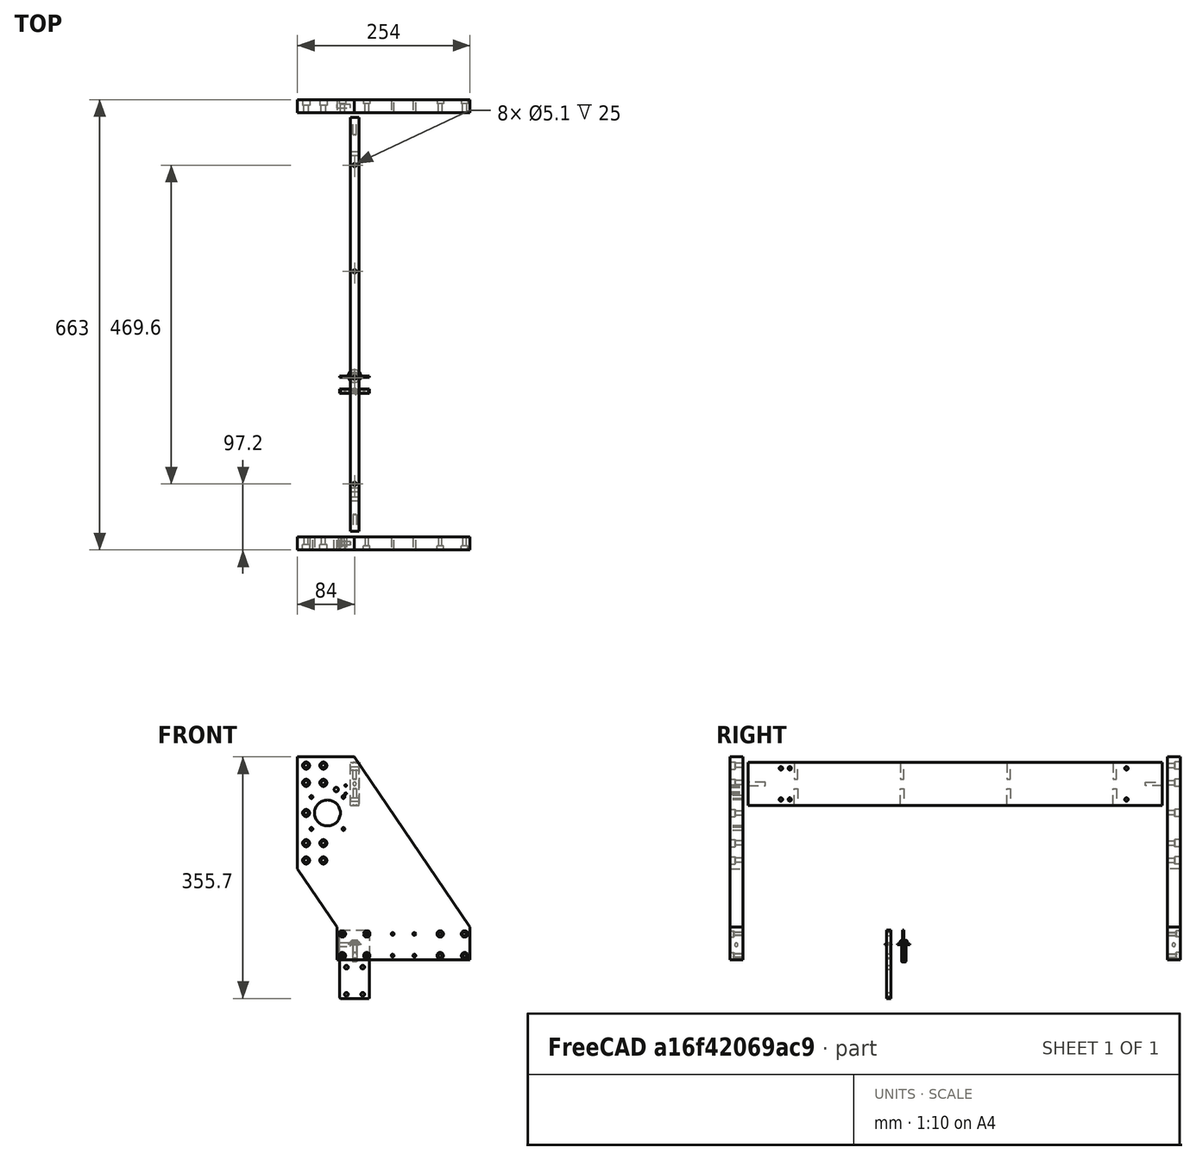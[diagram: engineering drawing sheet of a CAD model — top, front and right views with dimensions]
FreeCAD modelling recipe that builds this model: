
FCSTD DOCUMENT  (FreeCAD 2021.717R24301 +3842 (Git))
Label: X axis plates
License: Creative Commons Attribution
LicenseURL: http://creativecommons.org/licenses/by/4.0/
objects: App::FeaturePython×163, Part::FeaturePython×129, TechDraw::DrawViewDimension×92, App::LinkElement×42, Sketcher::SketchObject×20, App::Link×17, PartDesign::Pocket×9, PartDesign::Hole×6, TechDraw::DrawViewPart×6, PartDesign::Pad×5, PartDesign::Body×5, TechDraw::DrawSVGTemplate×4, TechDraw::DrawPage×4, App::DocumentObjectGroup×3, TechDraw::DrawProjGroupItem×3, PartDesign::Mirrored×2, PartDesign::Chamfer×2, PartDesign::ShapeBinder×1, TechDraw::DrawProjGroup×1
note: 223 computed .brp shape members not serialized (recipe doc carries the construction recipe); baked Part::Feature solids carry a one-line shape summary decoded from their .brp

FEATURE [Sketcher::SketchObject] Sketch
  FullyConstrained = true
  MapMode = 5
  Placement = pos=(0,0,0) rot=(1,0,0;1.5708rad)
  Support = -> [XZ_Plane]
  sketch-geometry (31):
    g0: Circle CenterX=-18 CenterY=16 CenterZ=0 NormalX=0 NormalY=0 NormalZ=1 AngleXU=0 Radius=2.75
    g1: Circle CenterX=18 CenterY=16 CenterZ=0 NormalX=0 NormalY=0 NormalZ=1 AngleXU=0 Radius=2.75
    g2: Circle CenterX=-18 CenterY=-16 CenterZ=0 NormalX=0 NormalY=0 NormalZ=1 AngleXU=0 Radius=2.75
    g3: Circle CenterX=18 CenterY=-16 CenterZ=0 NormalX=0 NormalY=0 NormalZ=1 AngleXU=0 Radius=2.75
    g4: Circle CenterX=126 CenterY=16 CenterZ=0 NormalX=0 NormalY=0 NormalZ=1 AngleXU=0 Radius=2.75
    g5: Circle CenterX=162 CenterY=16 CenterZ=0 NormalX=0 NormalY=0 NormalZ=1 AngleXU=0 Radius=2.75
    g6: Circle CenterX=126 CenterY=-16 CenterZ=0 NormalX=0 NormalY=0 NormalZ=1 AngleXU=0 Radius=2.75
    g7: Circle CenterX=162 CenterY=-16 CenterZ=0 NormalX=0 NormalY=0 NormalZ=1 AngleXU=0 Radius=2.75
    g8: Circle CenterX=-71.3 CenterY=124.3 CenterZ=0 NormalX=0 NormalY=0 NormalZ=1 AngleXU=0 Radius=3.2
    g9: Circle CenterX=-45.9 CenterY=124.3 CenterZ=0 NormalX=0 NormalY=0 NormalZ=1 AngleXU=0 Radius=3.2
    g10: Circle CenterX=-71.3 CenterY=149.7 CenterZ=0 NormalX=0 NormalY=0 NormalZ=1 AngleXU=0 Radius=3.2
    g11: Circle CenterX=-45.9 CenterY=149.7 CenterZ=0 NormalX=0 NormalY=0 NormalZ=1 AngleXU=0 Radius=3.2
    g12: Circle CenterX=-71.3 CenterY=238.6 CenterZ=0 NormalX=0 NormalY=0 NormalZ=1 AngleXU=0 Radius=3.2
    g13: Circle CenterX=-45.9 CenterY=238.6 CenterZ=0 NormalX=0 NormalY=0 NormalZ=1 AngleXU=0 Radius=3.2
    g14: Circle CenterX=-71.3 CenterY=264 CenterZ=0 NormalX=0 NormalY=0 NormalZ=1 AngleXU=0 Radius=3.2
    g15: Circle CenterX=-45.9 CenterY=264 CenterZ=0 NormalX=0 NormalY=0 NormalZ=1 AngleXU=0 Radius=3.2
    g16: LineSegment [constr] StartX=-71.3 StartY=124.3 StartZ=0 EndX=-45.9 EndY=124.3 EndZ=0
    g17: LineSegment [constr] StartX=-71.3 StartY=124.3 StartZ=0 EndX=-71.3 EndY=149.7 EndZ=0
    g18: LineSegment [constr] StartX=-71.3 StartY=238.6 StartZ=0 EndX=-71.3 EndY=264 EndZ=0
    g19: LineSegment [constr] StartX=-18 StartY=16 StartZ=0 EndX=18 EndY=16 EndZ=0
    g20: LineSegment [constr] StartX=126 StartY=16 StartZ=0 EndX=162 EndY=16 EndZ=0
    g21: GeomPoint [constr] X=-71.3 Y=137 Z=0
    g22: GeomPoint [constr] X=72 Y=16 Z=0
    g23: LineSegment StartX=-84 StartY=276.7 StartZ=0 EndX=-84 EndY=111.6 EndZ=0
    g24: LineSegment StartX=-84 StartY=111.6 StartZ=0 EndX=-26 EndY=26 EndZ=0
    g25: LineSegment StartX=-26 StartY=26 StartZ=0 EndX=-26 EndY=-22 EndZ=0
    g26: LineSegment StartX=-26 StartY=-22 StartZ=0 EndX=170 EndY=-22 EndZ=0
    g27: LineSegment StartX=170 StartY=-22 StartZ=0 EndX=170 EndY=26 EndZ=0
    g28: LineSegment StartX=170 StartY=26 StartZ=0 EndX=-0.6 EndY=276.7 EndZ=0
    g29: LineSegment StartX=-0.6 StartY=276.7 StartZ=0 EndX=-84 EndY=276.7 EndZ=0
    g30: GeomPoint [constr] X=72 Y=26 Z=0
  constraints (85):
    c: Vertical(g15,g13)
    c: Vertical(g13,g11)
    c: Vertical(g11,g9)
    c: Vertical(g14,g12)
    c: Vertical(g12,g10)
    c: Vertical(g10,g8)
    c: Horizontal(g14,g15)
    c: Horizontal(g12,g13)
    c: Horizontal(g10,g11)
    c: Horizontal(g8,g9)
    c: Equal(g8,g9)
    c: Equal(g9,g10)
    c: Equal(g10,g11)
    c: Equal(g11,g12)
    c: Equal(g12,g13)
    c: Equal(g13,g14)
    c: Equal(g14,g15)
    c: Horizontal(g0,g1)
    c: Horizontal(g1,g4)
    c: Horizontal(g4,g5)
    c: Horizontal(g2,g3)
    c: Horizontal(g3,g6)
    c: Horizontal(g6,g7)
    c: Vertical(g5,g7)
    c: Vertical(g4,g6)
    c: Vertical(g1,g3)
    c: Coincident(g16,g8)
    c: Coincident(g16,g9)
    c: Coincident(g17,g8)
    c: Coincident(g17,g10)
    c: Equal(g16,g17)
    c: DistanceX(g16,g16) = 25.4
    c: Coincident(g18,g12)
    c: Coincident(g18,g14)
    c: Equal(g18,g17)
    c: DistanceY(g8,g14) = 139.7
    c: Diameter(g14) = 6.4
    c: Diameter(g0) = 5.5
    c: Equal(g0,g1)
    c: Equal(g0,g4)
    c: Equal(g0,g5)
    c: Equal(g0,g7)
    c: Equal(g0,g6)
    c: Equal(g0,g3)
    c: Equal(g0,g2)
    c: Coincident(g19,g0)
    c: Coincident(g19,g1)
    c: Coincident(g20,g4)
    c: Coincident(g20,g5)
    c: Equal(g20,g19)
    c: DistanceX(g19,g19) = 36
    c: DistanceY(g2,g0) = 32
    c: DistanceX(g2,g7) = 180
    c: Symmetric(g2,g1,g-1)
    c: Vertical(g0,g2)
    c: Symmetric(g10,g8,g21)
    c: Symmetric(g1,g4,g22)
    c: Vertical(g23)
    c: Coincident(g23,g24)
    c: Coincident(g24,g25)
    c: Vertical(g25)
    c: Coincident(g25,g26)
    c: Horizontal(g26)
    c: Coincident(g26,g27)
    c: Vertical(g27)
    c: Coincident(g27,g28)
    c: Coincident(g28,g29)
    c: Coincident(g29,g23)
    c: Horizontal(g29)
    c: DistanceX(g25,g2) = 8
    c: DistanceX(g7,g26) = 8
    c: DistanceY(g14,g23) = 12.7
    c: DistanceX(g23,g14) = 12.7
    c: DistanceY(g0,g24) = 10
    c: DistanceY(g23,g8) = 12.7
    c: DistanceY(g25,g-1) = 22
    c: Horizontal(g27,g24)
    c: Symmetric(g24,g27,g30)
    c: DistanceY(g0,g8) = 108.3
    c: DistanceX(g23,g26) = 254
    c: DistanceY(g25,g23) = 298.7
    c: DistanceY(g27,g27) = 48
    c: DistanceX(g26,g26) = 196
    c: DistanceX(g29,g29) = 83.4
    c: DistanceY(g23,g23) = 165.1
FEATURE [PartDesign::Pad] Pad
  ClaimChildren = false
  Direction = (1,1,1)
  Fit = 0
  FitJoin = 0
  InnerFit = 0
  InnerFitJoin = 0
  InnerTaperAngle = 0
  InnerTaperAngleRev = 0
  Length = 19.05
  Length2 = 100
  Linearize = true
  NewSolid = false
  Placement = pos=(0,0,0) rot=(1,0,0;1.5708rad)
  Profile = -> Sketch
  Refine = true
  Reversed = true
  Suppress = false
  Type = 0
  _ProfileBasedVersion = 0
FEATURE [PartDesign::ShapeBinder] ShapeBinder
  Support = -> [Pad]
  TraceSupport = false
FEATURE [PartDesign::Pad] Pad001
  ClaimChildren = false
  Direction = (1,1,1)
  Fit = 0
  FitJoin = 0
  InnerFit = 0
  InnerFitJoin = 0
  InnerTaperAngle = 0
  InnerTaperAngleRev = 0
  Length = 19.05
  Length2 = 100
  Linearize = true
  NewSolid = false
  Profile = -> ShapeBinder
  Refine = true
  Suppress = false
  Type = 0
  _ProfileBasedVersion = 0
FEATURE [Sketcher::SketchObject] Sketch001
  ExternalGeometry = -> [Pad]
  FullyConstrained = true
  MapMode = 5
  Placement = pos=(0,-2e-16,0) rot=(1,0,0;1.5708rad)
  Support = -> [Pad]
  sketch-geometry (8):
    g0: Circle CenterX=-71.3 CenterY=264 CenterZ=0 NormalX=0 NormalY=0 NormalZ=1 AngleXU=0 Radius=3.2
    g1: Circle CenterX=-45.9 CenterY=264 CenterZ=0 NormalX=0 NormalY=0 NormalZ=1 AngleXU=0 Radius=3.2
    g2: Circle CenterX=-45.9 CenterY=238.6 CenterZ=0 NormalX=0 NormalY=0 NormalZ=1 AngleXU=0 Radius=3.2
    g3: Circle CenterX=-71.3 CenterY=238.6 CenterZ=0 NormalX=0 NormalY=0 NormalZ=1 AngleXU=0 Radius=3.2
    g4: Circle CenterX=-71.3 CenterY=149.7 CenterZ=0 NormalX=0 NormalY=0 NormalZ=1 AngleXU=0 Radius=3.2
    g5: Circle CenterX=-45.9 CenterY=149.7 CenterZ=0 NormalX=0 NormalY=0 NormalZ=1 AngleXU=0 Radius=3.2
    g6: Circle CenterX=-45.9 CenterY=124.3 CenterZ=0 NormalX=0 NormalY=0 NormalZ=1 AngleXU=0 Radius=3.2
    g7: Circle CenterX=-71.3 CenterY=124.3 CenterZ=0 NormalX=0 NormalY=0 NormalZ=1 AngleXU=0 Radius=3.2
  constraints (16):
    c: Coincident(g0,g-3)
    c: Coincident(g1,g-4)
    c: Coincident(g2,g-6)
    c: Coincident(g3,g-5)
    c: Coincident(g4,g-7)
    c: Coincident(g5,g-8)
    c: Coincident(g6,g-10)
    c: Coincident(g7,g-9)
    c: Equal(g1,g0)
    c: Equal(g0,g3)
    c: Equal(g3,g2)
    c: Equal(g2,g5)
    c: Equal(g5,g4)
    c: Equal(g4,g7)
    c: Equal(g7,g6)
    c: Equal(g6,g-3)
FEATURE [PartDesign::Hole] Hole
  BaseFeature = -> Pad
  ClaimChildren = false
  CustomThreadClearance = 0
  Depth = 25
  DepthType = 1
  Diameter = 6.4
  DrillForDepth = false
  DrillPoint = 1
  DrillPointAngle = 118
  Fit = 0
  FitJoin = 0
  HoleCutCountersinkAngle = 90
  HoleCutCustomValues = false
  HoleCutDepth = 8
  HoleCutDiameter = 10.5
  HoleCutType = 1
  InnerFit = 0
  InnerFitJoin = 0
  ModelThread = false
  NewSolid = false
  Placement = pos=(0,0,0) rot=(1,0,0;1.5708rad)
  Profile = -> Sketch001
  Refine = true
  Suppress = false
  Tapered = false
  TaperedAngle = 90
  ThreadClass = 0
  ThreadDepth = 896.71
  ThreadDepthType = 0
  ThreadDirection = 0
  ThreadFit = 0
  ThreadSize = 0
  ThreadType = 0
  Threaded = false
  UseCustomThreadClearance = false
  _ProfileBasedVersion = 0
FEATURE [Sketcher::SketchObject] Sketch002
  ExternalGeometry = -> [Hole]
  FullyConstrained = true
  MapMode = 5
  Placement = pos=(0,-2e-16,0) rot=(1,0,0;1.5708rad)
  Support = -> [Hole]
  sketch-geometry (8):
    g0: Circle CenterX=-18 CenterY=16 CenterZ=0 NormalX=0 NormalY=0 NormalZ=1 AngleXU=0 Radius=2.75
    g1: Circle CenterX=18 CenterY=16 CenterZ=0 NormalX=0 NormalY=0 NormalZ=1 AngleXU=0 Radius=2.75
    g2: Circle CenterX=-18 CenterY=-16 CenterZ=0 NormalX=0 NormalY=0 NormalZ=1 AngleXU=0 Radius=2.75
    g3: Circle CenterX=18 CenterY=-16 CenterZ=0 NormalX=0 NormalY=0 NormalZ=1 AngleXU=0 Radius=2.75
    g4: Circle CenterX=126 CenterY=16 CenterZ=0 NormalX=0 NormalY=0 NormalZ=1 AngleXU=0 Radius=2.75
    g5: Circle CenterX=162 CenterY=16 CenterZ=0 NormalX=0 NormalY=0 NormalZ=1 AngleXU=0 Radius=2.75
    g6: Circle CenterX=126 CenterY=-16 CenterZ=0 NormalX=0 NormalY=0 NormalZ=1 AngleXU=0 Radius=2.75
    g7: Circle CenterX=162 CenterY=-16 CenterZ=0 NormalX=0 NormalY=0 NormalZ=1 AngleXU=0 Radius=2.75
  constraints (16):
    c: Coincident(g0,g-3)
    c: Coincident(g1,g-4)
    c: Coincident(g2,g-6)
    c: Coincident(g3,g-5)
    c: Coincident(g4,g-7)
    c: Coincident(g5,g-8)
    c: Coincident(g6,g-9)
    c: Coincident(g7,g-10)
    c: Equal(g0,g1)
    c: Equal(g1,g2)
    c: Equal(g2,g3)
    c: Equal(g3,g4)
    c: Equal(g4,g6)
    c: Equal(g6,g5)
    c: Equal(g5,g7)
    c: Equal(g7,g-3)
FEATURE [PartDesign::Hole] Hole001
  BaseFeature = -> Hole
  ClaimChildren = false
  CustomThreadClearance = 0
  Depth = 25
  DepthType = 1
  Diameter = 5.5
  DrillForDepth = false
  DrillPoint = 1
  DrillPointAngle = 118
  Fit = 0
  FitJoin = 0
  HoleCutCountersinkAngle = 90
  HoleCutCustomValues = false
  HoleCutDepth = 6
  HoleCutDiameter = 9.5
  HoleCutType = 1
  InnerFit = 0
  InnerFitJoin = 0
  ModelThread = false
  NewSolid = false
  Placement = pos=(0,0,0) rot=(1,0,0;1.5708rad)
  Profile = -> Sketch002
  Refine = true
  Suppress = false
  Tapered = false
  TaperedAngle = 90
  ThreadClass = 0
  ThreadDepth = 901.62
  ThreadDepthType = 0
  ThreadDirection = 0
  ThreadFit = 0
  ThreadSize = 0
  ThreadType = 0
  Threaded = false
  UseCustomThreadClearance = false
  _ProfileBasedVersion = 0
FEATURE [Sketcher::SketchObject] Sketch003
  ExternalGeometry = -> [Pad001]
  FullyConstrained = true
  MapMode = 5
  Placement = pos=(0,-2e-16,0) rot=(0,0.707107,0.707107;3.14159rad)
  Support = -> [Pad001]
  sketch-geometry (8):
    g0: Circle CenterX=45.9 CenterY=238.6 CenterZ=0 NormalX=0 NormalY=0 NormalZ=1 AngleXU=0 Radius=3.2
    g1: Circle CenterX=71.3 CenterY=238.6 CenterZ=0 NormalX=0 NormalY=0 NormalZ=1 AngleXU=0 Radius=3.2
    g2: Circle CenterX=71.3 CenterY=149.7 CenterZ=0 NormalX=0 NormalY=0 NormalZ=1 AngleXU=0 Radius=3.2
    g3: Circle CenterX=45.9 CenterY=149.7 CenterZ=0 NormalX=0 NormalY=0 NormalZ=1 AngleXU=0 Radius=3.2
    g4: Circle CenterX=45.9 CenterY=124.3 CenterZ=0 NormalX=0 NormalY=0 NormalZ=1 AngleXU=0 Radius=3.2
    g5: Circle CenterX=71.3 CenterY=124.3 CenterZ=0 NormalX=0 NormalY=0 NormalZ=1 AngleXU=0 Radius=3.2
    g6: Circle CenterX=71.3 CenterY=264 CenterZ=0 NormalX=0 NormalY=0 NormalZ=1 AngleXU=0 Radius=3.2
    g7: Circle CenterX=45.9 CenterY=264 CenterZ=0 NormalX=0 NormalY=0 NormalZ=1 AngleXU=0 Radius=3.2
  constraints (16):
    c: Coincident(g0,g-3)
    c: Coincident(g1,g-10)
    c: Coincident(g2,g-4)
    c: Coincident(g3,g-5)
    c: Coincident(g4,g-6)
    c: Coincident(g5,g-7)
    c: Coincident(g6,g-8)
    c: Coincident(g7,g-9)
    c: Equal(g1,g0)
    c: Equal(g0,g3)
    c: Equal(g3,g2)
    c: Equal(g2,g5)
    c: Equal(g5,g4)
    c: Equal(g4,g7)
    c: Equal(g7,g6)
    c: Equal(g6,g-10)
FEATURE [PartDesign::Hole] Hole002
  BaseFeature = -> Pad001
  ClaimChildren = false
  CustomThreadClearance = 0
  Depth = 25
  DepthType = 1
  Diameter = 6.4
  DrillForDepth = false
  DrillPoint = 1
  DrillPointAngle = 118
  Fit = 0
  FitJoin = 0
  HoleCutCountersinkAngle = 90
  HoleCutCustomValues = false
  HoleCutDepth = 8
  HoleCutDiameter = 10.5
  HoleCutType = 1
  InnerFit = 0
  InnerFitJoin = 0
  ModelThread = false
  NewSolid = false
  Profile = -> Sketch003
  Refine = true
  Suppress = false
  Tapered = false
  TaperedAngle = 90
  ThreadClass = 0
  ThreadDepth = 901.62
  ThreadDepthType = 0
  ThreadDirection = 0
  ThreadFit = 0
  ThreadSize = 0
  ThreadType = 0
  Threaded = false
  UseCustomThreadClearance = false
  _ProfileBasedVersion = 0
FEATURE [Sketcher::SketchObject] Sketch004
  ExternalGeometry = -> [Hole002]
  FullyConstrained = false
  MapMode = 5
  Placement = pos=(0,-2e-16,0) rot=(0,0.707107,0.707107;3.14159rad)
  Support = -> [Hole002]
  sketch-geometry (9):
    g0: Circle CenterX=18 CenterY=-16 CenterZ=0 NormalX=0 NormalY=0 NormalZ=1 AngleXU=0 Radius=2.75
    g1: Circle CenterX=-162 CenterY=16 CenterZ=0 NormalX=0 NormalY=0 NormalZ=1 AngleXU=0 Radius=2.75
    g2: Circle CenterX=-162 CenterY=-16 CenterZ=0 NormalX=0 NormalY=0 NormalZ=1 AngleXU=0 Radius=2.75
    g3: Circle CenterX=-18 CenterY=-16 CenterZ=0 NormalX=0 NormalY=0 NormalZ=1 AngleXU=0 Radius=2.75
    g4: Circle CenterX=-126 CenterY=-16 CenterZ=0 NormalX=0 NormalY=0 NormalZ=1 AngleXU=0 Radius=2.75
    g5: Circle CenterX=-18 CenterY=16 CenterZ=0 NormalX=0 NormalY=0 NormalZ=1 AngleXU=0 Radius=2.75
    g6: Circle CenterX=18 CenterY=16 CenterZ=0 NormalX=0 NormalY=0 NormalZ=1 AngleXU=0 Radius=2.75
    g7: Circle CenterX=18 CenterY=16 CenterZ=0 NormalX=0 NormalY=0 NormalZ=1 AngleXU=0 Radius=2.75
    g8: Circle CenterX=-126 CenterY=16 CenterZ=0 NormalX=0 NormalY=0 NormalZ=1 AngleXU=0 Radius=2.75
  constraints (17):
    c: Coincident(g0,g-3)
    c: Coincident(g1,g-4)
    c: Coincident(g2,g-5)
    c: Coincident(g3,g-6)
    c: Coincident(g4,g-7)
    c: Coincident(g5,g-8)
    c: Coincident(g7,g-9)
    c: Equal(g0,g1)
    c: Equal(g1,g4)
    c: Equal(g4,g6)
    c: Equal(g6,g7)
    c: Equal(g7,g5)
    c: Equal(g5,g2)
    c: Equal(g2,g3)
    c: Equal(g3,g-3)
    c: Coincident(g8,g-10)
    c: Equal(g8,g0)
FEATURE [PartDesign::Hole] Hole003
  BaseFeature = -> Hole002
  ClaimChildren = false
  CustomThreadClearance = 0
  Depth = 25
  DepthType = 1
  Diameter = 5.5
  DrillForDepth = false
  DrillPoint = 1
  DrillPointAngle = 118
  Fit = 0
  FitJoin = 0
  HoleCutCountersinkAngle = 90
  HoleCutCustomValues = false
  HoleCutDepth = 6
  HoleCutDiameter = 9.5
  HoleCutType = 1
  InnerFit = 0
  InnerFitJoin = 0
  ModelThread = false
  NewSolid = false
  Profile = -> Sketch004
  Refine = true
  Suppress = false
  Tapered = false
  TaperedAngle = 90
  ThreadClass = 0
  ThreadDepth = 901.62
  ThreadDepthType = 0
  ThreadDirection = 0
  ThreadFit = 0
  ThreadSize = 0
  ThreadType = 0
  Threaded = false
  UseCustomThreadClearance = false
  _ProfileBasedVersion = 0
FEATURE [App::Link] Link  label="Link(Left plate)"
  AutoLinkLabel = true
  AutoPlacement = true
  LinkedObject = -> Body
  SyncGroupVisibility = false
  _LinkVersion = 1
FEATURE [App::Link] Link001  label="Link001(Right plate)"
  AutoLinkLabel = true
  AutoPlacement = true
  LinkPlacement = pos=(0,254,0) rot=(0,0,1;0rad)
  LinkedObject = -> Body001
  Placement = pos=(0,254,0) rot=(0,0,1;0rad)
  SyncGroupVisibility = false
  _LinkVersion = 1
FEATURE [Sketcher::SketchObject] Sketch005
  ExternalGeometry = -> [Hole001]
  FullyConstrained = true
  MapMode = 5
  Placement = pos=(0,-2e-16,0) rot=(1,0,0;1.5708rad)
  Support = -> [Hole001]
  sketch-geometry (8):
    g0: Circle CenterX=-39.95 CenterY=194.15 CenterZ=0 NormalX=0 NormalY=0 NormalZ=1 AngleXU=0 Radius=19.05
    g1: Circle CenterX=-63.5 CenterY=217.7 CenterZ=0 NormalX=0 NormalY=0 NormalZ=1 AngleXU=0 Radius=2.1
    g2: Circle CenterX=-16.4 CenterY=217.7 CenterZ=0 NormalX=0 NormalY=0 NormalZ=1 AngleXU=0 Radius=2.1
    g3: Circle CenterX=-63.5 CenterY=170.6 CenterZ=0 NormalX=0 NormalY=0 NormalZ=1 AngleXU=0 Radius=2.1
    g4: Circle CenterX=-16.4 CenterY=170.6 CenterZ=0 NormalX=0 NormalY=0 NormalZ=1 AngleXU=0 Radius=2.1
    g5: LineSegment [constr] StartX=-63.5 StartY=217.7 StartZ=0 EndX=-16.4 EndY=217.7 EndZ=0
    g6: LineSegment [constr] StartX=-63.5 StartY=217.7 StartZ=0 EndX=-63.5 EndY=170.6 EndZ=0
    g7: GeomPoint [constr] X=-71.3 Y=194.15 Z=0
  constraints (19):
    c: Diameter(g0) = 38.1
    c: Horizontal(g4,g3)
    c: Horizontal(g1,g2)
    c: Vertical(g2,g4)
    c: Vertical(g1,g3)
    c: Symmetric(g1,g4,g0)
    c: Diameter(g2) = 4.2
    c: Equal(g2,g1)
    c: Equal(g2,g3)
    c: Equal(g2,g4)
    c: Coincident(g5,g1)
    c: Coincident(g5,g2)
    c: Coincident(g6,g1)
    c: Coincident(g6,g3)
    c: Equal(g5,g6)
    c: DistanceX(g5,g5) = 47.1
    c: Symmetric(g-3,g-4,g7)
    c: Horizontal(g7,g0)
    c: DistanceX(g7,g0) = 31.35
FEATURE [PartDesign::Pocket] Pocket
  BaseFeature = -> Hole001
  ClaimChildren = false
  Fit = 0
  FitJoin = 0
  InnerFit = 0
  InnerFitJoin = 0
  InnerTaperAngle = 0
  InnerTaperAngleRev = 0
  Length = 5
  Length2 = 100
  Linearize = true
  NewSolid = false
  Placement = pos=(0,0,0) rot=(1,0,0;1.5708rad)
  Profile = -> Sketch005
  Refine = true
  Suppress = false
  Type = 1
  _ProfileBasedVersion = 0
FEATURE [Sketcher::SketchObject] Sketch006
  FullyConstrained = true
  MapMode = 5
  Placement = pos=(0,0,0) rot=(0.57735,0.57735,0.57735;2.0944rad)
  Support = -> [YZ_Plane002]
  sketch-geometry (4):
    g0: LineSegment StartX=-304.8 StartY=31.75 StartZ=0 EndX=304.8 EndY=31.75 EndZ=0
    g1: LineSegment StartX=304.8 StartY=31.75 StartZ=0 EndX=304.8 EndY=-31.75 EndZ=0
    g2: LineSegment StartX=304.8 StartY=-31.75 StartZ=0 EndX=-304.8 EndY=-31.75 EndZ=0
    g3: LineSegment StartX=-304.8 StartY=-31.75 StartZ=0 EndX=-304.8 EndY=31.75 EndZ=0
  constraints (11):
    c: Coincident(g0,g1)
    c: Coincident(g1,g2)
    c: Coincident(g2,g3)
    c: Coincident(g3,g0)
    c: Horizontal(g0)
    c: Horizontal(g2)
    c: Vertical(g1)
    c: Vertical(g3)
    c: Symmetric(g0,g2,g-1)
    c: DistanceY(g1,g1) = 63.5
    c: DistanceX(g0,g0) = 609.6
FEATURE [PartDesign::Pad] Pad002
  ClaimChildren = false
  Direction = (1,1,1)
  Fit = 0
  FitJoin = 0
  InnerFit = 0
  InnerFitJoin = 0
  InnerTaperAngle = 0
  InnerTaperAngleRev = 0
  Length = 12.7
  Length2 = 100
  Linearize = true
  Midplane = true
  NewSolid = false
  Placement = pos=(0,0,0) rot=(0.57735,0.57735,0.57735;2.0944rad)
  Profile = -> Sketch006
  Refine = true
  Suppress = false
  Type = 0
  _ProfileBasedVersion = 0
FEATURE [Sketcher::SketchObject] Sketch007
  FullyConstrained = true
  MapMode = 5
  Placement = pos=(-1.341e-13,-304.8,6.71e-14) rot=(-0.57735,-0.57735,0.57735;4.18879rad)
  Support = -> [Pad002]
  sketch-geometry (1):
    g0: Circle CenterX=0 CenterY=0 CenterZ=0 NormalX=0 NormalY=0 NormalZ=1 AngleXU=0 Radius=2.5
  constraints (2):
    c: Diameter(g0) = 5
    c: Coincident(g0,g-1)
FEATURE [PartDesign::Pocket] Pocket001
  BaseFeature = -> Pad002
  ClaimChildren = false
  Fit = 0
  FitJoin = 0
  InnerFit = 0
  InnerFitJoin = 0
  InnerTaperAngle = 0
  InnerTaperAngleRev = 0
  Length = 25
  Length2 = 100
  Linearize = true
  NewSolid = false
  Placement = pos=(0,0,0) rot=(0.57735,0.57735,0.57735;2.0944rad)
  Profile = -> Sketch007
  Refine = true
  Suppress = false
  Type = 0
  _ProfileBasedVersion = 0
FEATURE [Sketcher::SketchObject] Sketch008
  ExternalGeometry = -> [Pocket001]
  FullyConstrained = true
  MapMode = 5
  Placement = pos=(-2.29e-14,2.11e-14,31.75) rot=(0,0,-1;1.5708rad)
  sketch-geometry (9):
    g0: Circle CenterX=-234.8 CenterY=0 CenterZ=0 NormalX=0 NormalY=0 NormalZ=1 AngleXU=0 Radius=2.55
    g1: Circle CenterX=-78.2667 CenterY=0 CenterZ=0 NormalX=0 NormalY=0 NormalZ=1 AngleXU=0 Radius=2.55
    g2: Circle CenterX=78.2667 CenterY=0 CenterZ=0 NormalX=0 NormalY=0 NormalZ=1 AngleXU=0 Radius=2.55
    g3: Circle CenterX=234.8 CenterY=0 CenterZ=0 NormalX=0 NormalY=0 NormalZ=1 AngleXU=0 Radius=2.55
    g4: LineSegment [constr] StartX=-234.8 StartY=0 StartZ=0 EndX=-304.8 EndY=0 EndZ=0
    g5: LineSegment [constr] StartX=-234.8 StartY=0 StartZ=0 EndX=-78.2667 EndY=0 EndZ=0
    g6: LineSegment [constr] StartX=-78.2667 StartY=0 StartZ=0 EndX=78.2667 EndY=0 EndZ=0
    g7: LineSegment [constr] StartX=234.8 StartY=0 StartZ=0 EndX=78.2667 EndY=0 EndZ=0
    g8: LineSegment [constr] StartX=234.8 StartY=0 StartZ=0 EndX=304.8 EndY=0 EndZ=0
  constraints (24):
    c: PointOnObject(g0,g-1)
    c: PointOnObject(g1,g-1)
    c: Equal(g0,g1)
    c: DistanceX(g-3,g0) = 70
    c: PointOnObject(g2,g-1)
    c: PointOnObject(g3,g-1)
    c: Coincident(g4,g0)
    c: PointOnObject(g4,g-3)
    c: Horizontal(g4)
    c: Coincident(g5,g0)
    c: Coincident(g5,g1)
    c: Coincident(g6,g1)
    c: Coincident(g7,g3)
    c: Coincident(g7,g2)
    c: Coincident(g8,g3)
    c: PointOnObject(g8,g-1)
    c: Vertical(g8,g-4)
    c: Equal(g8,g4)
    c: Equal(g5,g6)
    c: Diameter(g0) = 5.1
    c: Coincident(g6,g2)
    c: Equal(g7,g6)
    c: Equal(g3,g2)
    c: Equal(g2,g1)
FEATURE [App::Link] Link003  label="Link003(Rear plate)"
  AutoLinkLabel = true
  AutoPlacement = true
  LinkPlacement = pos=(0,76,237) rot=(0,0,1;0rad)
  LinkedObject = -> Body002
  Placement = pos=(0,76,237) rot=(0,0,1;0rad)
  SyncGroupVisibility = false
  _LinkVersion = 1
FEATURE [Part::FeaturePython] Parts003  # WARN: FeaturePython — macro-defined, semantics opaque (R4)
  Group = -> [Link003]
  GroupMode = 0
  _LinkVersion = 1
FEATURE [Sketcher::SketchObject] Sketch014
  ExternalGeometry = -> [Hole003]
  FullyConstrained = true
  MapMode = 5
  Placement = pos=(0,-2e-16,0) rot=(0,0.707107,0.707107;3.14159rad)
  Support = -> [Hole003]
  sketch-geometry (1):
    g0: Circle CenterX=71.3 CenterY=194.15 CenterZ=0 NormalX=0 NormalY=0 NormalZ=1 AngleXU=0 Radius=3.05
  constraints (2):
    c: Diameter(g0) = 6.1
    c: Symmetric(g-3,g-4,g0)
FEATURE [PartDesign::Hole] Hole004
  BaseFeature = -> Hole003
  ClaimChildren = false
  CustomThreadClearance = 0
  Depth = 25
  DepthType = 1
  Diameter = 6.4
  DrillForDepth = false
  DrillPoint = 1
  DrillPointAngle = 118
  Fit = 0
  FitJoin = 0
  HoleCutCountersinkAngle = 90
  HoleCutCustomValues = false
  HoleCutDepth = 8
  HoleCutDiameter = 10.5
  HoleCutType = 1
  InnerFit = 0
  InnerFitJoin = 0
  ModelThread = false
  NewSolid = false
  Profile = -> Sketch014
  Refine = true
  Suppress = false
  Tapered = false
  TaperedAngle = 90
  ThreadClass = 0
  ThreadDepth = 901.62
  ThreadDepthType = 0
  ThreadDirection = 0
  ThreadFit = 0
  ThreadSize = 0
  ThreadType = 0
  Threaded = false
  UseCustomThreadClearance = false
  _ProfileBasedVersion = 0
FEATURE [Sketcher::SketchObject] Sketch015
  ExternalGeometry = -> [Pocket]
  FullyConstrained = true
  MapMode = 5
  Placement = pos=(0,-2e-16,0) rot=(1,0,0;1.5708rad)
  Support = -> [Pocket]
  sketch-geometry (1):
    g0: Circle CenterX=-71.3 CenterY=194.15 CenterZ=0 NormalX=0 NormalY=0 NormalZ=1 AngleXU=0 Radius=3.05
  constraints (2):
    c: Diameter(g0) = 6.1
    c: Symmetric(g-3,g-4,g0)
FEATURE [PartDesign::Hole] Hole005
  BaseFeature = -> Pocket
  ClaimChildren = false
  CustomThreadClearance = 0
  Depth = 25
  DepthType = 1
  Diameter = 6.4
  DrillForDepth = false
  DrillPoint = 1
  DrillPointAngle = 118
  Fit = 0
  FitJoin = 0
  HoleCutCountersinkAngle = 90
  HoleCutCustomValues = false
  HoleCutDepth = 8
  HoleCutDiameter = 10.5
  HoleCutType = 1
  InnerFit = 0
  InnerFitJoin = 0
  ModelThread = false
  NewSolid = false
  Placement = pos=(0,0,0) rot=(1,0,0;1.5708rad)
  Profile = -> Sketch015
  Refine = true
  Suppress = false
  Tapered = false
  TaperedAngle = 90
  ThreadClass = 0
  ThreadDepth = 901.62
  ThreadDepthType = 0
  ThreadDirection = 0
  ThreadFit = 0
  ThreadSize = 0
  ThreadType = 0
  Threaded = false
  UseCustomThreadClearance = false
  _ProfileBasedVersion = 0
FEATURE [Sketcher::SketchObject] Sketch021
  ExternalGeometry = -> [Hole004]
  FullyConstrained = true
  MapMode = 5
  Placement = pos=(0,-2e-16,0) rot=(0,0.707107,0.707107;3.14159rad)
  sketch-geometry (6):
    g0: GeomPoint [constr] X=-72 Y=-16 Z=0
    g1: GeomPoint [constr] X=-72 Y=-3.6e-15 Z=0
    g2: Circle CenterX=-88 CenterY=16 CenterZ=0 NormalX=0 NormalY=0 NormalZ=1 AngleXU=0 Radius=2.1
    g3: Circle CenterX=-88 CenterY=-16 CenterZ=0 NormalX=0 NormalY=0 NormalZ=1 AngleXU=0 Radius=2.1
    g4: Circle CenterX=-56 CenterY=16 CenterZ=0 NormalX=0 NormalY=0 NormalZ=1 AngleXU=0 Radius=2.1
    g5: Circle CenterX=-56 CenterY=-16 CenterZ=0 NormalX=0 NormalY=0 NormalZ=1 AngleXU=0 Radius=2.1
  constraints (13):
    c: Vertical(g1,g0)
    c: Equal(g5,g4)
    c: Equal(g4,g2)
    c: Equal(g2,g3)
    c: Vertical(g2,g3)
    c: Horizontal(g2,g4)
    c: Symmetric(g2,g5,g1)
    c: Symmetric(g3,g4,g1)
    c: Diameter(g4) = 4.2
    c: DistanceX(g2,g4) = 32
    c: DistanceY(g5,g4) = 32
    c: Horizontal(g5,g0)
    c: Symmetric(g-4,g-3,g0)
FEATURE [Sketcher::SketchObject] Sketch022
  ExternalGeometry = -> [Hole005]
  FullyConstrained = true
  MapMode = 5
  Placement = pos=(0,-2e-16,0) rot=(1,0,0;1.5708rad)
  Support = -> [Hole005]
  sketch-geometry (6):
    g0: GeomPoint [constr] X=72 Y=-16 Z=0
    g1: GeomPoint [constr] X=72 Y=6.6e-15 Z=0
    g2: Circle CenterX=56 CenterY=16 CenterZ=0 NormalX=0 NormalY=0 NormalZ=1 AngleXU=0 Radius=2.1
    g3: Circle CenterX=56 CenterY=-16 CenterZ=0 NormalX=0 NormalY=0 NormalZ=1 AngleXU=0 Radius=2.1
    g4: Circle CenterX=88 CenterY=16 CenterZ=0 NormalX=0 NormalY=0 NormalZ=1 AngleXU=0 Radius=2.1
    g5: Circle CenterX=88 CenterY=-16 CenterZ=0 NormalX=0 NormalY=0 NormalZ=1 AngleXU=0 Radius=2.1
  constraints (13):
    c: Vertical(g1,g0)
    c: Equal(g5,g4)
    c: Equal(g4,g2)
    c: Equal(g2,g3)
    c: Vertical(g2,g3)
    c: Horizontal(g2,g4)
    c: Symmetric(g2,g5,g1)
    c: Symmetric(g3,g4,g1)
    c: Diameter(g4) = 4.2
    c: DistanceX(g2,g4) = 32
    c: DistanceY(g5,g4) = 32
    c: Symmetric(g-3,g-4,g0)
    c: Horizontal(g5,g-4)
FEATURE [PartDesign::Mirrored] Mirrored001
  BaseFeature = -> Pocket001
  CopyShape = false
  MirrorPlane = -> XZ_Plane002
  NewSolid = false
  OriginalSubs = -> [Pocket001]
  Originals = -> [Pocket001]
  ParallelTransform = true
  Placement = pos=(0,0,0) rot=(0.57735,0.57735,0.57735;2.0944rad)
  Refine = true
  SubTransform = true
  Suppress = false
  _Version = 1
FEATURE [PartDesign::Pocket] Pocket002
  BaseFeature = -> Mirrored001
  ClaimChildren = false
  Fit = 0
  FitJoin = 0
  InnerFit = 0
  InnerFitJoin = 0
  InnerTaperAngle = 0
  InnerTaperAngleRev = 0
  Length = 25
  Length2 = 100
  Linearize = true
  NewSolid = false
  Placement = pos=(0,0,0) rot=(0.57735,0.57735,0.57735;2.0944rad)
  Profile = -> Sketch008
  Refine = true
  Suppress = false
  Type = 0
  _ProfileBasedVersion = 0
FEATURE [PartDesign::Mirrored] Mirrored
  BaseFeature = -> Pocket002
  CopyShape = false
  MirrorPlane = -> XY_Plane002
  NewSolid = false
  OriginalSubs = -> [Pocket002]
  Originals = -> [Pocket002]
  ParallelTransform = true
  Placement = pos=(0,0,0) rot=(0.57735,0.57735,0.57735;2.0944rad)
  Refine = true
  SubTransform = true
  Suppress = false
  _Version = 1
FEATURE [Sketcher::SketchObject] Sketch016
  ExternalGeometry = -> [Mirrored]
  FullyConstrained = true
  MapMode = 5
  Placement = pos=(6.35,-1.4e-15,1.4e-15) rot=(0.57735,0.57735,0.57735;2.0944rad)
  Support = -> [Mirrored]
  sketch-geometry (7):
    g0: Circle CenterX=-256.75 CenterY=23 CenterZ=0 NormalX=0 NormalY=0 NormalZ=1 AngleXU=0 Radius=2.5
    g1: Circle CenterX=-256.75 CenterY=-23 CenterZ=0 NormalX=0 NormalY=0 NormalZ=1 AngleXU=0 Radius=2.5
    g2: Circle CenterX=-243.75 CenterY=23 CenterZ=0 NormalX=0 NormalY=0 NormalZ=1 AngleXU=0 Radius=2.5
    g3: Circle CenterX=-243.75 CenterY=-23 CenterZ=0 NormalX=0 NormalY=0 NormalZ=1 AngleXU=0 Radius=2.5
    g4: GeomPoint [constr] X=-262.6 Y=23 Z=0
    g5: Circle CenterX=251.9 CenterY=23 CenterZ=0 NormalX=0 NormalY=0 NormalZ=1 AngleXU=0 Radius=2.5
    g6: Circle CenterX=251.9 CenterY=-23 CenterZ=0 NormalX=0 NormalY=0 NormalZ=1 AngleXU=0 Radius=2.5
  constraints (20):
    c: Vertical(g3,g2)
    c: Horizontal(g1,g3)
    c: Horizontal(g0,g2)
    c: Equal(g0,g2)
    c: Equal(g2,g3)
    c: Equal(g3,g1)
    c: Symmetric(g0,g1,g-1)
    c: Diameter(g0) = 5
    c: DistanceX(g0,g2) = 13
    c: DistanceY(g1,g0) = 46
    c: Horizontal(g4,g0)
    c: DistanceX(g4,g0) = 5.85
    c: Vertical(g6,g5)
    c: Horizontal(g6,g3)
    c: Horizontal(g2,g5)
    c: Equal(g5,g6)
    c: Equal(g6,g2)
    c: DistanceX(g-3,g4) = 42.2
    c: DistanceX(g-3,g0) = 48.05
    c: DistanceX(g4,g5) = 514.5
FEATURE [PartDesign::Pocket] Pocket007
  BaseFeature = -> Mirrored
  ClaimChildren = false
  Fit = 0
  FitJoin = 0
  InnerFit = 0
  InnerFitJoin = 0
  InnerTaperAngle = 0
  InnerTaperAngleRev = 0
  Length = 5
  Length2 = 100
  Linearize = true
  NewSolid = false
  Placement = pos=(0,0,0) rot=(0.57735,0.57735,0.57735;2.0944rad)
  Profile = -> Sketch016
  Refine = true
  Suppress = false
  Type = 1
  _ProfileBasedVersion = 0
FEATURE [PartDesign::Body] Body002  label="Rear plate"
  AutoGroupSolids = false
  ExportMode = 0
  Group = -> [Sketch006,Pad002,Sketch007,Pocket001,Sketch008,Mirrored001,Pocket002,Mirrored,Sketch016,Pocket007]
  Origin = -> Origin002
  Placement = pos=(0,76,237) rot=(0,0,1;0rad)
  Tip = -> Pocket007
  _ExportChildren = -> [Pad002,Pocket001,Mirrored001,Pocket002,Mirrored,Pocket007]
  _GroupVersion = 1
FEATURE [PartDesign::Pocket] Pocket010
  BaseFeature = -> Hole005
  ClaimChildren = false
  Fit = 0
  FitJoin = 0
  InnerFit = 0
  InnerFitJoin = 0
  InnerTaperAngle = 0
  InnerTaperAngleRev = 0
  Length = 5
  Length2 = 100
  Linearize = true
  NewSolid = false
  Placement = pos=(0,0,0) rot=(1,0,0;1.5708rad)
  Profile = -> Sketch022
  Refine = true
  Suppress = false
  Type = 1
  _ProfileBasedVersion = 0
FEATURE [PartDesign::Pocket] Pocket011
  BaseFeature = -> Hole004
  ClaimChildren = false
  Fit = 0
  FitJoin = 0
  InnerFit = 0
  InnerFitJoin = 0
  InnerTaperAngle = 0
  InnerTaperAngleRev = 0
  Length = 5
  Length2 = 100
  Linearize = true
  NewSolid = false
  Profile = -> Sketch021
  Refine = true
  Suppress = false
  Type = 1
  _ProfileBasedVersion = 0
FEATURE [Sketcher::SketchObject] Sketch023
  FullyConstrained = true
  MapMode = 5
  Placement = pos=(0,0,0) rot=(1,0,0;1.5708rad)
  Support = -> [XZ_Plane005]
  sketch-geometry (8):
    g0: LineSegment StartX=-22 StartY=22 StartZ=0 EndX=22 EndY=22 EndZ=0
    g1: LineSegment StartX=22 StartY=22 StartZ=0 EndX=22 EndY=-22 EndZ=0
    g2: LineSegment StartX=22 StartY=-22 StartZ=0 EndX=-22 EndY=-22 EndZ=0
    g3: LineSegment StartX=-22 StartY=-22 StartZ=0 EndX=-22 EndY=22 EndZ=0
    g4: Circle CenterX=-16 CenterY=16 CenterZ=0 NormalX=0 NormalY=0 NormalZ=1 AngleXU=0 Radius=2.75
    g5: Circle CenterX=16 CenterY=16 CenterZ=0 NormalX=0 NormalY=0 NormalZ=1 AngleXU=0 Radius=2.75
    g6: Circle CenterX=-16 CenterY=-16 CenterZ=0 NormalX=0 NormalY=0 NormalZ=1 AngleXU=0 Radius=2.75
    g7: Circle CenterX=16 CenterY=-16 CenterZ=0 NormalX=0 NormalY=0 NormalZ=1 AngleXU=0 Radius=2.75
  constraints (21):
    c: Coincident(g0,g1)
    c: Coincident(g1,g2)
    c: Coincident(g2,g3)
    c: Coincident(g3,g0)
    c: Horizontal(g0)
    c: Horizontal(g2)
    c: Vertical(g1)
    c: Vertical(g3)
    c: Symmetric(g1,g0,g-1)
    c: Equal(g0,g3)
    c: Diameter(g5) = 5.5
    c: Equal(g5,g4)
    c: Equal(g5,g6)
    c: Equal(g5,g7)
    c: Symmetric(g5,g6,g-1)
    c: Symmetric(g4,g7,g-1)
    c: Horizontal(g4,g5)
    c: Vertical(g6,g4)
    c: DistanceX(g4,g5) = 32
    c: DistanceY(g7,g5) = 32
    c: DistanceX(g0,g0) = 44
FEATURE [PartDesign::Pad] Pad005
  ClaimChildren = false
  Direction = (1,1,1)
  Fit = 0
  FitJoin = 0
  InnerFit = 0
  InnerFitJoin = 0
  InnerTaperAngle = 0
  InnerTaperAngleRev = 0
  Length = 1.825
  Length2 = 100
  Linearize = true
  NewSolid = false
  Placement = pos=(0,0,0) rot=(1,0,0;1.5708rad)
  Profile = -> Sketch023
  Refine = true
  Suppress = false
  Type = 0
  _ProfileBasedVersion = 0
FEATURE [PartDesign::Chamfer] Chamfer
  Angle = 45
  Base = -> Pad005 [Edge2,Edge1,Edge5,Edge8]
  BaseFeature = -> Pad005
  ChamferType = 0
  FlipDirection = false
  NewSolid = false
  Placement = pos=(0,0,0) rot=(1,0,0;1.5708rad)
  Refine = true
  Size = 1
  Size2 = 1
  SupportTransform = false
  Suppress = false
FEATURE [PartDesign::Body] Body005  label="Gouverner shim"
  AutoGroupSolids = false
  ExportMode = 0
  Group = -> [Sketch023,Pad005,Chamfer]
  Origin = -> Origin005
  Tip = -> Chamfer
  _ExportChildren = -> [Pad005,Chamfer]
  _GroupVersion = 1
FEATURE [Sketcher::SketchObject] Sketch024
  FullyConstrained = true
  MapMode = 5
  Placement = pos=(0,0,0) rot=(1,0,0;1.5708rad)
  Support = -> [XZ_Plane006]
  sketch-geometry (12):
    g0: LineSegment StartX=-22 StartY=22 StartZ=0 EndX=22 EndY=22 EndZ=0
    g1: LineSegment StartX=22 StartY=22 StartZ=0 EndX=22 EndY=-79 EndZ=0
    g2: LineSegment StartX=22 StartY=-79 StartZ=0 EndX=-22 EndY=-79 EndZ=0
    g3: LineSegment StartX=-22 StartY=-79 StartZ=0 EndX=-22 EndY=22 EndZ=0
    g4: Circle CenterX=-16 CenterY=16 CenterZ=0 NormalX=0 NormalY=0 NormalZ=1 AngleXU=0 Radius=2.75
    g5: Circle CenterX=16 CenterY=16 CenterZ=0 NormalX=0 NormalY=0 NormalZ=1 AngleXU=0 Radius=2.75
    g6: Circle CenterX=-16 CenterY=-16 CenterZ=0 NormalX=0 NormalY=0 NormalZ=1 AngleXU=0 Radius=2.75
    g7: Circle CenterX=16 CenterY=-16 CenterZ=0 NormalX=0 NormalY=0 NormalZ=1 AngleXU=0 Radius=2.75
    g8: Circle CenterX=-12 CenterY=-33 CenterZ=0 NormalX=0 NormalY=0 NormalZ=1 AngleXU=0 Radius=2.75
    g9: Circle CenterX=12 CenterY=-33 CenterZ=0 NormalX=0 NormalY=0 NormalZ=1 AngleXU=0 Radius=2.75
    g10: Circle CenterX=-12 CenterY=-73 CenterZ=0 NormalX=0 NormalY=0 NormalZ=1 AngleXU=0 Radius=2.75
    g11: Circle CenterX=12 CenterY=-73 CenterZ=0 NormalX=0 NormalY=0 NormalZ=1 AngleXU=0 Radius=2.75
  constraints (32):
    c: Coincident(g0,g1)
    c: Coincident(g1,g2)
    c: Coincident(g2,g3)
    c: Coincident(g3,g0)
    c: Horizontal(g2)
    c: Vertical(g1)
    c: Vertical(g3)
    c: DistanceX(g0,g0) = 44
    c: Symmetric(g0,g0,g-2)
    c: DistanceY(g-1,g0) = 22
    c: Diameter(g7) = 5.5
    c: Equal(g7,g6)
    c: Equal(g7,g4)
    c: Equal(g7,g5)
    c: Horizontal(g6,g7)
    c: Vertical(g4,g6)
    c: Symmetric(g4,g5,g-2)
    c: DistanceX(g4,g5) = 32
    c: Symmetric(g5,g7,g-1)
    c: DistanceY(g7,g5) = 32
    c: Horizontal(g11,g10)
    c: Vertical(g9,g11)
    c: Vertical(g8,g10)
    c: Symmetric(g8,g9,g-2)
    c: DistanceY(g11,g9) = 40
    c: DistanceX(g8,g9) = 24
    c: Diameter(g9) = 5.5
    c: Equal(g9,g8)
    c: Equal(g9,g10)
    c: Equal(g9,g11)
    c: DistanceY(g9,g7) = 17
    c: DistanceY(g1,g0) = 101
FEATURE [PartDesign::Pad] Pad006
  ClaimChildren = false
  Direction = (1,1,1)
  Fit = 0
  FitJoin = 0
  InnerFit = 0
  InnerFitJoin = 0
  InnerTaperAngle = 0
  InnerTaperAngleRev = 0
  Length = 6.35
  Length2 = 100
  Linearize = true
  NewSolid = false
  Placement = pos=(0,0,0) rot=(1,0,0;1.5708rad)
  Profile = -> Sketch024
  Refine = true
  Suppress = false
  Type = 0
  _ProfileBasedVersion = 0
FEATURE [PartDesign::Chamfer] Chamfer001
  Angle = 45
  Base = -> Pad006 [Edge2,Edge1,Edge5,Edge8]
  BaseFeature = -> Pad006
  ChamferType = 0
  FlipDirection = false
  NewSolid = false
  Placement = pos=(0,0,0) rot=(1,0,0;1.5708rad)
  Refine = true
  Size = 1
  Size2 = 1
  SupportTransform = false
  Suppress = false
FEATURE [PartDesign::Body] Body006  label="Gouverner"
  AutoGroupSolids = false
  ExportMode = 0
  Group = -> [Sketch024,Pad006,Chamfer001]
  Origin = -> Origin006
  Placement = pos=(0,-19,0) rot=(0,0,1;0rad)
  Tip = -> Chamfer001
  _ExportChildren = -> [Pad006,Chamfer001]
  _GroupVersion = 1
FEATURE [App::Link] Link005  label="Link005(Gouverner shim)"
  AutoLinkLabel = true
  AutoPlacement = true
  LinkedObject = -> Body005
  SyncGroupVisibility = false
  _LinkVersion = 1
FEATURE [App::Link] Link006  label="Link006(Gouverner)"
  AutoLinkLabel = true
  AutoPlacement = true
  LinkPlacement = pos=(-2.13e-14,-1.825,-1.8e-15) rot=(0,0,1;0rad)
  LinkedObject = -> Body006
  Placement = pos=(-2.13e-14,-1.825,-1.8e-15) rot=(0,0,1;0rad)
  SyncGroupVisibility = false
  _LinkVersion = 1
FEATURE [Sketcher::SketchObject] Sketch025  label="Stock layout"
  FullyConstrained = true
  Placement = pos=(0,0,0) rot=(-1,0,0;4.71239rad)
  sketch-geometry (19):
    g0: LineSegment StartX=0 StartY=299 StartZ=0 EndX=0 EndY=134 EndZ=0
    g1: LineSegment StartX=0 StartY=134 StartZ=0 EndX=58 EndY=49 EndZ=0
    g2: LineSegment StartX=58 StartY=49 StartZ=0 EndX=58 EndY=0 EndZ=0
    g3: LineSegment StartX=58 StartY=0 StartZ=0 EndX=254 EndY=0 EndZ=0
    g4: LineSegment StartX=254 StartY=0 StartZ=0 EndX=254 EndY=49 EndZ=0
    g5: LineSegment StartX=254 StartY=49 StartZ=0 EndX=83.4118 EndY=299 EndZ=0
    g6: LineSegment StartX=83.4118 StartY=299 StartZ=0 EndX=0 EndY=299 EndZ=0
    g7: LineSegment StartX=304.8 StartY=107.4 StartZ=0 EndX=304.8 EndY=272.4 EndZ=0
    g8: LineSegment StartX=304.8 StartY=272.4 StartZ=0 EndX=246.8 EndY=357.4 EndZ=0
    g9: LineSegment StartX=246.8 StartY=357.4 StartZ=0 EndX=246.8 EndY=406.4 EndZ=0
    g10: LineSegment StartX=246.8 StartY=406.4 StartZ=0 EndX=50.8 EndY=406.4 EndZ=0
    g11: LineSegment StartX=50.8 StartY=406.4 StartZ=0 EndX=50.8 EndY=357.4 EndZ=0
    g12: LineSegment StartX=50.8 StartY=357.4 StartZ=0 EndX=221.388 EndY=107.4 EndZ=0
    g13: LineSegment StartX=221.388 StartY=107.4 StartZ=0 EndX=304.8 EndY=107.4 EndZ=0
    g14: LineSegment StartX=0 StartY=406.4 StartZ=0 EndX=304.8 EndY=406.4 EndZ=0
    g15: LineSegment StartX=304.8 StartY=406.4 StartZ=0 EndX=304.8 EndY=0 EndZ=0
    g16: LineSegment StartX=304.8 StartY=0 StartZ=0 EndX=0 EndY=0 EndZ=0
    g17: LineSegment StartX=0 StartY=0 StartZ=0 EndX=0 EndY=406.4 EndZ=0
    g18: LineSegment [constr] StartX=221.388 StartY=107.4 StartZ=0 EndX=216.45 EndY=104.03 EndZ=0
  constraints (60):
    c: Vertical(g0)
    c: Coincident(g0,g1)
    c: Coincident(g1,g2)
    c: Vertical(g2)
    c: Coincident(g2,g3)
    c: Horizontal(g3)
    c: Coincident(g3,g4)
    c: Vertical(g4)
    c: Coincident(g4,g5)
    c: Coincident(g5,g6)
    c: Coincident(g6,g0)
    c: Horizontal(g6)
    c: Coincident(g7,g8)
    c: Coincident(g8,g9)
    c: Coincident(g9,g10)
    c: Coincident(g10,g11)
    c: Coincident(g11,g12)
    c: Coincident(g12,g13)
    c: Coincident(g13,g7)
    c: Perpendicular(g10,g11)
    c: Perpendicular(g10,g9)
    c: Perpendicular(g13,g7)
    c: Parallel(g12,g8)
    c: Equal(g4,g11)
    c: Equal(g9,g2)
    c: Equal(g3,g10)
    c: Equal(g6,g13)
    c: Equal(g0,g7)
    c: DistanceX(g3,g3) = 196
    c: DistanceX(g0,g3) = 254
    c: DistanceY(g2,g0) = 299
    c: DistanceY(g0,g0) = 165
    c: Equal(g2,g4)
    c: Equal(g8,g1)
    c: Horizontal(g10)
    c: Coincident(g14,g15)
    c: Coincident(g15,g16)
    c: Coincident(g16,g17)
    c: Coincident(g17,g14)
    c: Horizontal(g14)
    c: Horizontal(g16)
    c: Vertical(g15)
    c: Vertical(g17)
    c: DistanceX(g16,g16) = 304.8
    c: DistanceY(g15,g15) = 406.4
    c: Horizontal(g2,g16)
    c: Vertical(g0,g16)
    c: Horizontal(g9,g14)
    c: Vertical(g14,g7)
    c: Vertical(g7)
    c: Parallel(g5,g12)
    c: Coincident(g18,g12)
    c: PointOnObject(g18,g5)
    c: Perpendicular(g5,g18)
    c: DistanceY(g4,g4) = 49
    c: DistanceY(g0,g11) = 58.4
    c: DistanceX(g0,g11) = 50.8
    c: Coincident(g16,g-1)
    c: Distance(g18) = 5.97845
    c: DistanceX(g6,g6) = 83.4118
FEATURE [Part::FeaturePython] Screw  label="1/4inx1in-Screw"  # Fasteners workbench fastener (typed FeaturePython)
  diameter = 10
  invert = false
  length = 4
  lengthCustom = 25.4
  matchOuter = false
  offset = 0
  thread = false
  type = 2
FEATURE [Part::FeaturePython] Screw001  label="M5x20-Screw"  # Fasteners workbench fastener (typed FeaturePython)
  Placement = pos=(0,-23,0) rot=(0,0,1;0rad)
  diameter = 3
  invert = false
  length = 5
  lengthCustom = 20
  matchOuter = false
  offset = 0
  thread = false
  type = 39
FEATURE [App::LinkElement] Link007_i0
  LinkPlacement = pos=(-45.9,8,264) rot=(1,0,0;1.5708rad)
  LinkedObject = -> Screw
  Placement = pos=(-45.9,8,264) rot=(1,0,0;1.5708rad)
  _LinkVersion = 1
FEATURE [App::LinkElement] Link007_i1
  LinkPlacement = pos=(-45.9,8,238.6) rot=(1,0,0;1.5708rad)
  LinkedObject = -> Screw
  Placement = pos=(-45.9,8,238.6) rot=(1,0,0;1.5708rad)
  _LinkVersion = 1
FEATURE [App::LinkElement] Link007_i2
  LinkPlacement = pos=(-71.3,8,264) rot=(1,0,0;1.5708rad)
  LinkedObject = -> Screw
  Placement = pos=(-71.3,8,264) rot=(1,0,0;1.5708rad)
  _LinkVersion = 1
FEATURE [App::LinkElement] Link007_i3
  LinkPlacement = pos=(-71.3,8,238.6) rot=(1,0,0;1.5708rad)
  LinkedObject = -> Screw
  Placement = pos=(-71.3,8,238.6) rot=(1,0,0;1.5708rad)
  _LinkVersion = 1
FEATURE [App::LinkElement] Link007_i4
  LinkPlacement = pos=(-71.3,8,194.15) rot=(1,0,0;1.5708rad)
  LinkedObject = -> Screw
  Placement = pos=(-71.3,8,194.15) rot=(1,0,0;1.5708rad)
  _LinkVersion = 1
FEATURE [App::LinkElement] Link007_i5
  LinkPlacement = pos=(-45.9,8,124.3) rot=(1,0,0;1.5708rad)
  LinkedObject = -> Screw
  Placement = pos=(-45.9,8,124.3) rot=(1,0,0;1.5708rad)
  _LinkVersion = 1
FEATURE [App::LinkElement] Link007_i6
  LinkPlacement = pos=(-71.3,8,124.3) rot=(1,0,0;1.5708rad)
  LinkedObject = -> Screw
  Placement = pos=(-71.3,8,124.3) rot=(1,0,0;1.5708rad)
  _LinkVersion = 1
FEATURE [App::LinkElement] Link007_i7
  LinkPlacement = pos=(-71.3,8,149.7) rot=(1,0,0;1.5708rad)
  LinkedObject = -> Screw
  Placement = pos=(-71.3,8,149.7) rot=(1,0,0;1.5708rad)
  _LinkVersion = 1
FEATURE [App::LinkElement] Link007_i8
  LinkPlacement = pos=(-45.9,8,149.7) rot=(1,0,0;1.5708rad)
  LinkedObject = -> Screw
  Placement = pos=(-45.9,8,149.7) rot=(1,0,0;1.5708rad)
  _LinkVersion = 1
FEATURE [App::Link] Link007  label="1/4inx1in- 9 Screws"
  AutoLinkLabel = true
  AutoPlacement = true
  ElementCount = 9
  ElementList = -> [Link007_i0,Link007_i1,Link007_i2,Link007_i3,Link007_i4,Link007_i5,Link007_i6,Link007_i7,Link007_i8]
  LinkedObject = -> Screw
  SyncGroupVisibility = false
  _LinkVersion = 1
FEATURE [App::LinkElement] Link008_i0
  LinkPlacement = pos=(-18,29,16) rot=(1,0,0;1.5708rad)
  LinkedObject = -> Group [Screw003.]
  Placement = pos=(-18,29,16) rot=(1,0,0;1.5708rad)
  _LinkVersion = 1
FEATURE [App::LinkElement] Link008_i1
  LinkPlacement = pos=(-18,29,-16) rot=(1,0,0;1.5708rad)
  LinkedObject = -> Group [Screw003.]
  Placement = pos=(-18,29,-16) rot=(1,0,0;1.5708rad)
  _LinkVersion = 1
FEATURE [App::LinkElement] Link008_i2
  LinkPlacement = pos=(18,29,16) rot=(1,0,0;1.5708rad)
  LinkedObject = -> Group [Screw003.]
  Placement = pos=(18,29,16) rot=(1,0,0;1.5708rad)
  _LinkVersion = 1
FEATURE [App::LinkElement] Link008_i3
  LinkPlacement = pos=(18,29,-16) rot=(1,0,0;1.5708rad)
  LinkedObject = -> Group [Screw003.]
  Placement = pos=(18,29,-16) rot=(1,0,0;1.5708rad)
  _LinkVersion = 1
FEATURE [App::LinkElement] Link008_i4
  LinkPlacement = pos=(162,29,-16) rot=(1,0,0;1.5708rad)
  LinkedObject = -> Group [Screw003.]
  Placement = pos=(162,29,-16) rot=(1,0,0;1.5708rad)
  _LinkVersion = 1
FEATURE [App::LinkElement] Link008_i5
  LinkPlacement = pos=(126,29,-16) rot=(1,0,0;1.5708rad)
  LinkedObject = -> Group [Screw003.]
  Placement = pos=(126,29,-16) rot=(1,0,0;1.5708rad)
  _LinkVersion = 1
FEATURE [App::LinkElement] Link008_i6
  LinkPlacement = pos=(126,29,16) rot=(1,0,0;1.5708rad)
  LinkedObject = -> Group [Screw003.]
  Placement = pos=(126,29,16) rot=(1,0,0;1.5708rad)
  _LinkVersion = 1
FEATURE [App::LinkElement] Link008_i7
  LinkPlacement = pos=(162,29,16) rot=(1,0,0;1.5708rad)
  LinkedObject = -> Group [Screw003.]
  Placement = pos=(162,29,16) rot=(1,0,0;1.5708rad)
  _LinkVersion = 1
FEATURE [App::Link] Link008  label="M5x20- 8 Screws"
  AutoLinkLabel = true
  AutoPlacement = true
  ElementCount = 8
  ElementList = -> [Link008_i0,Link008_i1,Link008_i2,Link008_i3,Link008_i4,Link008_i5,Link008_i6,Link008_i7]
  LinkPlacement = pos=(0,-23,0) rot=(0,0,1;0rad)
  LinkedObject = -> Group [Screw003.]
  Placement = pos=(0,-23,0) rot=(0,0,1;0rad)
  SyncGroupVisibility = false
  _LinkVersion = 1
FEATURE [App::LinkElement] Link009_i0
  LinkPlacement = pos=(-45.9,-36,238.6) rot=(-1,0,0;1.5708rad)
  LinkedObject = -> Screw
  Placement = pos=(-45.9,-36,238.6) rot=(-1,0,0;1.5708rad)
  _LinkVersion = 1
FEATURE [App::LinkElement] Link009_i1
  LinkPlacement = pos=(-71.3,-36,238.6) rot=(-1,0,0;1.5708rad)
  LinkedObject = -> Screw
  Placement = pos=(-71.3,-36,238.6) rot=(-1,0,0;1.5708rad)
  _LinkVersion = 1
FEATURE [App::LinkElement] Link009_i2
  LinkPlacement = pos=(-45.9,-36,149.7) rot=(-1,0,0;1.5708rad)
  LinkedObject = -> Screw
  Placement = pos=(-45.9,-36,149.7) rot=(-1,0,0;1.5708rad)
  _LinkVersion = 1
FEATURE [App::LinkElement] Link009_i3
  LinkPlacement = pos=(-71.3,-36,149.7) rot=(-1,0,0;1.5708rad)
  LinkedObject = -> Screw
  Placement = pos=(-71.3,-36,149.7) rot=(-1,0,0;1.5708rad)
  _LinkVersion = 1
FEATURE [App::LinkElement] Link009_i4
  LinkPlacement = pos=(-45.9,-36,124.3) rot=(-1,0,0;1.5708rad)
  LinkedObject = -> Screw
  Placement = pos=(-45.9,-36,124.3) rot=(-1,0,0;1.5708rad)
  _LinkVersion = 1
FEATURE [App::LinkElement] Link009_i5
  LinkPlacement = pos=(-45.9,-36,264) rot=(-1,0,0;1.5708rad)
  LinkedObject = -> Screw
  Placement = pos=(-45.9,-36,264) rot=(-1,0,0;1.5708rad)
  _LinkVersion = 1
FEATURE [App::LinkElement] Link009_i6
  LinkPlacement = pos=(-71.3,-36,264) rot=(-1,0,0;1.5708rad)
  LinkedObject = -> Screw
  Placement = pos=(-71.3,-36,264) rot=(-1,0,0;1.5708rad)
  _LinkVersion = 1
FEATURE [App::LinkElement] Link009_i7
  LinkPlacement = pos=(-71.3,-36,124.3) rot=(-1,0,0;1.5708rad)
  LinkedObject = -> Screw
  Placement = pos=(-71.3,-36,124.3) rot=(-1,0,0;1.5708rad)
  _LinkVersion = 1
FEATURE [App::LinkElement] Link009_i8
  LinkPlacement = pos=(-71.3,-36,194.15) rot=(-1,0,0;1.5708rad)
  LinkedObject = -> Screw
  Placement = pos=(-71.3,-36,194.15) rot=(-1,0,0;1.5708rad)
  _LinkVersion = 1
FEATURE [App::Link] Link009  label="1/4inx1in-9 Screws"
  AutoLinkLabel = true
  AutoPlacement = true
  ElementCount = 9
  ElementList = -> [Link009_i0,Link009_i1,Link009_i2,Link009_i3,Link009_i4,Link009_i5,Link009_i6,Link009_i7,Link009_i8]
  LinkPlacement = pos=(0,282,0) rot=(0,0,1;0rad)
  LinkedObject = -> Screw
  Placement = pos=(0,282,0) rot=(0,0,1;0rad)
  SyncGroupVisibility = false
  _LinkVersion = 1
FEATURE [App::LinkElement] Link010_i0
  LinkPlacement = pos=(-18,-36,16) rot=(-1,0,0;1.5708rad)
  LinkedObject = -> Group [Screw003.]
  Placement = pos=(-18,-36,16) rot=(-1,0,0;1.5708rad)
  _LinkVersion = 1
FEATURE [App::LinkElement] Link010_i1
  LinkPlacement = pos=(18,-36,16) rot=(-1,0,0;1.5708rad)
  LinkedObject = -> Group [Screw003.]
  Placement = pos=(18,-36,16) rot=(-1,0,0;1.5708rad)
  _LinkVersion = 1
FEATURE [App::LinkElement] Link010_i2
  LinkPlacement = pos=(18,-36,-16) rot=(-1,0,0;1.5708rad)
  LinkedObject = -> Group [Screw003.]
  Placement = pos=(18,-36,-16) rot=(-1,0,0;1.5708rad)
  _LinkVersion = 1
FEATURE [App::LinkElement] Link010_i3
  LinkPlacement = pos=(-18,-36,-16) rot=(-1,0,0;1.5708rad)
  LinkedObject = -> Group [Screw003.]
  Placement = pos=(-18,-36,-16) rot=(-1,0,0;1.5708rad)
  _LinkVersion = 1
FEATURE [App::LinkElement] Link010_i4
  LinkPlacement = pos=(162,-36,-16) rot=(-1,0,0;1.5708rad)
  LinkedObject = -> Group [Screw003.]
  Placement = pos=(162,-36,-16) rot=(-1,0,0;1.5708rad)
  _LinkVersion = 1
FEATURE [App::LinkElement] Link010_i5
  LinkPlacement = pos=(126,-36,-16) rot=(-1,0,0;1.5708rad)
  LinkedObject = -> Group [Screw003.]
  Placement = pos=(126,-36,-16) rot=(-1,0,0;1.5708rad)
  _LinkVersion = 1
FEATURE [App::LinkElement] Link010_i6
  LinkPlacement = pos=(162,-36,16) rot=(-1,0,0;1.5708rad)
  LinkedObject = -> Group [Screw003.]
  Placement = pos=(162,-36,16) rot=(-1,0,0;1.5708rad)
  _LinkVersion = 1
FEATURE [App::LinkElement] Link010_i7
  LinkPlacement = pos=(126,-36,16) rot=(-1,0,0;1.5708rad)
  LinkedObject = -> Group [Screw003.]
  Placement = pos=(126,-36,16) rot=(-1,0,0;1.5708rad)
  _LinkVersion = 1
FEATURE [App::Link] Link010  label="M5x20- 8 Screws001"
  AutoLinkLabel = true
  AutoPlacement = true
  ElementCount = 8
  ElementList = -> [Link010_i0,Link010_i1,Link010_i2,Link010_i3,Link010_i4,Link010_i5,Link010_i6,Link010_i7]
  LinkPlacement = pos=(0,284,0) rot=(0,0,1;0rad)
  LinkedObject = -> Group [Screw003.]
  Placement = pos=(0,284,0) rot=(0,0,1;0rad)
  SyncGroupVisibility = false
  _LinkVersion = 1
FEATURE [Part::FeaturePython] Screw002  label="M5x12-Screw"  # Fasteners workbench fastener (typed FeaturePython)
  diameter = 3
  invert = false
  length = 2
  lengthCustom = 12
  matchOuter = false
  offset = 0
  thread = false
  type = 39
FEATURE [App::LinkElement] Link011_i0
  LinkPlacement = pos=(-12,20.825,-33) rot=(1,0,0;1.5708rad)
  LinkedObject = -> Screw002
  Placement = pos=(-12,20.825,-33) rot=(1,0,0;1.5708rad)
  _LinkVersion = 1
FEATURE [App::LinkElement] Link011_i1
  LinkPlacement = pos=(12,20.825,-33) rot=(1,0,0;1.5708rad)
  LinkedObject = -> Screw002
  Placement = pos=(12,20.825,-33) rot=(1,0,0;1.5708rad)
  _LinkVersion = 1
FEATURE [App::LinkElement] Link011_i2
  LinkPlacement = pos=(12,20.825,-73) rot=(1,0,0;1.5708rad)
  LinkedObject = -> Screw002
  Placement = pos=(12,20.825,-73) rot=(1,0,0;1.5708rad)
  _LinkVersion = 1
FEATURE [App::LinkElement] Link011_i3
  LinkPlacement = pos=(-12,20.825,-73) rot=(1,0,0;1.5708rad)
  LinkedObject = -> Screw002
  Placement = pos=(-12,20.825,-73) rot=(1,0,0;1.5708rad)
  _LinkVersion = 1
FEATURE [App::Link] Link011  label="M5x12-4 Screws"
  AutoLinkLabel = true
  AutoPlacement = true
  ElementCount = 4
  ElementList = -> [Link011_i0,Link011_i1,Link011_i2,Link011_i3]
  LinkPlacement = pos=(0,-29,0) rot=(0,0,1;0rad)
  LinkedObject = -> Screw002
  Placement = pos=(0,-29,0) rot=(0,0,1;0rad)
  SyncGroupVisibility = false
  _LinkVersion = 1
FEATURE [App::LinkElement] Link012_i0
  LinkPlacement = pos=(-16,25.825,16) rot=(1,0,0;1.5708rad)
  LinkedObject = -> Screw001
  Placement = pos=(-16,25.825,16) rot=(1,0,0;1.5708rad)
  _LinkVersion = 1
FEATURE [App::LinkElement] Link012_i1
  LinkPlacement = pos=(16,25.825,16) rot=(1,0,0;1.5708rad)
  LinkedObject = -> Screw001
  Placement = pos=(16,25.825,16) rot=(1,0,0;1.5708rad)
  _LinkVersion = 1
FEATURE [App::LinkElement] Link012_i2
  LinkPlacement = pos=(16,25.825,-16) rot=(1,0,0;1.5708rad)
  LinkedObject = -> Screw001
  Placement = pos=(16,25.825,-16) rot=(1,0,0;1.5708rad)
  _LinkVersion = 1
FEATURE [App::LinkElement] Link012_i3
  LinkPlacement = pos=(-16,25.825,-16) rot=(1,0,0;1.5708rad)
  LinkedObject = -> Screw001
  Placement = pos=(-16,25.825,-16) rot=(1,0,0;1.5708rad)
  _LinkVersion = 1
FEATURE [App::Link] Link012  label="M5x20-4-Screws"
  AutoLinkLabel = true
  AutoPlacement = true
  ElementCount = 4
  ElementList = -> [Link012_i0,Link012_i1,Link012_i2,Link012_i3]
  LinkPlacement = pos=(0,-34,0) rot=(0,0,1;0rad)
  LinkedObject = -> Screw001
  Placement = pos=(0,-34,0) rot=(0,0,1;0rad)
  SyncGroupVisibility = false
  _LinkVersion = 1
FEATURE [Part::FeaturePython] Parts005  # WARN: FeaturePython — macro-defined, semantics opaque (R4)
  Group = -> [Link005,Link006,Link011,Link012]
  GroupMode = 0
  _LinkVersion = 1
FEATURE [Part::FeaturePython] Screw003  label="M5x20-Screw001"  # Fasteners workbench fastener (typed FeaturePython)
  diameter = 6
  invert = false
  length = 5
  lengthCustom = 20
  matchOuter = false
  offset = 0
  thread = false
  type = 33
FEATURE [Sketcher::SketchObject] Sketch026
  ExternalGeometry = -> [Pocket011]
  FullyConstrained = true
  MapMode = 5
  Placement = pos=(-26,0,0) rot=(0.57735,-0.57735,-0.57735;2.0944rad)
  Support = -> [Pocket011]
  sketch-geometry (2):
    g0: Circle CenterX=9.525 CenterY=0 CenterZ=0 NormalX=0 NormalY=0 NormalZ=1 AngleXU=0 Radius=2.5
    g1: GeomPoint [constr] X=19.05 Y=0 Z=0
  constraints (4):
    c: PointOnObject(g0,g-1)
    c: Diameter(g0) = 5
    c: PointOnObject(g1,g-3)
    c: Symmetric(g1,g-1,g0)
FEATURE [PartDesign::Pocket] Pocket012
  BaseFeature = -> Pocket011
  ClaimChildren = false
  Fit = 0
  FitJoin = 0
  InnerFit = 0
  InnerFitJoin = 0
  InnerTaperAngle = 0
  InnerTaperAngleRev = 0
  Length = 20
  Length2 = 100
  Linearize = true
  NewSolid = false
  Profile = -> Sketch026
  Refine = true
  Suppress = false
  Type = 0
  _ProfileBasedVersion = 1
FEATURE [PartDesign::Body] Body001  label="Right plate"
  AutoGroupSolids = false
  ExportMode = 0
  Group = -> [ShapeBinder,Pad001,Sketch003,Hole002,Sketch004,Hole003,Sketch014,Hole004,Sketch021,Pocket011,Sketch026,Pocket012]
  Origin = -> Origin001
  Placement = pos=(0,407,0) rot=(0,0,1;0rad)
  Tip = -> Pocket012
  _ExportChildren = -> [Pad001,Hole002,Hole003,Hole004,Pocket011,Pocket012]
  _GroupVersion = 1
FEATURE [Sketcher::SketchObject] Sketch027
  ExternalGeometry = -> [Pocket010]
  FullyConstrained = true
  MapMode = 5
  Placement = pos=(-26,0,0) rot=(0.707107,0,-0.707107;3.14159rad)
  Support = -> [Pocket010]
  sketch-geometry (2):
    g0: GeomPoint [constr] X=0 Y=-19.05 Z=0
    g1: Circle CenterX=0 CenterY=-9.525 CenterZ=0 NormalX=0 NormalY=0 NormalZ=1 AngleXU=0 Radius=2.5
  constraints (4):
    c: PointOnObject(g0,g-3)
    c: PointOnObject(g0,g-2)
    c: Diameter(g1) = 5
    c: Symmetric(g-1,g0,g1)
FEATURE [PartDesign::Pocket] Pocket013
  BaseFeature = -> Pocket010
  ClaimChildren = false
  Fit = 0
  FitJoin = 0
  InnerFit = 0
  InnerFitJoin = 0
  InnerTaperAngle = 0
  InnerTaperAngleRev = 0
  Length = 20
  Length2 = 100
  Linearize = true
  NewSolid = false
  Placement = pos=(0,0,0) rot=(1,0,0;1.5708rad)
  Profile = -> Sketch027
  Refine = true
  Suppress = false
  Type = 0
  _ProfileBasedVersion = 1
FEATURE [Part::FeaturePython] Screw004  label="1/4inx1in-Screw001"  # Fasteners workbench fastener (typed FeaturePython)
  diameter = 1
  invert = false
  length = 2
  lengthCustom = 25.4
  matchOuter = false
  offset = 0
  thread = false
  type = 0
FEATURE [Part::FeaturePython] Washer  label="1/4in-Washer"  # Fasteners workbench fastener (typed FeaturePython)
  diameter = 11
  invert = false
  matchOuter = false
  offset = 0
  type = 1
FEATURE [Part::FeaturePython] Nut  label="1/4in-Nut"  # Fasteners workbench fastener (typed FeaturePython)
  diameter = 11
  invert = false
  matchOuter = false
  offset = 0
  thread = false
  type = 0
FEATURE [App::Link] Link013  label="1/4inx1in-Screw  "
  AutoLinkLabel = true
  AutoPlacement = true
  LinkPlacement = pos=(-41.4,244.475,0) rot=(-0.57735,0.57735,0.57735;4.18879rad)
  LinkedObject = -> Screw004
  Placement = pos=(-41.4,244.475,0) rot=(-0.57735,0.57735,0.57735;4.18879rad)
  SyncGroupVisibility = false
  _LinkVersion = 1
FEATURE [App::Link] Link014  label="1/4in-Washer "
  AutoLinkLabel = true
  AutoPlacement = true
  LinkPlacement = pos=(-26,244.475,0) rot=(-0.57735,0.57735,0.57735;4.18879rad)
  LinkedObject = -> Washer
  Placement = pos=(-26,244.475,0) rot=(-0.57735,0.57735,0.57735;4.18879rad)
  SyncGroupVisibility = false
  _LinkVersion = 1
FEATURE [App::Link] Link015  label="1/4in-Nut  "
  AutoLinkLabel = true
  AutoPlacement = true
  LinkPlacement = pos=(-27.6002,244.475,0) rot=(-0.57735,0.57735,0.57735;4.18879rad)
  LinkedObject = -> Nut
  Placement = pos=(-27.6002,244.475,0) rot=(-0.57735,0.57735,0.57735;4.18879rad)
  SyncGroupVisibility = false
  _LinkVersion = 1
FEATURE [Part::FeaturePython] Parts  # WARN: FeaturePython — macro-defined, semantics opaque (R4)
  Group = -> [Link001,Link009,Link010,Link013,Link014,Link015]
  GroupMode = 0
  _LinkVersion = 1
FEATURE [App::Link] Link016  label="1/4inx1in-Screw    "
  AutoLinkLabel = true
  AutoPlacement = true
  LinkPlacement = pos=(-41.4,9.525,-4.7e-15) rot=(0.707107,0,-0.707107;3.14159rad)
  LinkedObject = -> Screw004
  Placement = pos=(-41.4,9.525,-4.7e-15) rot=(0.707107,0,-0.707107;3.14159rad)
  SyncGroupVisibility = false
  _LinkVersion = 1
FEATURE [App::Link] Link017  label="1/4in-Washer  "
  AutoLinkLabel = true
  AutoPlacement = true
  LinkPlacement = pos=(-26,9.525,2.1e-15) rot=(0.707107,0,-0.707107;3.14159rad)
  LinkedObject = -> Washer
  Placement = pos=(-26,9.525,2.1e-15) rot=(0.707107,0,-0.707107;3.14159rad)
  SyncGroupVisibility = false
  _LinkVersion = 1
FEATURE [App::Link] Link018  label="1/4in-Nut    "
  AutoLinkLabel = true
  AutoPlacement = true
  LinkPlacement = pos=(-27.6002,9.525,2.1e-15) rot=(0.707107,0,-0.707107;3.14159rad)
  LinkedObject = -> Nut
  Placement = pos=(-27.6002,9.525,2.1e-15) rot=(0.707107,0,-0.707107;3.14159rad)
  SyncGroupVisibility = false
  _LinkVersion = 1
FEATURE [Part::FeaturePython] Parts001  # WARN: FeaturePython — macro-defined, semantics opaque (R4)
  Group = -> [Link,Link007,Link008,Link016,Link018,Link017]
  GroupMode = 0
  _LinkVersion = 1
FEATURE [Sketcher::SketchObject] Sketch028
  ExternalGeometry = -> [Pocket013]
  FullyConstrained = true
  MapMode = 5
  Placement = pos=(0,19.05,4.2e-15) rot=(-1,0,0;1.5708rad)
  Support = -> [Pocket013]
  sketch-geometry (5):
    g0: Circle CenterX=-13 CenterY=-234.7 CenterZ=0 NormalX=0 NormalY=0 NormalZ=1 AngleXU=0 Radius=1.25
    g1: Circle CenterX=-13 CenterY=-222.7 CenterZ=0 NormalX=0 NormalY=0 NormalZ=1 AngleXU=0 Radius=1.25
    g2: Circle CenterX=-27 CenterY=-228.7 CenterZ=0 NormalX=0 NormalY=0 NormalZ=1 AngleXU=0 Radius=3.2
    g3: LineSegment [constr] StartX=-27 StartY=-228.7 StartZ=0 EndX=-13 EndY=-222.7 EndZ=0
    g4: LineSegment [constr] StartX=-27 StartY=-228.7 StartZ=0 EndX=-13 EndY=-234.7 EndZ=0
  constraints (13):
    c: Equal(g1,g0)
    c: Vertical(g0,g1)
    c: DistanceY(g0,g1) = 12
    c: Diameter(g1) = 2.5
    c: DistanceY(g-3,g0) = 42
    c: DistanceX(g-3,g0) = 71
    c: Diameter(g2) = 6.4
    c: DistanceX(g2,g0) = 14
    c: Coincident(g3,g2)
    c: Coincident(g3,g1)
    c: Coincident(g4,g2)
    c: Coincident(g4,g0)
    c: Equal(g4,g3)
FEATURE [PartDesign::Pocket] Pocket014
  BaseFeature = -> Pocket013
  ClaimChildren = false
  Fit = 0
  FitJoin = 0
  InnerFit = 0
  InnerFitJoin = 0
  InnerTaperAngle = 0
  InnerTaperAngleRev = 0
  Length = 5
  Length2 = 100
  Linearize = true
  NewSolid = false
  Placement = pos=(0,0,0) rot=(1,0,0;1.5708rad)
  Profile = -> Sketch028
  Refine = true
  Suppress = false
  Type = 1
  _ProfileBasedVersion = 1
FEATURE [PartDesign::Body] Body  label="Left plate"
  AutoGroupSolids = false
  ExportMode = 0
  Group = -> [Sketch,Pad,Sketch001,Hole,Sketch002,Hole001,Sketch005,Pocket,Sketch015,Hole005,Sketch022,Pocket010,Sketch027,Pocket013,Sketch028,Pocket014]
  Origin = -> Origin
  Placement = pos=(0,-256,0) rot=(0,0,1;0rad)
  Tip = -> Pocket014
  _ExportChildren = -> [Pad,Hole,Hole001,Pocket,Hole005,Pocket010,Pocket013,Pocket014]
  _GroupVersion = 1
FEATURE [App::DocumentObjectGroup] Group  label="Components"
  ExportMode = 1
  Group = -> [Body001,Body,Body002,Body005,Body006,Screw,Screw001,Screw002,Screw003,Screw004,Washer,Nut]
  _GroupVersion = 1
FEATURE [TechDraw::DrawSVGTemplate] Template
  EditableTexts = Code=Code; DrawingNumber=Drawing Number; DrawingTitle1=Gouverner plate; DrawingTitle2=Count: 2; DrawingTitle3=Material: 1/4" Aluminum; DrawnBy=Andrew <owner>; Revision=V.1.0; Scale=Scale 1:1; Sheet=Sheet 1 of 1
  Height = 215.9
  Orientation = 1
  Width = 279.4
FEATURE [TechDraw::DrawViewPart] View  label="Gouverner plate front"
  CoarseView = false
  Direction = (0,-1,0)
  Focus = 100
  HardHidden = false
  IsoCount = 0
  IsoHidden = false
  IsoVisible = false
  LockPosition = false
  Perspective = false
  Rotation = 0
  ScaleType = 0
  SeamHidden = false
  SeamVisible = true
  SmoothHidden = false
  SmoothVisible = true
  Source = -> [Body006]
  X = 84.019
  XDirection = (1,0,0)
  Y = 129.726
FEATURE [TechDraw::DrawViewDimension] Dimension
  Arbitrary = false
  ArbitraryTolerances = false
  EqualTolerance = true
  FormatSpec = %.2f
  FormatSpecOverTolerance = %+.2f
  FormatSpecUnderTolerance = %+.2f
  Inverted = false
  LockPosition = false
  MeasureType = 1
  OverTolerance = 0
  References2D = -> [View]
  Rotation = 0
  ScaleType = 0
  TheoreticalExact = false
  Type = 2
  UnderTolerance = 0
  X = -42.0565
  Y = 1.7228
FEATURE [TechDraw::DrawViewDimension] Dimension001
  Arbitrary = false
  ArbitraryTolerances = false
  EqualTolerance = true
  FormatSpec = %.2f
  FormatSpecOverTolerance = %+.2f
  FormatSpecUnderTolerance = %+.2f
  Inverted = false
  LockPosition = false
  MeasureType = 1
  OverTolerance = 0
  References2D = -> [View]
  Rotation = 0
  ScaleType = 0
  TheoreticalExact = false
  Type = 1
  UnderTolerance = 0
  X = 0.765691
  Y = 64.0481
FEATURE [TechDraw::DrawViewDimension] Dimension002
  Arbitrary = false
  ArbitraryTolerances = false
  EqualTolerance = true
  FormatSpec = %.2f
  FormatSpecOverTolerance = %+.2f
  FormatSpecUnderTolerance = %+.2f
  Inverted = false
  LockPosition = false
  MeasureType = 1
  OverTolerance = 0
  References2D = -> [View]
  Rotation = 0
  ScaleType = 0
  TheoreticalExact = false
  Type = 1
  UnderTolerance = 0
  X = -0.191423
  Y = 58.091
FEATURE [TechDraw::DrawViewDimension] Dimension003
  Arbitrary = false
  ArbitraryTolerances = false
  EqualTolerance = true
  FormatSpec = %.2f
  FormatSpecOverTolerance = %+.2f
  FormatSpecUnderTolerance = %+.2f
  Inverted = false
  LockPosition = false
  MeasureType = 1
  OverTolerance = 0
  References2D = -> [View]
  Rotation = 0
  ScaleType = 0
  TheoreticalExact = false
  Type = 2
  UnderTolerance = 0
  X = 33.8023
  Y = 32.5199
FEATURE [TechDraw::DrawViewDimension] Dimension004
  Arbitrary = false
  ArbitraryTolerances = false
  EqualTolerance = true
  FormatSpec = %.2f
  FormatSpecOverTolerance = %+.2f
  FormatSpecUnderTolerance = %+.2f
  Inverted = false
  LockPosition = false
  MeasureType = 1
  OverTolerance = 0
  References2D = -> [View]
  Rotation = 0
  ScaleType = 0
  TheoreticalExact = false
  Type = 2
  UnderTolerance = 0
  X = 27.114
  Y = 58.0283
FEATURE [TechDraw::DrawViewDimension] Dimension005
  Arbitrary = false
  ArbitraryTolerances = false
  EqualTolerance = true
  FormatSpec = %.2f
  FormatSpecOverTolerance = %+.2f
  FormatSpecUnderTolerance = %+.2f
  Inverted = false
  LockPosition = false
  MeasureType = 1
  OverTolerance = 0
  References2D = -> [View]
  Rotation = 0
  ScaleType = 0
  TheoreticalExact = false
  Type = 1
  UnderTolerance = 0
  X = 2.29707
  Y = -63.8337
FEATURE [TechDraw::DrawViewDimension] Dimension006
  Arbitrary = false
  ArbitraryTolerances = false
  EqualTolerance = true
  FormatSpec = %.2f
  FormatSpecOverTolerance = %+.2f
  FormatSpecUnderTolerance = %+.2f
  Inverted = false
  LockPosition = false
  MeasureType = 1
  OverTolerance = 0
  References2D = -> [View]
  Rotation = 0
  ScaleType = 0
  TheoreticalExact = false
  Type = 2
  UnderTolerance = 0
  X = 33.868
  Y = -18.9863
FEATURE [TechDraw::DrawViewDimension] Dimension007
  Arbitrary = false
  ArbitraryTolerances = false
  EqualTolerance = true
  FormatSpec = %.2f
  FormatSpecOverTolerance = %+.2f
  FormatSpecUnderTolerance = %+.2f
  Inverted = false
  LockPosition = false
  MeasureType = 1
  OverTolerance = 0
  References2D = -> [View]
  Rotation = 0
  ScaleType = 0
  TheoreticalExact = false
  Type = 2
  UnderTolerance = 0
  X = 33.8621
  Y = 7.44561
FEATURE [TechDraw::DrawViewPart] View001  label="Gouverner plate iso"
  CoarseView = false
  Direction = (0.41,-0.709,0.574)
  Focus = 100
  HardHidden = false
  IsoCount = 0
  IsoHidden = false
  IsoVisible = false
  LockPosition = false
  Perspective = false
  Rotation = 0
  ScaleType = 0
  SeamHidden = false
  SeamVisible = true
  SmoothHidden = false
  SmoothVisible = true
  Source = -> [Body006]
  X = 208.401
  XDirection = (0.866,0.5,0)
  Y = 128.821
FEATURE [TechDraw::DrawViewDimension] Dimension008
  Arbitrary = false
  ArbitraryTolerances = false
  EqualTolerance = true
  FormatSpec = 8x ⌀%.2f
  FormatSpecOverTolerance = %+.2f
  FormatSpecUnderTolerance = %+.2f
  Inverted = false
  LockPosition = false
  MeasureType = 1
  OverTolerance = 0
  References2D = -> [View]
  Rotation = 0
  ScaleType = 0
  TheoreticalExact = false
  Type = 5
  UnderTolerance = 0
  X = -5.87141
  Y = 30.6152
FEATURE [TechDraw::DrawPage] Page  label="Gouverner plate"
  KeepUpdated = true
  NextBalloonIndex = 1
  ProjectionType = 0
  Template = -> Template
  Views = -> [View,Dimension,Dimension001,Dimension002,Dimension003,Dimension004,Dimension005,Dimension006,Dimension007,View001,Dimension008]
FEATURE [TechDraw::DrawSVGTemplate] Template001
  EditableTexts = DrawingTitle1=Left gantry plate; DrawingTitle2=Count: 1; DrawingTitle3=Material: 3/4" Aluminum; DrawnBy=Andrew <owner>; Revision=V.1.0; Scale=Scale 3:1; Sheet=Sheet 1 of 1
  Height = 215.9
  Orientation = 1
  Width = 279.4
FEATURE [TechDraw::DrawViewPart] View002  label="Left plate side"
  CoarseView = false
  Direction = (0,-1,0)
  Focus = 100
  HardHidden = false
  IsoCount = 0
  IsoHidden = false
  IsoVisible = false
  LockPosition = false
  Perspective = false
  Rotation = 0
  Scale = 0.33
  ScaleType = 0
  SeamHidden = false
  SeamVisible = true
  SmoothHidden = false
  SmoothVisible = true
  Source = -> [Body]
  X = 103.962
  XDirection = (0,0,-1)
  Y = 136.413
FEATURE [TechDraw::DrawViewDimension] Dimension011
  Arbitrary = false
  ArbitraryTolerances = false
  EqualTolerance = true
  FormatSpec = %.2f
  FormatSpecOverTolerance = %+.2f
  FormatSpecUnderTolerance = %+.2f
  Inverted = false
  LockPosition = false
  MeasureType = 1
  OverTolerance = 0
  References2D = -> [View002]
  Rotation = 0
  ScaleType = 0
  TheoreticalExact = false
  Type = 2
  UnderTolerance = 0
  X = -72.308
  Y = -29.2508
FEATURE [TechDraw::DrawViewDimension] Dimension012
  Arbitrary = false
  ArbitraryTolerances = false
  EqualTolerance = true
  FormatSpec = %.2f
  FormatSpecOverTolerance = %+.2f
  FormatSpecUnderTolerance = %+.2f
  Inverted = false
  LockPosition = false
  MeasureType = 1
  OverTolerance = 0
  References2D = -> [View002]
  Rotation = 0
  ScaleType = 0
  TheoreticalExact = false
  Type = 1
  UnderTolerance = 0
  X = 0.60675
  Y = -64.1337
FEATURE [TechDraw::DrawViewDimension] Dimension013
  Arbitrary = false
  ArbitraryTolerances = false
  EqualTolerance = true
  FormatSpec = %.2f
  FormatSpecOverTolerance = %+.2f
  FormatSpecUnderTolerance = %+.2f
  Inverted = false
  LockPosition = false
  MeasureType = 1
  OverTolerance = 0
  References2D = -> [View002]
  Rotation = 0
  ScaleType = 0
  TheoreticalExact = false
  Type = 1
  UnderTolerance = 0
  X = -62.185
  Y = -43.5764
FEATURE [TechDraw::DrawViewDimension] Dimension014
  Arbitrary = false
  ArbitraryTolerances = false
  EqualTolerance = true
  FormatSpec = %.2f
  FormatSpecOverTolerance = %+.2f
  FormatSpecUnderTolerance = %+.2f
  Inverted = false
  LockPosition = false
  MeasureType = 1
  OverTolerance = 0
  References2D = -> [View002]
  Rotation = 0
  ScaleType = 0
  TheoreticalExact = false
  Type = 1
  UnderTolerance = 0
  X = -62.5068
  Y = -50.1957
FEATURE [TechDraw::DrawViewDimension] Dimension015
  Arbitrary = false
  ArbitraryTolerances = false
  EqualTolerance = true
  FormatSpec = %.2f
  FormatSpecOverTolerance = %+.2f
  FormatSpecUnderTolerance = %+.2f
  Inverted = false
  LockPosition = false
  MeasureType = 1
  OverTolerance = 0
  References2D = -> [View002]
  Rotation = 0
  ScaleType = 0
  TheoreticalExact = false
  Type = 1
  UnderTolerance = 0
  X = -34.2085
  Y = -57.7743
FEATURE [TechDraw::DrawViewDimension] Dimension016
  Arbitrary = false
  ArbitraryTolerances = false
  EqualTolerance = true
  FormatSpec = %.2f
  FormatSpecOverTolerance = %+.2f
  FormatSpecUnderTolerance = %+.2f
  Inverted = false
  LockPosition = false
  MeasureType = 1
  OverTolerance = 0
  References2D = -> [View002]
  Rotation = 0
  ScaleType = 0
  TheoreticalExact = false
  Type = 2
  UnderTolerance = 0
  X = -56.2777
  Y = -29.9553
FEATURE [TechDraw::DrawViewDimension] Dimension017
  Arbitrary = false
  ArbitraryTolerances = false
  EqualTolerance = true
  FormatSpec = %.2f
  FormatSpecOverTolerance = %+.2f
  FormatSpecUnderTolerance = %+.2f
  Inverted = false
  LockPosition = false
  MeasureType = 1
  OverTolerance = 0
  References2D = -> [View002]
  Rotation = 0
  ScaleType = 0
  TheoreticalExact = false
  Type = 1
  UnderTolerance = 0
  X = 41.3655
  Y = 58.6854
FEATURE [TechDraw::DrawViewDimension] Dimension018
  Arbitrary = false
  ArbitraryTolerances = false
  EqualTolerance = true
  FormatSpec = %.2f
  FormatSpecOverTolerance = %+.2f
  FormatSpecUnderTolerance = %+.2f
  Inverted = false
  LockPosition = false
  MeasureType = 1
  OverTolerance = 0
  References2D = -> [View002]
  Rotation = 0
  ScaleType = 0
  TheoreticalExact = false
  Type = 1
  UnderTolerance = 0
  X = 41.8409
  Y = 52.9325
FEATURE [TechDraw::DrawViewDimension] Dimension019
  Arbitrary = false
  ArbitraryTolerances = false
  EqualTolerance = true
  FormatSpec = %.2f
  FormatSpecOverTolerance = %+.2f
  FormatSpecUnderTolerance = %+.2f
  Inverted = false
  LockPosition = false
  MeasureType = 1
  OverTolerance = 0
  References2D = -> [View002]
  Rotation = 0
  ScaleType = 0
  TheoreticalExact = false
  Type = 1
  UnderTolerance = 0
  X = 57.1577
  Y = 49.2675
FEATURE [TechDraw::DrawViewDimension] Dimension020
  Arbitrary = false
  ArbitraryTolerances = false
  EqualTolerance = true
  FormatSpec = %.2f
  FormatSpecOverTolerance = %+.2f
  FormatSpecUnderTolerance = %+.2f
  Inverted = false
  LockPosition = false
  MeasureType = 1
  OverTolerance = 0
  References2D = -> [View002]
  Rotation = 0
  ScaleType = 0
  TheoreticalExact = false
  Type = 1
  UnderTolerance = 0
  X = 41.3655
  Y = -30.4801
FEATURE [TechDraw::DrawViewDimension] Dimension021
  Arbitrary = false
  ArbitraryTolerances = false
  EqualTolerance = true
  FormatSpec = %.2f
  FormatSpecOverTolerance = %+.2f
  FormatSpecUnderTolerance = %+.2f
  Inverted = false
  LockPosition = false
  MeasureType = 1
  OverTolerance = 0
  References2D = -> [View002]
  Rotation = 0
  ScaleType = 0
  TheoreticalExact = false
  Type = 1
  UnderTolerance = 0
  X = 30.2995
  Y = -45.8827
FEATURE [TechDraw::DrawViewDimension] Dimension022
  Arbitrary = false
  ArbitraryTolerances = false
  EqualTolerance = true
  FormatSpec = %.2f
  FormatSpecOverTolerance = %+.2f
  FormatSpecUnderTolerance = %+.2f
  Inverted = false
  LockPosition = false
  MeasureType = 1
  OverTolerance = 0
  References2D = -> [View002]
  Rotation = 0
  ScaleType = 0
  TheoreticalExact = false
  Type = 2
  UnderTolerance = 0
  X = 73.2335
  Y = -32.5772
FEATURE [TechDraw::DrawViewDimension] Dimension023
  Arbitrary = false
  ArbitraryTolerances = false
  EqualTolerance = true
  FormatSpec = %.2f
  FormatSpecOverTolerance = %+.2f
  FormatSpecUnderTolerance = %+.2f
  Inverted = false
  LockPosition = false
  MeasureType = 1
  OverTolerance = 0
  References2D = -> [View002]
  Rotation = 0
  ScaleType = 0
  TheoreticalExact = false
  Type = 2
  UnderTolerance = 0
  X = 51.936
  Y = -26.4254
FEATURE [TechDraw::DrawViewDimension] Dimension024
  Arbitrary = false
  ArbitraryTolerances = false
  EqualTolerance = true
  FormatSpec = %.2f
  FormatSpecOverTolerance = %+.2f
  FormatSpecUnderTolerance = %+.2f
  Inverted = false
  LockPosition = false
  MeasureType = 1
  OverTolerance = 0
  References2D = -> [View002]
  Rotation = 0
  ScaleType = 0
  TheoreticalExact = false
  Type = 2
  UnderTolerance = 0
  X = 73.3468
  Y = 9.67679
FEATURE [TechDraw::DrawViewDimension] Dimension025
  Arbitrary = false
  ArbitraryTolerances = false
  EqualTolerance = true
  FormatSpec = %.2f
  FormatSpecOverTolerance = %+.2f
  FormatSpecUnderTolerance = %+.2f
  Inverted = false
  LockPosition = false
  MeasureType = 1
  OverTolerance = 0
  References2D = -> [View002]
  Rotation = 0
  ScaleType = 0
  TheoreticalExact = false
  Type = 2
  UnderTolerance = 0
  X = 57.2563
  Y = 11.1475
FEATURE [TechDraw::DrawViewDimension] Dimension026
  Arbitrary = false
  ArbitraryTolerances = false
  EqualTolerance = true
  FormatSpec = %.2f
  FormatSpecOverTolerance = %+.2f
  FormatSpecUnderTolerance = %+.2f
  Inverted = false
  LockPosition = false
  MeasureType = 1
  OverTolerance = 0
  References2D = -> [View002]
  Rotation = 0
  ScaleType = 0
  TheoreticalExact = false
  Type = 2
  UnderTolerance = 0
  X = 57.3776
  Y = -12.4911
FEATURE [TechDraw::DrawViewDimension] Dimension027
  Arbitrary = false
  ArbitraryTolerances = false
  EqualTolerance = true
  FormatSpec = %.2f
  FormatSpecOverTolerance = %+.2f
  FormatSpecUnderTolerance = %+.2f
  Inverted = false
  LockPosition = false
  MeasureType = 1
  OverTolerance = 0
  References2D = -> [View002]
  Rotation = 0
  ScaleType = 0
  TheoreticalExact = false
  Type = 2
  UnderTolerance = 0
  X = 57.2562
  Y = -0.766498
FEATURE [TechDraw::DrawViewDimension] Dimension028
  Arbitrary = false
  ArbitraryTolerances = false
  EqualTolerance = true
  FormatSpec = %.2f
  FormatSpecOverTolerance = %+.2f
  FormatSpecUnderTolerance = %+.2f
  Inverted = false
  LockPosition = false
  MeasureType = 1
  OverTolerance = 0
  References2D = -> [View002]
  Rotation = 0
  ScaleType = 0
  TheoreticalExact = false
  Type = 1
  UnderTolerance = 0
  X = 42.0255
  Y = 1.74165
FEATURE [TechDraw::DrawViewDimension] Dimension029
  Arbitrary = false
  ArbitraryTolerances = false
  EqualTolerance = true
  FormatSpec = %.2f
  FormatSpecOverTolerance = %+.2f
  FormatSpecUnderTolerance = %+.2f
  Inverted = false
  LockPosition = false
  MeasureType = 1
  OverTolerance = 0
  References2D = -> [View002]
  Rotation = 0
  ScaleType = 0
  TheoreticalExact = false
  Type = 2
  UnderTolerance = 0
  X = 57.2659
  Y = 22.518
FEATURE [TechDraw::DrawViewDimension] Dimension030
  Arbitrary = false
  ArbitraryTolerances = false
  EqualTolerance = true
  FormatSpec = %.2f
  FormatSpecOverTolerance = %+.2f
  FormatSpecUnderTolerance = %+.2f
  Inverted = false
  LockPosition = false
  MeasureType = 1
  OverTolerance = 0
  References2D = -> [View002]
  Rotation = 0
  ScaleType = 0
  TheoreticalExact = false
  Type = 2
  UnderTolerance = 0
  X = 64.9205
  Y = 35.8573
FEATURE [TechDraw::DrawViewDimension] Dimension031
  Arbitrary = false
  ArbitraryTolerances = false
  EqualTolerance = true
  FormatSpec = %.2f
  FormatSpecOverTolerance = %+.2f
  FormatSpecUnderTolerance = %+.2f
  Inverted = false
  LockPosition = false
  MeasureType = 1
  OverTolerance = 0
  References2D = -> [View002]
  Rotation = 0
  ScaleType = 0
  TheoreticalExact = false
  Type = 1
  UnderTolerance = 0
  X = -41.1483
  Y = -11.2409
FEATURE [TechDraw::DrawViewDimension] Dimension032
  Arbitrary = false
  ArbitraryTolerances = false
  EqualTolerance = true
  FormatSpec = %.2f
  FormatSpecOverTolerance = %+.2f
  FormatSpecUnderTolerance = %+.2f
  Inverted = false
  LockPosition = false
  MeasureType = 1
  OverTolerance = 0
  References2D = -> [View002]
  Rotation = 0
  ScaleType = 0
  TheoreticalExact = false
  Type = 1
  UnderTolerance = 0
  X = -23.589
  Y = -2.25623
FEATURE [TechDraw::DrawViewDimension] Dimension033
  Arbitrary = false
  ArbitraryTolerances = false
  EqualTolerance = true
  FormatSpec = %.2f
  FormatSpecOverTolerance = %+.2f
  FormatSpecUnderTolerance = %+.2f
  Inverted = false
  LockPosition = false
  MeasureType = 1
  OverTolerance = 0
  References2D = -> [View002]
  Rotation = 0
  ScaleType = 0
  TheoreticalExact = false
  Type = 2
  UnderTolerance = 0
  X = -54.6352
  Y = -17.6034
FEATURE [TechDraw::DrawViewDimension] Dimension034
  Arbitrary = false
  ArbitraryTolerances = false
  EqualTolerance = true
  FormatSpec = %.2f
  FormatSpecOverTolerance = %+.2f
  FormatSpecUnderTolerance = %+.2f
  Inverted = false
  LockPosition = false
  MeasureType = 1
  OverTolerance = 0
  References2D = -> [View002]
  Rotation = 0
  ScaleType = 0
  TheoreticalExact = false
  Type = 2
  UnderTolerance = 0
  X = -12.2796
  Y = -33.2372
FEATURE [TechDraw::DrawViewDimension] Dimension035
  Arbitrary = false
  ArbitraryTolerances = false
  EqualTolerance = true
  FormatSpec = %.2f
  FormatSpecOverTolerance = %+.2f
  FormatSpecUnderTolerance = %+.2f
  Inverted = false
  LockPosition = false
  MeasureType = 1
  OverTolerance = 0
  References2D = -> [View002]
  Rotation = 0
  ScaleType = 0
  TheoreticalExact = false
  Type = 2
  UnderTolerance = 0
  X = -27.893
  Y = -49.0614
FEATURE [TechDraw::DrawViewDimension] Dimension036
  Arbitrary = false
  ArbitraryTolerances = false
  EqualTolerance = true
  FormatSpec = 9x ⌀%.2f
  FormatSpecOverTolerance = %+.2f
  FormatSpecUnderTolerance = %+.2f
  Inverted = false
  LockPosition = false
  MeasureType = 1
  OverTolerance = 0
  References2D = -> [View002]
  Rotation = 0
  ScaleType = 0
  TheoreticalExact = false
  Type = 5
  UnderTolerance = 0
  X = 5.8147
  Y = -16.18
FEATURE [TechDraw::DrawViewDimension] Dimension037
  Arbitrary = false
  ArbitraryTolerances = false
  EqualTolerance = true
  FormatSpec = 9x ⌀%.2f ↓8.0
  FormatSpecOverTolerance = %+.2f
  FormatSpecUnderTolerance = %+.2f
  Inverted = false
  LockPosition = false
  MeasureType = 1
  OverTolerance = 0
  References2D = -> [View002]
  Rotation = 0
  ScaleType = 0
  TheoreticalExact = false
  Type = 5
  UnderTolerance = 0
  X = 19.5509
  Y = -17.1913
FEATURE [TechDraw::DrawViewDimension] Dimension038
  Arbitrary = true
  ArbitraryTolerances = false
  EqualTolerance = true
  FormatSpec = 4x M5
  FormatSpecOverTolerance = %+.2f
  FormatSpecUnderTolerance = %+.2f
  Inverted = false
  LockPosition = false
  MeasureType = 1
  OverTolerance = 0
  References2D = -> [View002]
  Rotation = 0
  ScaleType = 0
  TheoreticalExact = false
  Type = 4
  UnderTolerance = 0
  X = -7.41584
  Y = -10.1125
FEATURE [TechDraw::DrawViewDimension] Dimension039
  Arbitrary = false
  ArbitraryTolerances = false
  EqualTolerance = true
  FormatSpec = ⌀%.2f
  FormatSpecOverTolerance = %+.2f
  FormatSpecUnderTolerance = %+.2f
  Inverted = false
  LockPosition = false
  MeasureType = 1
  OverTolerance = 0
  References2D = -> [View002]
  Rotation = 0
  ScaleType = 0
  TheoreticalExact = false
  Type = 5
  UnderTolerance = 0
  X = -7.50011
  Y = -18.961
FEATURE [TechDraw::DrawViewDimension] Dimension040
  Arbitrary = false
  ArbitraryTolerances = false
  EqualTolerance = true
  FormatSpec = ⌀%.2f
  FormatSpecOverTolerance = %+.2f
  FormatSpecUnderTolerance = %+.2f
  Inverted = false
  LockPosition = false
  MeasureType = 1
  OverTolerance = 0
  References2D = -> [View002]
  Rotation = 0
  ScaleType = 0
  TheoreticalExact = false
  Type = 5
  UnderTolerance = 0
  X = -22.5846
  Y = -14.5789
FEATURE [TechDraw::DrawViewDimension] Dimension041
  Arbitrary = true
  ArbitraryTolerances = false
  EqualTolerance = true
  FormatSpec = 2x M3
  FormatSpecOverTolerance = %+.2f
  FormatSpecUnderTolerance = %+.2f
  Inverted = false
  LockPosition = false
  MeasureType = 1
  OverTolerance = 0
  References2D = -> [View002]
  Rotation = 0
  ScaleType = 0
  TheoreticalExact = false
  Type = 4
  UnderTolerance = 0
  X = -42.3883
  Y = -19.0452
FEATURE [TechDraw::DrawViewDimension] Dimension042
  Arbitrary = true
  ArbitraryTolerances = false
  EqualTolerance = true
  FormatSpec = 4x M5
  FormatSpecOverTolerance = %+.2f
  FormatSpecUnderTolerance = %+.2f
  Inverted = false
  LockPosition = false
  MeasureType = 1
  OverTolerance = 0
  References2D = -> [View002]
  Rotation = 0
  ScaleType = 0
  TheoreticalExact = false
  Type = 4
  UnderTolerance = 0
  X = 25.071
  Y = 6.31018
FEATURE [TechDraw::DrawViewDimension] Dimension043
  Arbitrary = false
  ArbitraryTolerances = false
  EqualTolerance = true
  FormatSpec = %.2f
  FormatSpecOverTolerance = %+.2f
  FormatSpecUnderTolerance = %+.2f
  Inverted = false
  LockPosition = false
  MeasureType = 1
  OverTolerance = 0
  References2D = -> [View002]
  Rotation = 0
  ScaleType = 0
  TheoreticalExact = false
  Type = 1
  UnderTolerance = 0
  X = -13.8789
  Y = -50.2737
FEATURE [TechDraw::DrawViewDimension] Dimension044
  Arbitrary = false
  ArbitraryTolerances = false
  EqualTolerance = true
  FormatSpec = %.2f
  FormatSpecOverTolerance = %+.2f
  FormatSpecUnderTolerance = %+.2f
  Inverted = false
  LockPosition = false
  MeasureType = 1
  OverTolerance = 0
  References2D = -> [View002]
  Rotation = 0
  ScaleType = 0
  TheoreticalExact = false
  Type = 2
  UnderTolerance = 0
  X = -64.3007
  Y = -29.7139
FEATURE [TechDraw::DrawSVGTemplate] Template002
  EditableTexts = DrawingTitle1=Right gantry plate; DrawingTitle2=Count: 1; DrawingTitle3=Material: 3/4" Aluminum; DrawnBy=Andrew <owner>; Revision=V.1.0; Scale=Scale 3:1; Sheet=Sheet 1 of 1
  Height = 215.9
  Orientation = 1
  Width = 279.4
FEATURE [TechDraw::DrawViewPart] View003  label="Right plate - side"
  CoarseView = false
  Direction = (0,1,0)
  Focus = 100
  HardHidden = false
  IsoCount = 0
  IsoHidden = false
  IsoVisible = false
  LockPosition = false
  Perspective = false
  Rotation = 0
  Scale = 0.33
  ScaleType = 0
  SeamHidden = false
  SeamVisible = true
  SmoothHidden = false
  SmoothVisible = true
  Source = -> [Body001]
  X = 189.586
  XDirection = (0,0,1)
  Y = 139.379
FEATURE [TechDraw::DrawViewPart] View004  label="Right plate - back"
  CoarseView = false
  Direction = (-1,0,0)
  Focus = 100
  HardHidden = false
  IsoCount = 0
  IsoHidden = false
  IsoVisible = false
  LockPosition = false
  Perspective = false
  Rotation = 0
  Scale = 0.33
  ScaleType = 0
  SeamHidden = false
  SeamVisible = true
  SmoothHidden = false
  SmoothVisible = true
  Source = -> [Body001]
  X = 57.8691
  XDirection = (0,-1,0)
  Y = 132.712
FEATURE [TechDraw::DrawViewDimension] Dimension045
  Arbitrary = true
  ArbitraryTolerances = false
  EqualTolerance = true
  FormatSpec = 1/4-20 ↓25.00
  FormatSpecOverTolerance = %+.2f
  FormatSpecUnderTolerance = %+.2f
  Inverted = false
  LockPosition = false
  MeasureType = 1
  OverTolerance = 0
  References2D = -> [View004]
  Rotation = 0
  ScaleType = 0
  TheoreticalExact = false
  Type = 4
  UnderTolerance = 0
  X = 16.3095
  Y = -24.3185
FEATURE [TechDraw::DrawViewDimension] Dimension046
  Arbitrary = false
  ArbitraryTolerances = false
  EqualTolerance = true
  FormatSpec = %.2f
  FormatSpecOverTolerance = %+.2f
  FormatSpecUnderTolerance = %+.2f
  Inverted = false
  LockPosition = false
  MeasureType = 1
  OverTolerance = 0
  References2D = -> [View004]
  Rotation = 0
  ScaleType = 0
  TheoreticalExact = false
  Type = 1
  UnderTolerance = 0
  X = 0.382845
  Y = 58.2824
FEATURE [TechDraw::DrawViewDimension] Dimension047
  Arbitrary = false
  ArbitraryTolerances = false
  EqualTolerance = true
  FormatSpec = %.2f
  FormatSpecOverTolerance = %+.2f
  FormatSpecUnderTolerance = %+.2f
  Inverted = false
  LockPosition = false
  MeasureType = 1
  OverTolerance = 0
  References2D = -> [View003]
  Rotation = 0
  ScaleType = 0
  TheoreticalExact = false
  Type = 2
  UnderTolerance = 0
  X = -74.7447
  Y = 9.95285
FEATURE [TechDraw::DrawViewDimension] Dimension048
  Arbitrary = false
  ArbitraryTolerances = false
  EqualTolerance = true
  FormatSpec = %.2f
  FormatSpecOverTolerance = %+.2f
  FormatSpecUnderTolerance = %+.2f
  Inverted = false
  LockPosition = false
  MeasureType = 1
  OverTolerance = 0
  References2D = -> [View003]
  Rotation = 0
  ScaleType = 0
  TheoreticalExact = false
  Type = 2
  UnderTolerance = 0
  X = -57.8013
  Y = 39.781
FEATURE [TechDraw::DrawViewDimension] Dimension049
  Arbitrary = false
  ArbitraryTolerances = false
  EqualTolerance = true
  FormatSpec = %.2f
  FormatSpecOverTolerance = %+.2f
  FormatSpecUnderTolerance = %+.2f
  Inverted = false
  LockPosition = false
  MeasureType = 1
  OverTolerance = 0
  References2D = -> [View003]
  Rotation = 0
  ScaleType = 0
  TheoreticalExact = false
  Type = 2
  UnderTolerance = 0
  X = -57.7214
  Y = 21.929
FEATURE [TechDraw::DrawViewDimension] Dimension050
  Arbitrary = false
  ArbitraryTolerances = false
  EqualTolerance = true
  FormatSpec = %.2f
  FormatSpecOverTolerance = %+.2f
  FormatSpecUnderTolerance = %+.2f
  Inverted = false
  LockPosition = false
  MeasureType = 1
  OverTolerance = 0
  References2D = -> [View003]
  Rotation = 0
  ScaleType = 0
  TheoreticalExact = false
  Type = 2
  UnderTolerance = 0
  X = -57.7214
  Y = 11.3903
FEATURE [TechDraw::DrawViewDimension] Dimension051
  Arbitrary = false
  ArbitraryTolerances = false
  EqualTolerance = true
  FormatSpec = %.2f
  FormatSpecOverTolerance = %+.2f
  FormatSpecUnderTolerance = %+.2f
  Inverted = false
  LockPosition = false
  MeasureType = 1
  OverTolerance = 0
  References2D = -> [View003]
  Rotation = 0
  ScaleType = 0
  TheoreticalExact = false
  Type = 2
  UnderTolerance = 0
  X = -57.6203
  Y = 0.750379
FEATURE [TechDraw::DrawViewDimension] Dimension052
  Arbitrary = false
  ArbitraryTolerances = false
  EqualTolerance = true
  FormatSpec = %.2f
  FormatSpecOverTolerance = %+.2f
  FormatSpecUnderTolerance = %+.2f
  Inverted = false
  LockPosition = false
  MeasureType = 1
  OverTolerance = 0
  References2D = -> [View003]
  Rotation = 0
  ScaleType = 0
  TheoreticalExact = false
  Type = 2
  UnderTolerance = 0
  X = -57.6203
  Y = -13.0776
FEATURE [TechDraw::DrawViewDimension] Dimension053
  Arbitrary = false
  ArbitraryTolerances = false
  EqualTolerance = true
  FormatSpec = %.2f
  FormatSpecOverTolerance = %+.2f
  FormatSpecUnderTolerance = %+.2f
  Inverted = false
  LockPosition = false
  MeasureType = 1
  OverTolerance = 0
  References2D = -> [View003]
  Rotation = 0
  ScaleType = 0
  TheoreticalExact = false
  Type = 2
  UnderTolerance = 0
  X = -65.689
  Y = -26.6074
FEATURE [TechDraw::DrawViewDimension] Dimension054
  Arbitrary = false
  ArbitraryTolerances = false
  EqualTolerance = true
  FormatSpec = %.2f
  FormatSpecOverTolerance = %+.2f
  FormatSpecUnderTolerance = %+.2f
  Inverted = false
  LockPosition = false
  MeasureType = 1
  OverTolerance = 0
  References2D = -> [View003]
  Rotation = 0
  ScaleType = 0
  TheoreticalExact = false
  Type = 1
  UnderTolerance = 0
  X = -60.0727
  Y = 56.295
FEATURE [TechDraw::DrawViewDimension] Dimension055
  Arbitrary = false
  ArbitraryTolerances = false
  EqualTolerance = true
  FormatSpec = %.2f
  FormatSpecOverTolerance = %+.2f
  FormatSpecUnderTolerance = %+.2f
  Inverted = false
  LockPosition = false
  MeasureType = 1
  OverTolerance = 0
  References2D = -> [View003]
  Rotation = 0
  ScaleType = 0
  TheoreticalExact = false
  Type = 1
  UnderTolerance = 0
  X = -41.5111
  Y = 59.9669
FEATURE [TechDraw::DrawViewDimension] Dimension056
  Arbitrary = false
  ArbitraryTolerances = false
  EqualTolerance = true
  FormatSpec = %.2f
  FormatSpecOverTolerance = %+.2f
  FormatSpecUnderTolerance = %+.2f
  Inverted = false
  LockPosition = false
  MeasureType = 1
  OverTolerance = 0
  References2D = -> [View003]
  Rotation = 0
  ScaleType = 0
  TheoreticalExact = false
  Type = 1
  UnderTolerance = 0
  X = -41.443
  Y = 49.7547
FEATURE [TechDraw::DrawViewDimension] Dimension057
  Arbitrary = false
  ArbitraryTolerances = false
  EqualTolerance = true
  FormatSpec = %.2f
  FormatSpecOverTolerance = %+.2f
  FormatSpecUnderTolerance = %+.2f
  Inverted = false
  LockPosition = false
  MeasureType = 1
  OverTolerance = 0
  References2D = -> [View003]
  Rotation = 0
  ScaleType = 0
  TheoreticalExact = false
  Type = 1
  UnderTolerance = 0
  X = -41.2441
  Y = -25.3184
FEATURE [TechDraw::DrawViewDimension] Dimension058
  Arbitrary = false
  ArbitraryTolerances = false
  EqualTolerance = true
  FormatSpec = %.2f
  FormatSpecOverTolerance = %+.2f
  FormatSpecUnderTolerance = %+.2f
  Inverted = false
  LockPosition = false
  MeasureType = 1
  OverTolerance = 0
  References2D = -> [View003]
  Rotation = 0
  ScaleType = 0
  TheoreticalExact = false
  Type = 1
  UnderTolerance = 0
  X = 22.044
  Y = -61.0523
FEATURE [TechDraw::DrawViewDimension] Dimension059
  Arbitrary = false
  ArbitraryTolerances = false
  EqualTolerance = true
  FormatSpec = %.2f
  FormatSpecOverTolerance = %+.2f
  FormatSpecUnderTolerance = %+.2f
  Inverted = false
  LockPosition = false
  MeasureType = 1
  OverTolerance = 0
  References2D = -> [View003]
  Rotation = 0
  ScaleType = 0
  TheoreticalExact = false
  Type = 2
  UnderTolerance = 0
  X = 59.8138
  Y = -28.149
FEATURE [TechDraw::DrawViewDimension] Dimension060
  Arbitrary = false
  ArbitraryTolerances = false
  EqualTolerance = true
  FormatSpec = %.2f
  FormatSpecOverTolerance = %+.2f
  FormatSpecUnderTolerance = %+.2f
  Inverted = false
  LockPosition = false
  MeasureType = 1
  OverTolerance = 0
  References2D = -> [View003]
  Rotation = 0
  ScaleType = 0
  TheoreticalExact = false
  Type = 1
  UnderTolerance = 0
  X = 57.1378
  Y = -45.2648
FEATURE [TechDraw::DrawViewDimension] Dimension061
  Arbitrary = false
  ArbitraryTolerances = false
  EqualTolerance = true
  FormatSpec = %.2f
  FormatSpecOverTolerance = %+.2f
  FormatSpecUnderTolerance = %+.2f
  Inverted = false
  LockPosition = false
  MeasureType = 1
  OverTolerance = 0
  References2D = -> [View003]
  Rotation = 0
  ScaleType = 0
  TheoreticalExact = false
  Type = 1
  UnderTolerance = 0
  X = 41.1251
  Y = -19.5886
FEATURE [TechDraw::DrawViewDimension] Dimension062
  Arbitrary = false
  ArbitraryTolerances = false
  EqualTolerance = true
  FormatSpec = %.2f
  FormatSpecOverTolerance = %+.2f
  FormatSpecUnderTolerance = %+.2f
  Inverted = false
  LockPosition = false
  MeasureType = 1
  OverTolerance = 0
  References2D = -> [View003]
  Rotation = 0
  ScaleType = 0
  TheoreticalExact = false
  Type = 1
  UnderTolerance = 0
  X = 28.4698
  Y = -52.205
FEATURE [TechDraw::DrawViewDimension] Dimension063
  Arbitrary = false
  ArbitraryTolerances = false
  EqualTolerance = true
  FormatSpec = %.2f
  FormatSpecOverTolerance = %+.2f
  FormatSpecUnderTolerance = %+.2f
  Inverted = false
  LockPosition = false
  MeasureType = 1
  OverTolerance = 0
  References2D = -> [View003]
  Rotation = 0
  ScaleType = 0
  TheoreticalExact = false
  Type = 1
  UnderTolerance = 0
  X = 13.0481
  Y = -52.205
FEATURE [TechDraw::DrawViewDimension] Dimension064
  Arbitrary = false
  ArbitraryTolerances = false
  EqualTolerance = true
  FormatSpec = %.2f
  FormatSpecOverTolerance = %+.2f
  FormatSpecUnderTolerance = %+.2f
  Inverted = false
  LockPosition = false
  MeasureType = 1
  OverTolerance = 0
  References2D = -> [View003]
  Rotation = 0
  ScaleType = 0
  TheoreticalExact = false
  Type = 1
  UnderTolerance = 0
  X = 2.76354
  Y = -11.4797
FEATURE [TechDraw::DrawViewDimension] Dimension065
  Arbitrary = false
  ArbitraryTolerances = false
  EqualTolerance = true
  FormatSpec = %.2f
  FormatSpecOverTolerance = %+.2f
  FormatSpecUnderTolerance = %+.2f
  Inverted = false
  LockPosition = false
  MeasureType = 1
  OverTolerance = 0
  References2D = -> [View003]
  Rotation = 0
  ScaleType = 0
  TheoreticalExact = false
  Type = 2
  UnderTolerance = 0
  X = 28.3535
  Y = -29.9553
FEATURE [TechDraw::DrawViewDimension] Dimension066
  Arbitrary = false
  ArbitraryTolerances = false
  EqualTolerance = true
  FormatSpec = %.2f
  FormatSpecOverTolerance = %+.2f
  FormatSpecUnderTolerance = %+.2f
  Inverted = false
  LockPosition = false
  MeasureType = 1
  OverTolerance = 0
  References2D = -> [View003]
  Rotation = 0
  ScaleType = 0
  TheoreticalExact = false
  Type = 2
  UnderTolerance = 0
  X = -10.9764
  Y = -20.6779
FEATURE [TechDraw::DrawViewDimension] Dimension067
  Arbitrary = false
  ArbitraryTolerances = false
  EqualTolerance = true
  FormatSpec = %.2f
  FormatSpecOverTolerance = %+.2f
  FormatSpecUnderTolerance = %+.2f
  Inverted = false
  LockPosition = false
  MeasureType = 1
  OverTolerance = 0
  References2D = -> [View003]
  Rotation = 0
  ScaleType = 0
  TheoreticalExact = false
  Type = 2
  UnderTolerance = 0
  X = -29.5132
  Y = -32.34
FEATURE [TechDraw::DrawViewDimension] Dimension068
  Arbitrary = true
  ArbitraryTolerances = false
  EqualTolerance = true
  FormatSpec = 4x M5
  FormatSpecOverTolerance = %+.2f
  FormatSpecUnderTolerance = %+.2f
  Inverted = false
  LockPosition = false
  MeasureType = 1
  OverTolerance = 0
  References2D = -> [View003]
  Rotation = 0
  ScaleType = 0
  TheoreticalExact = false
  Type = 4
  UnderTolerance = 0
  X = -28.4484
  Y = 25.5826
FEATURE [TechDraw::DrawViewDimension] Dimension069
  Arbitrary = false
  ArbitraryTolerances = false
  EqualTolerance = true
  FormatSpec = 8x ⌀%.2f
  FormatSpecOverTolerance = %+.2f
  FormatSpecUnderTolerance = %+.2f
  Inverted = false
  LockPosition = false
  MeasureType = 1
  OverTolerance = 0
  References2D = -> [View003]
  Rotation = 0
  ScaleType = 0
  TheoreticalExact = false
  Type = 5
  UnderTolerance = 0
  X = -24.7757
  Y = 3.53938
FEATURE [TechDraw::DrawViewDimension] Dimension070
  Arbitrary = false
  ArbitraryTolerances = false
  EqualTolerance = true
  FormatSpec = 8x ⌀%.2f ↓6.0
  FormatSpecOverTolerance = %+.2f
  FormatSpecUnderTolerance = %+.2f
  Inverted = false
  LockPosition = false
  MeasureType = 1
  OverTolerance = 0
  References2D = -> [View003]
  Rotation = 0
  ScaleType = 0
  TheoreticalExact = false
  Type = 5
  UnderTolerance = 0
  X = -17.0901
  Y = -3.84275
FEATURE [TechDraw::DrawViewDimension] Dimension071
  Arbitrary = false
  ArbitraryTolerances = false
  EqualTolerance = true
  FormatSpec = 9x ⌀%.2f ↓8.0
  FormatSpecOverTolerance = %+.2f
  FormatSpecUnderTolerance = %+.2f
  Inverted = false
  LockPosition = false
  MeasureType = 1
  OverTolerance = 0
  References2D = -> [View003]
  Rotation = 0
  ScaleType = 0
  TheoreticalExact = false
  Type = 5
  UnderTolerance = 0
  X = 19.4493
  Y = -23.8511
FEATURE [TechDraw::DrawViewDimension] Dimension072
  Arbitrary = false
  ArbitraryTolerances = false
  EqualTolerance = true
  FormatSpec = 9x ⌀%.2f
  FormatSpecOverTolerance = %+.2f
  FormatSpecUnderTolerance = %+.2f
  Inverted = false
  LockPosition = false
  MeasureType = 1
  OverTolerance = 0
  References2D = -> [View003]
  Rotation = 0
  ScaleType = 0
  TheoreticalExact = false
  Type = 5
  UnderTolerance = 0
  X = 16.7495
  Y = -17.2812
FEATURE [TechDraw::DrawViewDimension] Dimension073
  Arbitrary = false
  ArbitraryTolerances = false
  EqualTolerance = true
  FormatSpec = 8x ⌀%.2f
  FormatSpecOverTolerance = %+.2f
  FormatSpecUnderTolerance = %+.2f
  Inverted = false
  LockPosition = false
  MeasureType = 1
  OverTolerance = 0
  References2D = -> [View002]
  Rotation = 0
  ScaleType = 0
  TheoreticalExact = false
  Type = 5
  UnderTolerance = 0
  X = 23.4449
  Y = 18.6394
FEATURE [TechDraw::DrawViewDimension] Dimension074
  Arbitrary = false
  ArbitraryTolerances = false
  EqualTolerance = true
  FormatSpec = 8x ⌀%.2f ↓6.0
  FormatSpecOverTolerance = %+.2f
  FormatSpecUnderTolerance = %+.2f
  Inverted = false
  LockPosition = false
  MeasureType = 1
  OverTolerance = 0
  References2D = -> [View002]
  Rotation = 0
  ScaleType = 0
  TheoreticalExact = false
  Type = 5
  UnderTolerance = 0
  X = 19.2219
  Y = 26.6485
FEATURE [TechDraw::DrawViewPart] View005  label="Left plate back"
  CoarseView = false
  Direction = (-1,0,0)
  Focus = 100
  HardHidden = false
  IsoCount = 0
  IsoHidden = false
  IsoVisible = false
  LockPosition = false
  Perspective = false
  Rotation = 0
  Scale = 0.33
  ScaleType = 0
  SeamHidden = false
  SeamVisible = true
  SmoothHidden = false
  SmoothVisible = true
  Source = -> [Body]
  X = 226.875
  XDirection = (0,-1,0)
  Y = 131.744
FEATURE [TechDraw::DrawViewDimension] Dimension075
  Arbitrary = false
  ArbitraryTolerances = false
  EqualTolerance = true
  FormatSpec = %.2f
  FormatSpecOverTolerance = %+.2f
  FormatSpecUnderTolerance = %+.2f
  Inverted = false
  LockPosition = false
  MeasureType = 1
  OverTolerance = 0
  References2D = -> [View005]
  Rotation = 0
  ScaleType = 0
  TheoreticalExact = false
  Type = 1
  UnderTolerance = 0
  X = 13.7824
  Y = 56.751
FEATURE [TechDraw::DrawViewDimension] Dimension076
  Arbitrary = false
  ArbitraryTolerances = false
  EqualTolerance = true
  FormatSpec = %.2f
  FormatSpecOverTolerance = %+.2f
  FormatSpecUnderTolerance = %+.2f
  Inverted = false
  LockPosition = false
  MeasureType = 1
  OverTolerance = 0
  References2D = -> [View005]
  Rotation = 0
  ScaleType = 0
  TheoreticalExact = false
  Type = 2
  UnderTolerance = 0
  X = -16.3833
  Y = 1.91423
FEATURE [TechDraw::DrawViewDimension] Dimension077
  Arbitrary = false
  ArbitraryTolerances = false
  EqualTolerance = true
  FormatSpec = %.2f
  FormatSpecOverTolerance = %+.2f
  FormatSpecUnderTolerance = %+.2f
  Inverted = false
  LockPosition = false
  MeasureType = 1
  OverTolerance = 0
  References2D = -> [View005]
  Rotation = 0
  ScaleType = 0
  TheoreticalExact = false
  Type = 2
  UnderTolerance = 0
  X = -9.70709
  Y = -29.3846
FEATURE [TechDraw::DrawViewDimension] Dimension078
  Arbitrary = true
  ArbitraryTolerances = false
  EqualTolerance = true
  FormatSpec = 1/4-20 ↓25.0
  FormatSpecOverTolerance = %+.2f
  FormatSpecUnderTolerance = %+.2f
  Inverted = false
  LockPosition = false
  MeasureType = 1
  OverTolerance = 0
  References2D = -> [View005]
  Rotation = 0
  ScaleType = 0
  TheoreticalExact = false
  Type = 4
  UnderTolerance = 0
  X = 13.5913
  Y = -27.9105
FEATURE [TechDraw::DrawViewDimension] Dimension079
  Arbitrary = false
  ArbitraryTolerances = false
  EqualTolerance = true
  FormatSpec = %.2f
  FormatSpecOverTolerance = %+.2f
  FormatSpecUnderTolerance = %+.2f
  Inverted = false
  LockPosition = false
  MeasureType = 1
  OverTolerance = 0
  References2D = -> [View004]
  Rotation = 0
  ScaleType = 0
  TheoreticalExact = false
  Type = 2
  UnderTolerance = 0
  X = -18.5678
  Y = 1.35148
FEATURE [TechDraw::DrawViewDimension] Dimension080
  Arbitrary = false
  ArbitraryTolerances = false
  EqualTolerance = true
  FormatSpec = %.2f
  FormatSpecOverTolerance = %+.2f
  FormatSpecUnderTolerance = %+.2f
  Inverted = false
  LockPosition = false
  MeasureType = 1
  OverTolerance = 0
  References2D = -> [View004]
  Rotation = 0
  ScaleType = 0
  TheoreticalExact = false
  Type = 2
  UnderTolerance = 0
  X = -9.65835
  Y = -30.0359
FEATURE [TechDraw::DrawPage] Page002  label="Right gantry plate"
  KeepUpdated = true
  NextBalloonIndex = 1
  ProjectionType = 0
  Template = -> Template002
  Views = -> [View003,View004,Dimension045,Dimension046,Dimension047,Dimension048,Dimension049,Dimension050,Dimension051,Dimension052,Dimension053,Dimension054,Dimension055,Dimension056,Dimension057,Dimension058,Dimension059,Dimension060,Dimension061,Dimension062,Dimension063,Dimension064,Dimension065,Dimension066,Dimension067,Dimension068,Dimension069,Dimension070,Dimension071,Dimension072,Dimension079,+1 more]
FEATURE [TechDraw::DrawSVGTemplate] Template003
  EditableTexts = DrawingTitle1=Rear gantry plate; DrawingTitle2=Count: 1; DrawingTitle3=Material: 1/2" Aluminum; DrawnBy=Andrew <owner>; Revision=V.1.0; Scale=Scale 3:1; Sheet=Sheet 1 of 1
  Height = 215.9
  Orientation = 1
  Width = 279.4
FEATURE [TechDraw::DrawProjGroupItem] ProjItem  label="Front"
  CoarseView = false
  Direction = (1,0,0)
  Focus = 100
  HardHidden = false
  IsoCount = 0
  IsoHidden = false
  IsoVisible = false
  LockPosition = true
  Perspective = false
  Rotation = 0
  RotationVector = (0,1,0)
  Scale = 0.33
  ScaleType = 2
  SeamHidden = false
  SeamVisible = true
  SmoothHidden = false
  SmoothVisible = true
  Source = -> [Body002]
  Type = 0
  X = 0
  XDirection = (0,1,0)
  Y = 0
FEATURE [TechDraw::DrawProjGroupItem] ProjItem001  label="Left"
  CoarseView = false
  Direction = (1e-16,-1,0)
  Focus = 100
  HardHidden = false
  IsoCount = 0
  IsoHidden = false
  IsoVisible = false
  LockPosition = false
  Perspective = false
  Rotation = 0
  RotationVector = (1,0,0)
  Scale = 0.33
  ScaleType = 2
  SeamHidden = false
  SeamVisible = true
  SmoothHidden = false
  SmoothVisible = true
  Source = -> [Body002]
  Type = 1
  X = 112.68
  XDirection = (1,1e-16,0)
  Y = 0
FEATURE [TechDraw::DrawProjGroupItem] ProjItem002  label="Top"
  CoarseView = false
  Direction = (0,0,1)
  Focus = 100
  HardHidden = false
  IsoCount = 0
  IsoHidden = false
  IsoVisible = false
  LockPosition = false
  Perspective = false
  Rotation = 0
  RotationVector = (1,0,0)
  Scale = 0.33
  ScaleType = 2
  SeamHidden = false
  SeamVisible = true
  SmoothHidden = false
  SmoothVisible = true
  Source = -> [Body002]
  Type = 4
  X = 0
  XDirection = (0,1,0)
  Y = -29.337
FEATURE [TechDraw::DrawProjGroup] ProjGroup
  Anchor = -> ProjItem
  AutoDistribute = true
  LockPosition = false
  ProjectionType = 0
  Rotation = 0
  Scale = 0.33
  ScaleType = 0
  Source = -> [Body002]
  Views = -> [ProjItem,ProjItem001,ProjItem002]
  X = 132.555
  Y = 153.2
  spacingX = 10
  spacingY = 0
FEATURE [TechDraw::DrawViewDimension] Dimension081
  Arbitrary = false
  ArbitraryTolerances = false
  EqualTolerance = true
  FormatSpec = %.2f
  FormatSpecOverTolerance = %+.2f
  FormatSpecUnderTolerance = %+.2f
  Inverted = false
  LockPosition = false
  MeasureType = 1
  OverTolerance = 0
  References2D = -> [ProjItem]
  Rotation = 0
  ScaleType = 0
  TheoreticalExact = false
  Type = 1
  UnderTolerance = 0
  X = -2.87134
  Y = 40.3394
FEATURE [TechDraw::DrawViewDimension] Dimension082
  Arbitrary = false
  ArbitraryTolerances = false
  EqualTolerance = true
  FormatSpec = %.2f
  FormatSpecOverTolerance = %+.2f
  FormatSpecUnderTolerance = %+.2f
  Inverted = false
  LockPosition = false
  MeasureType = 1
  OverTolerance = 0
  References2D = -> [ProjItem]
  Rotation = 0
  ScaleType = 0
  TheoreticalExact = false
  Type = 1
  UnderTolerance = 0
  X = -93.8626
  Y = 27.5378
FEATURE [TechDraw::DrawViewDimension] Dimension083
  Arbitrary = false
  ArbitraryTolerances = false
  EqualTolerance = true
  FormatSpec = %.2f
  FormatSpecOverTolerance = %+.2f
  FormatSpecUnderTolerance = %+.2f
  Inverted = false
  LockPosition = false
  MeasureType = 1
  OverTolerance = 0
  References2D = -> [ProjItem]
  Rotation = 0
  ScaleType = 0
  TheoreticalExact = false
  Type = 1
  UnderTolerance = 0
  X = -72.3015
  Y = 21.8318
FEATURE [TechDraw::DrawViewDimension] Dimension084
  Arbitrary = false
  ArbitraryTolerances = false
  EqualTolerance = true
  FormatSpec = %.2f
  FormatSpecOverTolerance = %+.2f
  FormatSpecUnderTolerance = %+.2f
  Inverted = false
  LockPosition = false
  MeasureType = 1
  OverTolerance = 0
  References2D = -> [ProjItem]
  Rotation = 0
  ScaleType = 0
  TheoreticalExact = false
  Type = 1
  UnderTolerance = 0
  X = 91.5365
  Y = 20.8382
FEATURE [TechDraw::DrawViewDimension] Dimension085
  Arbitrary = false
  ArbitraryTolerances = false
  EqualTolerance = true
  FormatSpec = %.2f
  FormatSpecOverTolerance = %+.2f
  FormatSpecUnderTolerance = %+.2f
  Inverted = false
  LockPosition = false
  MeasureType = 1
  OverTolerance = 0
  References2D = -> [ProjItem001]
  Rotation = 0
  ScaleType = 0
  TheoreticalExact = false
  Type = 1
  UnderTolerance = 0
  X = 8.01435
  Y = 20.5294
FEATURE [TechDraw::DrawViewDimension] Dimension086
  Arbitrary = true
  ArbitraryTolerances = false
  EqualTolerance = true
  FormatSpec = 2x 1/4-20 ↓25.0
  FormatSpecOverTolerance = %+.2f
  FormatSpecUnderTolerance = %+.2f
  Inverted = false
  LockPosition = false
  MeasureType = 1
  OverTolerance = 0
  References2D = -> [ProjItem001]
  Rotation = 0
  ScaleType = 0
  TheoreticalExact = false
  Type = 4
  UnderTolerance = 0
  X = -9.94401
  Y = -14.1575
FEATURE [TechDraw::DrawViewDimension] Dimension087
  Arbitrary = true
  ArbitraryTolerances = false
  EqualTolerance = true
  FormatSpec = 6x 1/4-20
  FormatSpecOverTolerance = %+.2f
  FormatSpecUnderTolerance = %+.2f
  Inverted = false
  LockPosition = false
  MeasureType = 1
  OverTolerance = 0
  References2D = -> [ProjItem]
  Rotation = 0
  ScaleType = 0
  TheoreticalExact = false
  Type = 4
  UnderTolerance = 0
  X = -59.5878
  Y = 0.524233
FEATURE [TechDraw::DrawViewDimension] Dimension088
  Arbitrary = false
  ArbitraryTolerances = false
  EqualTolerance = true
  FormatSpec = %.2f
  FormatSpecOverTolerance = %+.2f
  FormatSpecUnderTolerance = %+.2f
  Inverted = false
  LockPosition = false
  MeasureType = 1
  OverTolerance = 0
  References2D = -> [ProjItem]
  Rotation = 0
  ScaleType = 0
  TheoreticalExact = false
  Type = 2
  UnderTolerance = 0
  X = -92.4819
  Y = 1.99399
FEATURE [TechDraw::DrawViewDimension] Dimension089
  Arbitrary = false
  ArbitraryTolerances = false
  EqualTolerance = true
  FormatSpec = %.2f
  FormatSpecOverTolerance = %+.2f
  FormatSpecUnderTolerance = %+.2f
  Inverted = false
  LockPosition = false
  MeasureType = 1
  OverTolerance = 0
  References2D = -> [ProjItem]
  Rotation = 0
  ScaleType = 0
  TheoreticalExact = false
  Type = 2
  UnderTolerance = 0
  X = -106.875
  Y = 2.09693
FEATURE [TechDraw::DrawViewDimension] Dimension090
  Arbitrary = false
  ArbitraryTolerances = false
  EqualTolerance = true
  FormatSpec = %.2f
  FormatSpecOverTolerance = %+.2f
  FormatSpecUnderTolerance = %+.2f
  Inverted = false
  LockPosition = false
  MeasureType = 1
  OverTolerance = 0
  References2D = -> [ProjItem002]
  Rotation = 0
  ScaleType = 0
  TheoreticalExact = false
  Type = 1
  UnderTolerance = 0
  X = -51.4813
  Y = -8.45763
FEATURE [TechDraw::DrawViewDimension] Dimension091
  Arbitrary = false
  ArbitraryTolerances = false
  EqualTolerance = true
  FormatSpec = %.2f
  FormatSpecOverTolerance = %+.2f
  FormatSpecUnderTolerance = %+.2f
  Inverted = false
  LockPosition = false
  MeasureType = 1
  OverTolerance = 0
  References2D = -> [ProjItem002]
  Rotation = 0
  ScaleType = 0
  TheoreticalExact = false
  Type = 1
  UnderTolerance = 0
  X = -89.2318
  Y = -8.22664
FEATURE [TechDraw::DrawViewDimension] Dimension092
  Arbitrary = true
  ArbitraryTolerances = false
  EqualTolerance = true
  FormatSpec = 4x 1/4-20 ↓25.0
  FormatSpecOverTolerance = %+.2f
  FormatSpecUnderTolerance = %+.2f
  Inverted = false
  LockPosition = false
  MeasureType = 1
  OverTolerance = 0
  References2D = -> [ProjItem002]
  Rotation = 0
  ScaleType = 0
  TheoreticalExact = false
  Type = 4
  UnderTolerance = 0
  X = -62.2124
  Y = 12.6286
FEATURE [TechDraw::DrawPage] Page003  label="Rear gantry plate"
  KeepUpdated = true
  NextBalloonIndex = 1
  ProjectionType = 0
  Template = -> Template003
  Views = -> [ProjGroup,Dimension081,Dimension082,Dimension083,Dimension084,Dimension085,Dimension086,Dimension087,Dimension088,Dimension089,Dimension090,Dimension091,Dimension092]
FEATURE [TechDraw::DrawViewDimension] Dimension093
  Arbitrary = false
  ArbitraryTolerances = false
  EqualTolerance = true
  FormatSpec = %.2f
  FormatSpecOverTolerance = %+.2f
  FormatSpecUnderTolerance = %+.2f
  Inverted = false
  LockPosition = false
  MeasureType = 1
  OverTolerance = 0
  References2D = -> [View002]
  Rotation = 0
  ScaleType = 0
  TheoreticalExact = false
  Type = 1
  UnderTolerance = 0
  X = -41.1809
  Y = -30.6587
FEATURE [TechDraw::DrawPage] Page001  label="Left gantry plate"
  KeepUpdated = true
  NextBalloonIndex = 1
  ProjectionType = 0
  Template = -> Template001
  Views = -> [View002,Dimension011,Dimension012,Dimension013,Dimension014,Dimension015,Dimension016,Dimension017,Dimension018,Dimension019,Dimension020,Dimension021,Dimension022,Dimension023,Dimension024,Dimension025,Dimension026,Dimension027,Dimension028,Dimension029,Dimension030,Dimension031,Dimension032,Dimension033,Dimension034,Dimension035,Dimension036,Dimension037,Dimension038,Dimension039,Dimension040,+12 more]
FEATURE [App::DocumentObjectGroup] Group002  label="Darwings"
  ExportMode = 1
  Group = -> [Page,Page001,Page002,Page003]
  _GroupVersion = 1
FEATURE [Part::FeaturePython] Assembly  label="Right plate Assembly"  # WARN: FeaturePython — macro-defined, semantics opaque (R4)
  AutoRelax = true
  BuildShape = 0
  Freeze = false
  Group = -> [Constraints,Elements,Parts]
  Placement = pos=(0,155,0) rot=(0,0,1;0rad)
  Verbose = false
  _LinkVersion = 1
  _SolverType = 1
  _Version = 1
FEATURE [App::FeaturePython] Constraints  # WARN: FeaturePython — macro-defined, semantics opaque (R4)
  Group = -> [Constraint,Constraint024,Constraint025,Constraint026,Constraint027,Constraint028,Constraint029,Constraint030,Constraint031,Constraint032,Constraint033,Constraint034,Constraint035,Constraint036,Constraint037,Constraint038,Constraint039,Constraint040,Constraint049,Constraint050,Constraint051]
  _LinkVersion = 1
  _Version = 1
FEATURE [App::FeaturePython] Elements  # WARN: FeaturePython — macro-defined, semantics opaque (R4)
  Group = -> [Element,Element001,Element007,Element013,Element014,Element022,Element023,Element024,Element025,Element026,Element027,Element028,Element029,Element030,Element031,_Element025,_Element026,_Element027,_Element028,_Element029,_Element030,_Element031,_Element032,_Element033,_Element034,_Element035,_Element036,_Element037,_Element038,_Element039,_Element040,_Element041,_Element042,_Element043,+12 more]
  _LinkVersion = 1
FEATURE [Part::FeaturePython] Assembly001  label="Left plate Assembly"  # WARN: FeaturePython — macro-defined, semantics opaque (R4)
  AutoRelax = true
  BuildShape = 0
  Freeze = false
  Group = -> [Constraints001,Elements001,Parts001]
  Placement = pos=(0,-297,0) rot=(0,0,1;0rad)
  Verbose = false
  _LinkVersion = 1
  _SolverType = 1
  _Version = 1
FEATURE [App::FeaturePython] Constraints001  # WARN: FeaturePython — macro-defined, semantics opaque (R4)
  Group = -> [Constraint001,Constraint007,Constraint008,Constraint009,Constraint010,Constraint011,Constraint012,Constraint013,Constraint014,Constraint015,Constraint016,Constraint017,Constraint018,Constraint019,Constraint020,Constraint021,Constraint022,Constraint023,Constraint052,Constraint053,Constraint054]
  _LinkVersion = 1
  _Version = 1
FEATURE [App::FeaturePython] Elements001  # WARN: FeaturePython — macro-defined, semantics opaque (R4)
  Group = -> [Element002,Element003,Element004,Element008,Element015,Element016,Element021,Element032,Element033,Element034,Element035,Element036,Element037,Element038,Element039,Element040,_Element,_Element001,_Element002,_Element003,_Element004,_Element005,_Element006,_Element007,_Element008,_Element009,_Element010,_Element011,_Element012,_Element013,_Element014,_Element015,_Element016,_Element017,+13 more]
  _LinkVersion = 1
FEATURE [Part::FeaturePython] Element  label="top-beam-mate"  # link proxy (typed FeaturePython)
  Detach = false
  LinkTransform = true
  LinkedObject = -> Link001 [Hole003.Edge36]
  _LinkVersion = 1
  _Parent = -> Elements
FEATURE [Part::FeaturePython] Element001  label="bottom-beam-mate"  # link proxy (typed FeaturePython)
  Detach = false
  LinkTransform = true
  LinkedObject = -> Link001 [Hole003.Edge42]
  _LinkVersion = 1
  _Parent = -> Elements
FEATURE [App::FeaturePython] Constraint  label="Locked"  # WARN: FeaturePython — macro-defined, semantics opaque (R4)
  Disabled = false
  Group = -> [ElementLink]
  _ConstraintType = 0
  _LinkVersion = 1
  _Parent = -> Constraints
FEATURE [App::FeaturePython] ElementLink  label="top-beam-mate"  # link proxy (typed FeaturePython)
  LinkTransform = true
  LinkedObject = -> Element
  _LinkVersion = 1
  _Parent = -> Constraint
FEATURE [Part::FeaturePython] Element002  label="top-beam-mate"  # link proxy (typed FeaturePython)
  Detach = false
  LinkTransform = true
  LinkedObject = -> Link [Hole001.Edge42]
  _LinkVersion = 1
  _Parent = -> Elements001
FEATURE [Part::FeaturePython] Element003  label="bottom-beam-mate"  # link proxy (typed FeaturePython)
  Detach = false
  LinkTransform = true
  LinkedObject = -> Link [Hole001.Edge40]
  _LinkVersion = 1
  _Parent = -> Elements001
FEATURE [App::FeaturePython] Constraint001  label="Locked001"  # WARN: FeaturePython — macro-defined, semantics opaque (R4)
  Disabled = false
  Group = -> [ElementLink001]
  _ConstraintType = 0
  _LinkVersion = 1
  _Parent = -> Constraints001
FEATURE [App::FeaturePython] ElementLink001  label="top-beam-mate"  # link proxy (typed FeaturePython)
  LinkTransform = true
  LinkedObject = -> Element002
  _LinkVersion = 1
  _Parent = -> Constraint001
FEATURE [Part::FeaturePython] Element004  label="motor-mate"  # link proxy (typed FeaturePython)
  Detach = false
  LinkTransform = true
  LinkedObject = -> Link [Pocket.Edge24]
  _LinkVersion = 1
  _Parent = -> Elements001
FEATURE [Part::FeaturePython] Assembly003  label="Rear plate Assembly"  # WARN: FeaturePython — macro-defined, semantics opaque (R4)
  AutoRelax = true
  BuildShape = 0
  Freeze = false
  Group = -> [Constraints003,Elements003,Parts003]
  Placement = pos=(-132,7.62939e-06,12) rot=(0,0,1;0rad)
  Verbose = false
  _LinkVersion = 1
  _SolverType = 1
  _Version = 1
FEATURE [App::FeaturePython] Constraints003  # WARN: FeaturePython — macro-defined, semantics opaque (R4)
  Group = -> [Constraint003]
  _LinkVersion = 1
  _Version = 1
FEATURE [App::FeaturePython] Elements003  # WARN: FeaturePython — macro-defined, semantics opaque (R4)
  Group = -> [Element006]
  _LinkVersion = 1
FEATURE [Part::FeaturePython] Element006  label="side-mate-L"  # link proxy (typed FeaturePython)
  Detach = false
  LinkTransform = true
  LinkedObject = -> Link003 [Pocket007.Edge12]
  _LinkVersion = 1
  _Parent = -> Elements003
FEATURE [App::FeaturePython] Constraint003  label="Locked003"  # WARN: FeaturePython — macro-defined, semantics opaque (R4)
  Disabled = false
  Group = -> [ElementLink003]
  _ConstraintType = 0
  _LinkVersion = 1
  _Parent = -> Constraints003
FEATURE [App::FeaturePython] ElementLink003  label="side-mate-L"  # link proxy (typed FeaturePython)
  LinkTransform = true
  LinkedObject = -> Element006
  _LinkVersion = 1
  _Parent = -> Constraint003
FEATURE [Part::FeaturePython] Element007  label="rear-mate"  # link proxy (typed FeaturePython)
  Detach = false
  LinkTransform = true
  LinkedObject = -> Link001 [Hole004.?Edge44]
  _LinkVersion = 1
  _Parent = -> Elements
FEATURE [Part::FeaturePython] Element008  label="rear-mate"  # link proxy (typed FeaturePython)
  Detach = false
  LinkTransform = true
  LinkedObject = -> Link [Hole005.Edge50]
  _LinkVersion = 1
  _Parent = -> Elements001
FEATURE [App::DocumentObjectGroup] Group001  label="Assemblies"
  ExportMode = 1
  Group = -> [Assembly,Assembly001,Assembly003,Assembly005]
  _GroupVersion = 1
FEATURE [Part::FeaturePython] Element013  label="cart-L"  # link proxy (typed FeaturePython)
  Detach = false
  LinkTransform = true
  LinkedObject = -> Link001 [Pocket011.Edge40]
  _LinkVersion = 1
  _Parent = -> Elements
FEATURE [Part::FeaturePython] Element014  label="cart-R"  # link proxy (typed FeaturePython)
  Detach = false
  LinkTransform = true
  LinkedObject = -> Link001 [Pocket011.Edge59]
  _LinkVersion = 1
  _Parent = -> Elements
FEATURE [Part::FeaturePython] Element015  label="cart-L"  # link proxy (typed FeaturePython)
  Detach = false
  LinkTransform = true
  LinkedObject = -> Link [Hole005.Edge61]
  _LinkVersion = 1
  _Parent = -> Elements001
FEATURE [Part::FeaturePython] Element016  label="cart-R"  # link proxy (typed FeaturePython)
  Detach = false
  LinkTransform = true
  LinkedObject = -> Link [Hole005.Edge41]
  _LinkVersion = 1
  _Parent = -> Elements001
FEATURE [Part::FeaturePython] Assembly005  label="Gouverner Assembly"  # WARN: FeaturePython — macro-defined, semantics opaque (R4)
  AutoRelax = true
  BuildShape = 0
  Freeze = false
  Group = -> [Constraints005,Elements005,Parts005]
  Verbose = false
  _LinkVersion = 1
  _SolverType = 1
  _Version = 1
FEATURE [App::FeaturePython] Constraints005  # WARN: FeaturePython — macro-defined, semantics opaque (R4)
  Group = -> [Constraint005,Constraint006,Constraint041,Constraint042,Constraint043,Constraint044,Constraint045,Constraint046,Constraint047,Constraint048]
  _LinkVersion = 1
  _Version = 1
FEATURE [App::FeaturePython] Elements005  # WARN: FeaturePython — macro-defined, semantics opaque (R4)
  Group = -> [Element017,Element018,Element019,Element020,_Element050,_Element051,_Element052,_Element053,_Element054,_Element055,_Element056,_Element057,_Element058,_Element059,_Element060,_Element061,_Element062,_Element063,_Element064,_Element065]
  _LinkVersion = 1
FEATURE [Part::FeaturePython] Element017  label="plate-mate"  # link proxy (typed FeaturePython)
  Detach = false
  LinkTransform = true
  LinkedObject = -> Link005 [Chamfer.Edge14]
  _LinkVersion = 1
  _Parent = -> Elements005
FEATURE [Part::FeaturePython] Element018  label="gov-mate"  # link proxy (typed FeaturePython)
  Detach = false
  LinkTransform = true
  LinkedObject = -> Link005 [Chamfer.Edge27]
  _LinkVersion = 1
  _Parent = -> Elements005
FEATURE [Part::FeaturePython] Element019  label="shim-mate"  # link proxy (typed FeaturePython)
  Detach = false
  LinkTransform = true
  LinkedObject = -> Link006 [Chamfer001.Edge18]
  _LinkVersion = 1
  _Parent = -> Elements005
FEATURE [App::FeaturePython] Constraint005  label="Locked005"  # WARN: FeaturePython — macro-defined, semantics opaque (R4)
  Disabled = false
  Group = -> [ElementLink005]
  _ConstraintType = 0
  _LinkVersion = 1
  _Parent = -> Constraints005
FEATURE [App::FeaturePython] ElementLink005  label="plate-mate"  # link proxy (typed FeaturePython)
  LinkTransform = true
  LinkedObject = -> Element017
  _LinkVersion = 1
  _Parent = -> Constraint005
FEATURE [App::FeaturePython] Constraint006  label="Attachment"  # WARN: FeaturePython — macro-defined, semantics opaque (R4)
  Cascade = false
  Disabled = false
  Group = -> [ElementLink006,ElementLink007]
  Multiply = false
  _ConstraintType = 45
  _LinkVersion = 1
  _Parent = -> Constraints005
FEATURE [App::FeaturePython] ElementLink006  label="shim-mate"  # link proxy (typed FeaturePython)
  LinkTransform = true
  LinkedObject = -> Element019
  _LinkVersion = 1
  _Parent = -> Constraint006
FEATURE [App::FeaturePython] ElementLink007  label="gov-mate"  # link proxy (typed FeaturePython)
  LinkTransform = true
  LinkedObject = -> Element018
  _LinkVersion = 1
  _Parent = -> Constraint006
FEATURE [Part::FeaturePython] Element020  label="nut-mate"  # link proxy (typed FeaturePython)
  Detach = false
  LinkTransform = true
  LinkedObject = -> Link006 [Chamfer001.Edge14]
  _LinkVersion = 1
  _Parent = -> Elements005
FEATURE [Part::FeaturePython] Element021  label="gov-mate"  # link proxy (typed FeaturePython)
  Detach = false
  LinkTransform = true
  LinkedObject = -> Link [Pocket010.Edge36]
  _LinkVersion = 1
  _Parent = -> Elements001
FEATURE [Part::FeaturePython] Element022  label="gov-mate"  # link proxy (typed FeaturePython)
  Detach = false
  LinkTransform = true
  LinkedObject = -> Link001 [Pocket011.Edge29]
  _LinkVersion = 1
  _Parent = -> Elements
FEATURE [Part::FeaturePython] Element023  # link proxy (typed FeaturePython)
  Detach = false
  LinkTransform = true
  LinkedObject = -> Link001 [Pocket011.Edge86]
  _LinkVersion = 1
  _Parent = -> Elements
FEATURE [Part::FeaturePython] Element024  # link proxy (typed FeaturePython)
  Detach = false
  LinkTransform = true
  LinkedObject = -> Link001 [Pocket011.Edge82]
  _LinkVersion = 1
  _Parent = -> Elements
FEATURE [Part::FeaturePython] Element025  # link proxy (typed FeaturePython)
  Detach = false
  LinkTransform = true
  LinkedObject = -> Link001 [Pocket011.Edge116]
  _LinkVersion = 1
  _Parent = -> Elements
FEATURE [Part::FeaturePython] Element026  # link proxy (typed FeaturePython)
  Detach = false
  LinkTransform = true
  LinkedObject = -> Link001 [Pocket011.Edge112]
  _LinkVersion = 1
  _Parent = -> Elements
FEATURE [Part::FeaturePython] Element027  # link proxy (typed FeaturePython)
  Detach = false
  LinkTransform = true
  LinkedObject = -> Link001 [Pocket011.Edge114]
  _LinkVersion = 1
  _Parent = -> Elements
FEATURE [Part::FeaturePython] Element028  # link proxy (typed FeaturePython)
  Detach = false
  LinkTransform = true
  LinkedObject = -> Link001 [Pocket011.Edge126]
  _LinkVersion = 1
  _Parent = -> Elements
FEATURE [Part::FeaturePython] Element029  # link proxy (typed FeaturePython)
  Detach = false
  LinkTransform = true
  LinkedObject = -> Link001 [Pocket011.Edge122]
  _LinkVersion = 1
  _Parent = -> Elements
FEATURE [Part::FeaturePython] Element030  # link proxy (typed FeaturePython)
  Detach = false
  LinkTransform = true
  LinkedObject = -> Link001 [Pocket011.Edge110]
  _LinkVersion = 1
  _Parent = -> Elements
FEATURE [Part::FeaturePython] Element031  # link proxy (typed FeaturePython)
  Detach = false
  LinkTransform = true
  LinkedObject = -> Link001 [Pocket011.Edge119]
  _LinkVersion = 1
  _Parent = -> Elements
FEATURE [Part::FeaturePython] Element032  # link proxy (typed FeaturePython)
  Detach = false
  LinkTransform = true
  LinkedObject = -> Link [Pocket010.Edge141]
  _LinkVersion = 1
  _Parent = -> Elements001
FEATURE [Part::FeaturePython] Element033  # link proxy (typed FeaturePython)
  Detach = false
  LinkTransform = true
  LinkedObject = -> Link [Pocket010.Edge139]
  _LinkVersion = 1
  _Parent = -> Elements001
FEATURE [Part::FeaturePython] Element034  # link proxy (typed FeaturePython)
  Detach = false
  LinkTransform = true
  LinkedObject = -> Link [Pocket010.Edge137]
  _LinkVersion = 1
  _Parent = -> Elements001
FEATURE [Part::FeaturePython] Element035  # link proxy (typed FeaturePython)
  Detach = false
  LinkTransform = true
  LinkedObject = -> Link [Pocket010.Edge135]
  _LinkVersion = 1
  _Parent = -> Elements001
FEATURE [Part::FeaturePython] Element036  # link proxy (typed FeaturePython)
  Detach = false
  LinkTransform = true
  LinkedObject = -> Link [Pocket010.Edge134]
  _LinkVersion = 1
  _Parent = -> Elements001
FEATURE [Part::FeaturePython] Element037  # link proxy (typed FeaturePython)
  Detach = false
  LinkTransform = true
  LinkedObject = -> Link [Pocket010.Edge129]
  _LinkVersion = 1
  _Parent = -> Elements001
FEATURE [Part::FeaturePython] Element038  # link proxy (typed FeaturePython)
  Detach = false
  LinkTransform = true
  LinkedObject = -> Link [Pocket010.Edge125]
  _LinkVersion = 1
  _Parent = -> Elements001
FEATURE [Part::FeaturePython] Element039  # link proxy (typed FeaturePython)
  Detach = false
  LinkTransform = true
  LinkedObject = -> Link [Pocket010.Edge127]
  _LinkVersion = 1
  _Parent = -> Elements001
FEATURE [Part::FeaturePython] Element040  # link proxy (typed FeaturePython)
  Detach = false
  LinkTransform = true
  LinkedObject = -> Link [Pocket010.Edge131]
  _LinkVersion = 1
  _Parent = -> Elements001
FEATURE [App::FeaturePython] Constraint007  label="Attachment001"  # WARN: FeaturePython — macro-defined, semantics opaque (R4)
  Cascade = false
  Disabled = false
  Group = -> [ElementLink008,ElementLink009]
  Multiply = false
  _ConstraintType = 45
  _LinkVersion = 1
  _Parent = -> Constraints001
FEATURE [App::FeaturePython] ElementLink008  label="Element032"  # link proxy (typed FeaturePython)
  LinkTransform = true
  LinkedObject = -> Element032
  _LinkVersion = 1
  _Parent = -> Constraint007
FEATURE [App::FeaturePython] ElementLink009  label="_Element"  # link proxy (typed FeaturePython)
  LinkTransform = true
  LinkedObject = -> _Element
  _LinkVersion = 1
  _Parent = -> Constraint007
FEATURE [Part::FeaturePython] _Element  # link proxy (typed FeaturePython)
  Detach = false
  LinkTransform = true
  LinkedObject = -> Link007 [0.Edge9]
  _LinkVersion = 1
  _Parent = -> Elements001
FEATURE [App::FeaturePython] Constraint008  label="Attachment002"  # WARN: FeaturePython — macro-defined, semantics opaque (R4)
  Cascade = false
  Disabled = false
  Group = -> [ElementLink010,ElementLink011]
  Multiply = false
  _ConstraintType = 45
  _LinkVersion = 1
  _Parent = -> Constraints001
FEATURE [App::FeaturePython] ElementLink010  label="Element033"  # link proxy (typed FeaturePython)
  LinkTransform = true
  LinkedObject = -> Element033
  _LinkVersion = 1
  _Parent = -> Constraint008
FEATURE [App::FeaturePython] ElementLink011  label="_Element001"  # link proxy (typed FeaturePython)
  LinkTransform = true
  LinkedObject = -> _Element001
  _LinkVersion = 1
  _Parent = -> Constraint008
FEATURE [Part::FeaturePython] _Element001  # link proxy (typed FeaturePython)
  Detach = false
  LinkTransform = true
  LinkedObject = -> Link007 [1.Edge9]
  _LinkVersion = 1
  _Parent = -> Elements001
FEATURE [App::FeaturePython] Constraint009  label="Attachment003"  # WARN: FeaturePython — macro-defined, semantics opaque (R4)
  Cascade = false
  Disabled = false
  Group = -> [ElementLink012,ElementLink013]
  Multiply = false
  _ConstraintType = 45
  _LinkVersion = 1
  _Parent = -> Constraints001
FEATURE [App::FeaturePython] ElementLink012  label="Element034"  # link proxy (typed FeaturePython)
  LinkTransform = true
  LinkedObject = -> Element034
  _LinkVersion = 1
  _Parent = -> Constraint009
FEATURE [App::FeaturePython] ElementLink013  label="_Element002"  # link proxy (typed FeaturePython)
  LinkTransform = true
  LinkedObject = -> _Element002
  _LinkVersion = 1
  _Parent = -> Constraint009
FEATURE [Part::FeaturePython] _Element002  # link proxy (typed FeaturePython)
  Detach = false
  LinkTransform = true
  LinkedObject = -> Link007 [2.Edge9]
  _LinkVersion = 1
  _Parent = -> Elements001
FEATURE [App::FeaturePython] Constraint010  label="Attachment004"  # WARN: FeaturePython — macro-defined, semantics opaque (R4)
  Cascade = false
  Disabled = false
  Group = -> [ElementLink014,ElementLink015]
  Multiply = false
  _ConstraintType = 45
  _LinkVersion = 1
  _Parent = -> Constraints001
FEATURE [App::FeaturePython] ElementLink014  label="Element035"  # link proxy (typed FeaturePython)
  LinkTransform = true
  LinkedObject = -> Element035
  _LinkVersion = 1
  _Parent = -> Constraint010
FEATURE [App::FeaturePython] ElementLink015  label="_Element003"  # link proxy (typed FeaturePython)
  LinkTransform = true
  LinkedObject = -> _Element003
  _LinkVersion = 1
  _Parent = -> Constraint010
FEATURE [Part::FeaturePython] _Element003  # link proxy (typed FeaturePython)
  Detach = false
  LinkTransform = true
  LinkedObject = -> Link007 [3.Edge9]
  _LinkVersion = 1
  _Parent = -> Elements001
FEATURE [App::FeaturePython] Constraint011  label="Attachment005"  # WARN: FeaturePython — macro-defined, semantics opaque (R4)
  Cascade = false
  Disabled = false
  Group = -> [ElementLink016,ElementLink017]
  Multiply = false
  _ConstraintType = 45
  _LinkVersion = 1
  _Parent = -> Constraints001
FEATURE [App::FeaturePython] ElementLink016  label="Element036"  # link proxy (typed FeaturePython)
  LinkTransform = true
  LinkedObject = -> Element036
  _LinkVersion = 1
  _Parent = -> Constraint011
FEATURE [App::FeaturePython] ElementLink017  label="_Element004"  # link proxy (typed FeaturePython)
  LinkTransform = true
  LinkedObject = -> _Element004
  _LinkVersion = 1
  _Parent = -> Constraint011
FEATURE [Part::FeaturePython] _Element004  # link proxy (typed FeaturePython)
  Detach = false
  LinkTransform = true
  LinkedObject = -> Link007 [4.Edge9]
  _LinkVersion = 1
  _Parent = -> Elements001
FEATURE [App::FeaturePython] Constraint012  label="Attachment006"  # WARN: FeaturePython — macro-defined, semantics opaque (R4)
  Cascade = false
  Disabled = false
  Group = -> [ElementLink018,ElementLink019]
  Multiply = false
  _ConstraintType = 45
  _LinkVersion = 1
  _Parent = -> Constraints001
FEATURE [App::FeaturePython] ElementLink018  label="Element037"  # link proxy (typed FeaturePython)
  LinkTransform = true
  LinkedObject = -> Element037
  _LinkVersion = 1
  _Parent = -> Constraint012
FEATURE [App::FeaturePython] ElementLink019  label="_Element005"  # link proxy (typed FeaturePython)
  LinkTransform = true
  LinkedObject = -> _Element005
  _LinkVersion = 1
  _Parent = -> Constraint012
FEATURE [Part::FeaturePython] _Element005  # link proxy (typed FeaturePython)
  Detach = false
  LinkTransform = true
  LinkedObject = -> Link007 [5.Edge9]
  _LinkVersion = 1
  _Parent = -> Elements001
FEATURE [App::FeaturePython] Constraint013  label="Attachment007"  # WARN: FeaturePython — macro-defined, semantics opaque (R4)
  Cascade = false
  Disabled = false
  Group = -> [ElementLink020,ElementLink021]
  Multiply = false
  _ConstraintType = 45
  _LinkVersion = 1
  _Parent = -> Constraints001
FEATURE [App::FeaturePython] ElementLink020  label="Element038"  # link proxy (typed FeaturePython)
  LinkTransform = true
  LinkedObject = -> Element038
  _LinkVersion = 1
  _Parent = -> Constraint013
FEATURE [App::FeaturePython] ElementLink021  label="_Element006"  # link proxy (typed FeaturePython)
  LinkTransform = true
  LinkedObject = -> _Element006
  _LinkVersion = 1
  _Parent = -> Constraint013
FEATURE [Part::FeaturePython] _Element006  # link proxy (typed FeaturePython)
  Detach = false
  LinkTransform = true
  LinkedObject = -> Link007 [6.Edge9]
  _LinkVersion = 1
  _Parent = -> Elements001
FEATURE [App::FeaturePython] Constraint014  label="Attachment008"  # WARN: FeaturePython — macro-defined, semantics opaque (R4)
  Cascade = false
  Disabled = false
  Group = -> [ElementLink022,ElementLink023]
  Multiply = false
  _ConstraintType = 45
  _LinkVersion = 1
  _Parent = -> Constraints001
FEATURE [App::FeaturePython] ElementLink022  label="Element039"  # link proxy (typed FeaturePython)
  LinkTransform = true
  LinkedObject = -> Element039
  _LinkVersion = 1
  _Parent = -> Constraint014
FEATURE [App::FeaturePython] ElementLink023  label="_Element007"  # link proxy (typed FeaturePython)
  LinkTransform = true
  LinkedObject = -> _Element007
  _LinkVersion = 1
  _Parent = -> Constraint014
FEATURE [Part::FeaturePython] _Element007  # link proxy (typed FeaturePython)
  Detach = false
  LinkTransform = true
  LinkedObject = -> Link007 [7.Edge9]
  _LinkVersion = 1
  _Parent = -> Elements001
FEATURE [App::FeaturePython] Constraint015  label="Attachment009"  # WARN: FeaturePython — macro-defined, semantics opaque (R4)
  Cascade = false
  Disabled = false
  Group = -> [ElementLink024,ElementLink025]
  Multiply = false
  _ConstraintType = 45
  _LinkVersion = 1
  _Parent = -> Constraints001
FEATURE [App::FeaturePython] ElementLink024  label="_Element008"  # link proxy (typed FeaturePython)
  LinkTransform = true
  LinkedObject = -> _Element008
  _LinkVersion = 1
  _Parent = -> Constraint015
FEATURE [Part::FeaturePython] _Element008  # link proxy (typed FeaturePython)
  Detach = false
  LinkTransform = true
  LinkedObject = -> Link007 [8.Edge9]
  _LinkVersion = 1
  _Parent = -> Elements001
FEATURE [App::FeaturePython] ElementLink025  label="Element040"  # link proxy (typed FeaturePython)
  LinkTransform = true
  LinkedObject = -> Element040
  _LinkVersion = 1
  _Parent = -> Constraint015
FEATURE [App::FeaturePython] Constraint016  label="Attachment010"  # WARN: FeaturePython — macro-defined, semantics opaque (R4)
  Cascade = false
  Disabled = false
  Group = -> [ElementLink026,ElementLink027]
  Multiply = false
  _ConstraintType = 45
  _LinkVersion = 1
  _Parent = -> Constraints001
FEATURE [App::FeaturePython] ElementLink026  label="_Element009"  # link proxy (typed FeaturePython)
  LinkTransform = true
  LinkedObject = -> _Element009
  _LinkVersion = 1
  _Parent = -> Constraint016
FEATURE [Part::FeaturePython] _Element009  # link proxy (typed FeaturePython)
  Detach = false
  LinkTransform = true
  LinkedObject = -> Link008 [0.Edge9]
  _LinkVersion = 1
  _Parent = -> Elements001
FEATURE [App::FeaturePython] ElementLink027  label="_Element010"  # link proxy (typed FeaturePython)
  LinkTransform = true
  LinkedObject = -> _Element010
  _LinkVersion = 1
  _Parent = -> Constraint016
FEATURE [Part::FeaturePython] _Element010  # link proxy (typed FeaturePython)
  Detach = false
  LinkTransform = true
  LinkedObject = -> Link [Pocket010.Edge119]
  _LinkVersion = 1
  _Parent = -> Elements001
FEATURE [App::FeaturePython] Constraint017  label="Attachment011"  # WARN: FeaturePython — macro-defined, semantics opaque (R4)
  Cascade = false
  Disabled = false
  Group = -> [ElementLink028,ElementLink029]
  Multiply = false
  _ConstraintType = 45
  _LinkVersion = 1
  _Parent = -> Constraints001
FEATURE [App::FeaturePython] ElementLink028  label="_Element011"  # link proxy (typed FeaturePython)
  LinkTransform = true
  LinkedObject = -> _Element011
  _LinkVersion = 1
  _Parent = -> Constraint017
FEATURE [Part::FeaturePython] _Element011  # link proxy (typed FeaturePython)
  Detach = false
  LinkTransform = true
  LinkedObject = -> Link008 [1.Edge9]
  _LinkVersion = 1
  _Parent = -> Elements001
FEATURE [App::FeaturePython] ElementLink029  label="_Element012"  # link proxy (typed FeaturePython)
  LinkTransform = true
  LinkedObject = -> _Element012
  _LinkVersion = 1
  _Parent = -> Constraint017
FEATURE [Part::FeaturePython] _Element012  # link proxy (typed FeaturePython)
  Detach = false
  LinkTransform = true
  LinkedObject = -> Link [Pocket010.Edge117]
  _LinkVersion = 1
  _Parent = -> Elements001
FEATURE [App::FeaturePython] Constraint018  label="Attachment012"  # WARN: FeaturePython — macro-defined, semantics opaque (R4)
  Cascade = false
  Disabled = false
  Group = -> [ElementLink030,ElementLink031]
  Multiply = false
  _ConstraintType = 45
  _LinkVersion = 1
  _Parent = -> Constraints001
FEATURE [App::FeaturePython] ElementLink030  label="_Element013"  # link proxy (typed FeaturePython)
  LinkTransform = true
  LinkedObject = -> _Element013
  _LinkVersion = 1
  _Parent = -> Constraint018
FEATURE [Part::FeaturePython] _Element013  # link proxy (typed FeaturePython)
  Detach = false
  LinkTransform = true
  LinkedObject = -> Link008 [2.Edge9]
  _LinkVersion = 1
  _Parent = -> Elements001
FEATURE [App::FeaturePython] ElementLink031  label="_Element014"  # link proxy (typed FeaturePython)
  LinkTransform = true
  LinkedObject = -> _Element014
  _LinkVersion = 1
  _Parent = -> Constraint018
FEATURE [Part::FeaturePython] _Element014  # link proxy (typed FeaturePython)
  Detach = false
  LinkTransform = true
  LinkedObject = -> Link [Pocket010.Edge123]
  _LinkVersion = 1
  _Parent = -> Elements001
FEATURE [App::FeaturePython] Constraint019  label="Attachment013"  # WARN: FeaturePython — macro-defined, semantics opaque (R4)
  Cascade = false
  Disabled = false
  Group = -> [ElementLink032,ElementLink033]
  Multiply = false
  _ConstraintType = 45
  _LinkVersion = 1
  _Parent = -> Constraints001
FEATURE [App::FeaturePython] ElementLink032  label="_Element015"  # link proxy (typed FeaturePython)
  LinkTransform = true
  LinkedObject = -> _Element015
  _LinkVersion = 1
  _Parent = -> Constraint019
FEATURE [Part::FeaturePython] _Element015  # link proxy (typed FeaturePython)
  Detach = false
  LinkTransform = true
  LinkedObject = -> Link008 [3.Edge9]
  _LinkVersion = 1
  _Parent = -> Elements001
FEATURE [App::FeaturePython] ElementLink033  label="_Element016"  # link proxy (typed FeaturePython)
  LinkTransform = true
  LinkedObject = -> _Element016
  _LinkVersion = 1
  _Parent = -> Constraint019
FEATURE [Part::FeaturePython] _Element016  # link proxy (typed FeaturePython)
  Detach = false
  LinkTransform = true
  LinkedObject = -> Link [Pocket010.Edge121]
  _LinkVersion = 1
  _Parent = -> Elements001
FEATURE [App::FeaturePython] Constraint020  label="Attachment014"  # WARN: FeaturePython — macro-defined, semantics opaque (R4)
  Cascade = false
  Disabled = false
  Group = -> [ElementLink034,ElementLink035]
  Multiply = false
  _ConstraintType = 45
  _LinkVersion = 1
  _Parent = -> Constraints001
FEATURE [App::FeaturePython] ElementLink034  label="_Element017"  # link proxy (typed FeaturePython)
  LinkTransform = true
  LinkedObject = -> _Element017
  _LinkVersion = 1
  _Parent = -> Constraint020
FEATURE [Part::FeaturePython] _Element017  # link proxy (typed FeaturePython)
  Detach = false
  LinkTransform = true
  LinkedObject = -> Link008 [7.Edge9]
  _LinkVersion = 1
  _Parent = -> Elements001
FEATURE [App::FeaturePython] ElementLink035  label="_Element018"  # link proxy (typed FeaturePython)
  LinkTransform = true
  LinkedObject = -> _Element018
  _LinkVersion = 1
  _Parent = -> Constraint020
FEATURE [Part::FeaturePython] _Element018  # link proxy (typed FeaturePython)
  Detach = false
  LinkTransform = true
  LinkedObject = -> Link [Pocket010.Edge149]
  _LinkVersion = 1
  _Parent = -> Elements001
FEATURE [App::FeaturePython] Constraint021  label="Attachment015"  # WARN: FeaturePython — macro-defined, semantics opaque (R4)
  Cascade = false
  Disabled = false
  Group = -> [ElementLink036,ElementLink037]
  Multiply = false
  _ConstraintType = 45
  _LinkVersion = 1
  _Parent = -> Constraints001
FEATURE [App::FeaturePython] ElementLink036  label="_Element019"  # link proxy (typed FeaturePython)
  LinkTransform = true
  LinkedObject = -> _Element019
  _LinkVersion = 1
  _Parent = -> Constraint021
FEATURE [Part::FeaturePython] _Element019  # link proxy (typed FeaturePython)
  Detach = false
  LinkTransform = true
  LinkedObject = -> Link008 [6.Edge9]
  _LinkVersion = 1
  _Parent = -> Elements001
FEATURE [App::FeaturePython] ElementLink037  label="_Element020"  # link proxy (typed FeaturePython)
  LinkTransform = true
  LinkedObject = -> _Element020
  _LinkVersion = 1
  _Parent = -> Constraint021
FEATURE [Part::FeaturePython] _Element020  # link proxy (typed FeaturePython)
  Detach = false
  LinkTransform = true
  LinkedObject = -> Link [Pocket010.Edge145]
  _LinkVersion = 1
  _Parent = -> Elements001
FEATURE [App::FeaturePython] Constraint022  label="Attachment016"  # WARN: FeaturePython — macro-defined, semantics opaque (R4)
  Cascade = false
  Disabled = false
  Group = -> [ElementLink038,ElementLink039]
  Multiply = false
  _ConstraintType = 45
  _LinkVersion = 1
  _Parent = -> Constraints001
FEATURE [App::FeaturePython] ElementLink038  label="_Element021"  # link proxy (typed FeaturePython)
  LinkTransform = true
  LinkedObject = -> _Element021
  _LinkVersion = 1
  _Parent = -> Constraint022
FEATURE [Part::FeaturePython] _Element021  # link proxy (typed FeaturePython)
  Detach = false
  LinkTransform = true
  LinkedObject = -> Link008 [5.Edge9]
  _LinkVersion = 1
  _Parent = -> Elements001
FEATURE [App::FeaturePython] ElementLink039  label="_Element022"  # link proxy (typed FeaturePython)
  LinkTransform = true
  LinkedObject = -> _Element022
  _LinkVersion = 1
  _Parent = -> Constraint022
FEATURE [Part::FeaturePython] _Element022  # link proxy (typed FeaturePython)
  Detach = false
  LinkTransform = true
  LinkedObject = -> Link [Pocket010.Edge143]
  _LinkVersion = 1
  _Parent = -> Elements001
FEATURE [App::FeaturePython] Constraint023  label="Attachment017"  # WARN: FeaturePython — macro-defined, semantics opaque (R4)
  Cascade = false
  Disabled = false
  Group = -> [ElementLink040,ElementLink041]
  Multiply = false
  _ConstraintType = 45
  _LinkVersion = 1
  _Parent = -> Constraints001
FEATURE [App::FeaturePython] ElementLink040  label="_Element023"  # link proxy (typed FeaturePython)
  LinkTransform = true
  LinkedObject = -> _Element023
  _LinkVersion = 1
  _Parent = -> Constraint023
FEATURE [Part::FeaturePython] _Element023  # link proxy (typed FeaturePython)
  Detach = false
  LinkTransform = true
  LinkedObject = -> Link008 [4.Edge9]
  _LinkVersion = 1
  _Parent = -> Elements001
FEATURE [App::FeaturePython] ElementLink041  label="_Element024"  # link proxy (typed FeaturePython)
  LinkTransform = true
  LinkedObject = -> _Element024
  _LinkVersion = 1
  _Parent = -> Constraint023
FEATURE [Part::FeaturePython] _Element024  # link proxy (typed FeaturePython)
  Detach = false
  LinkTransform = true
  LinkedObject = -> Link [Pocket010.Edge147]
  _LinkVersion = 1
  _Parent = -> Elements001
FEATURE [App::FeaturePython] Constraint024  label="Attachment018"  # WARN: FeaturePython — macro-defined, semantics opaque (R4)
  Cascade = false
  Disabled = false
  Group = -> [ElementLink042,ElementLink043]
  Multiply = false
  _ConstraintType = 45
  _LinkVersion = 1
  _Parent = -> Constraints
FEATURE [App::FeaturePython] ElementLink042  label="Element023"  # link proxy (typed FeaturePython)
  LinkTransform = true
  LinkedObject = -> Element023
  _LinkVersion = 1
  _Parent = -> Constraint024
FEATURE [App::FeaturePython] ElementLink043  label="_Element025"  # link proxy (typed FeaturePython)
  LinkTransform = true
  LinkedObject = -> _Element025
  _LinkVersion = 1
  _Parent = -> Constraint024
FEATURE [Part::FeaturePython] _Element025  # link proxy (typed FeaturePython)
  Detach = false
  LinkTransform = true
  LinkedObject = -> Link009 [0.Edge9]
  _LinkVersion = 1
  _Parent = -> Elements
FEATURE [App::FeaturePython] Constraint025  label="Attachment019"  # WARN: FeaturePython — macro-defined, semantics opaque (R4)
  Cascade = false
  Disabled = false
  Group = -> [ElementLink044,ElementLink045]
  Multiply = false
  _ConstraintType = 45
  _LinkVersion = 1
  _Parent = -> Constraints
FEATURE [App::FeaturePython] ElementLink044  label="_Element026"  # link proxy (typed FeaturePython)
  LinkTransform = true
  LinkedObject = -> _Element026
  _LinkVersion = 1
  _Parent = -> Constraint025
FEATURE [Part::FeaturePython] _Element026  # link proxy (typed FeaturePython)
  Detach = false
  LinkTransform = true
  LinkedObject = -> Link009 [1.Edge7]
  _LinkVersion = 1
  _Parent = -> Elements
FEATURE [App::FeaturePython] ElementLink045  label="Element024"  # link proxy (typed FeaturePython)
  LinkTransform = true
  LinkedObject = -> Element024
  _LinkVersion = 1
  _Parent = -> Constraint025
FEATURE [App::FeaturePython] Constraint026  label="Attachment020"  # WARN: FeaturePython — macro-defined, semantics opaque (R4)
  Cascade = false
  Disabled = false
  Group = -> [ElementLink046,ElementLink047]
  Multiply = false
  _ConstraintType = 45
  _LinkVersion = 1
  _Parent = -> Constraints
FEATURE [App::FeaturePython] ElementLink046  label="Element025"  # link proxy (typed FeaturePython)
  LinkTransform = true
  LinkedObject = -> Element025
  _LinkVersion = 1
  _Parent = -> Constraint026
FEATURE [App::FeaturePython] ElementLink047  label="_Element027"  # link proxy (typed FeaturePython)
  LinkTransform = true
  LinkedObject = -> _Element027
  _LinkVersion = 1
  _Parent = -> Constraint026
FEATURE [Part::FeaturePython] _Element027  # link proxy (typed FeaturePython)
  Detach = false
  LinkTransform = true
  LinkedObject = -> Link009 [2.Edge9]
  _LinkVersion = 1
  _Parent = -> Elements
FEATURE [App::FeaturePython] Constraint027  label="Attachment021"  # WARN: FeaturePython — macro-defined, semantics opaque (R4)
  Cascade = false
  Disabled = false
  Group = -> [ElementLink048,ElementLink049]
  Multiply = false
  _ConstraintType = 45
  _LinkVersion = 1
  _Parent = -> Constraints
FEATURE [App::FeaturePython] ElementLink048  label="_Element028"  # link proxy (typed FeaturePython)
  LinkTransform = true
  LinkedObject = -> _Element028
  _LinkVersion = 1
  _Parent = -> Constraint027
FEATURE [Part::FeaturePython] _Element028  # link proxy (typed FeaturePython)
  Detach = false
  LinkTransform = true
  LinkedObject = -> Link009 [3.Edge9]
  _LinkVersion = 1
  _Parent = -> Elements
FEATURE [App::FeaturePython] ElementLink049  label="Element026"  # link proxy (typed FeaturePython)
  LinkTransform = true
  LinkedObject = -> Element026
  _LinkVersion = 1
  _Parent = -> Constraint027
FEATURE [App::FeaturePython] Constraint028  label="Attachment022"  # WARN: FeaturePython — macro-defined, semantics opaque (R4)
  Cascade = false
  Disabled = false
  Group = -> [ElementLink050,ElementLink051]
  Multiply = false
  _ConstraintType = 45
  _LinkVersion = 1
  _Parent = -> Constraints
FEATURE [App::FeaturePython] ElementLink050  label="_Element029"  # link proxy (typed FeaturePython)
  LinkTransform = true
  LinkedObject = -> _Element029
  _LinkVersion = 1
  _Parent = -> Constraint028
FEATURE [Part::FeaturePython] _Element029  # link proxy (typed FeaturePython)
  Detach = false
  LinkTransform = true
  LinkedObject = -> Link009 [4.Edge9]
  _LinkVersion = 1
  _Parent = -> Elements
FEATURE [App::FeaturePython] ElementLink051  label="Element027"  # link proxy (typed FeaturePython)
  LinkTransform = true
  LinkedObject = -> Element027
  _LinkVersion = 1
  _Parent = -> Constraint028
FEATURE [App::FeaturePython] Constraint029  label="Attachment023"  # WARN: FeaturePython — macro-defined, semantics opaque (R4)
  Cascade = false
  Disabled = false
  Group = -> [ElementLink052,ElementLink053]
  Multiply = false
  _ConstraintType = 45
  _LinkVersion = 1
  _Parent = -> Constraints
FEATURE [App::FeaturePython] ElementLink052  label="_Element030"  # link proxy (typed FeaturePython)
  LinkTransform = true
  LinkedObject = -> _Element030
  _LinkVersion = 1
  _Parent = -> Constraint029
FEATURE [Part::FeaturePython] _Element030  # link proxy (typed FeaturePython)
  Detach = false
  LinkTransform = true
  LinkedObject = -> Link009 [5.Edge9]
  _LinkVersion = 1
  _Parent = -> Elements
FEATURE [App::FeaturePython] ElementLink053  label="Element028"  # link proxy (typed FeaturePython)
  LinkTransform = true
  LinkedObject = -> Element028
  _LinkVersion = 1
  _Parent = -> Constraint029
FEATURE [App::FeaturePython] Constraint030  label="Attachment024"  # WARN: FeaturePython — macro-defined, semantics opaque (R4)
  Cascade = false
  Disabled = false
  Group = -> [ElementLink054,ElementLink055]
  Multiply = false
  _ConstraintType = 45
  _LinkVersion = 1
  _Parent = -> Constraints
FEATURE [App::FeaturePython] ElementLink054  label="_Element031"  # link proxy (typed FeaturePython)
  LinkTransform = true
  LinkedObject = -> _Element031
  _LinkVersion = 1
  _Parent = -> Constraint030
FEATURE [Part::FeaturePython] _Element031  # link proxy (typed FeaturePython)
  Detach = false
  LinkTransform = true
  LinkedObject = -> Link009 [6.Edge9]
  _LinkVersion = 1
  _Parent = -> Elements
FEATURE [App::FeaturePython] ElementLink055  label="Element029"  # link proxy (typed FeaturePython)
  LinkTransform = true
  LinkedObject = -> Element029
  _LinkVersion = 1
  _Parent = -> Constraint030
FEATURE [App::FeaturePython] Constraint031  label="Attachment025"  # WARN: FeaturePython — macro-defined, semantics opaque (R4)
  Cascade = false
  Disabled = false
  Group = -> [ElementLink056,ElementLink057]
  Multiply = false
  _ConstraintType = 45
  _LinkVersion = 1
  _Parent = -> Constraints
FEATURE [App::FeaturePython] ElementLink056  label="_Element032"  # link proxy (typed FeaturePython)
  LinkTransform = true
  LinkedObject = -> _Element032
  _LinkVersion = 1
  _Parent = -> Constraint031
FEATURE [Part::FeaturePython] _Element032  # link proxy (typed FeaturePython)
  Detach = false
  LinkTransform = true
  LinkedObject = -> Link009 [7.Edge9]
  _LinkVersion = 1
  _Parent = -> Elements
FEATURE [App::FeaturePython] ElementLink057  label="Element030"  # link proxy (typed FeaturePython)
  LinkTransform = true
  LinkedObject = -> Element030
  _LinkVersion = 1
  _Parent = -> Constraint031
FEATURE [App::FeaturePython] Constraint032  label="Attachment026"  # WARN: FeaturePython — macro-defined, semantics opaque (R4)
  Cascade = false
  Disabled = false
  Group = -> [ElementLink058,ElementLink059]
  Multiply = false
  _ConstraintType = 45
  _LinkVersion = 1
  _Parent = -> Constraints
FEATURE [App::FeaturePython] ElementLink058  label="_Element033"  # link proxy (typed FeaturePython)
  LinkTransform = true
  LinkedObject = -> _Element033
  _LinkVersion = 1
  _Parent = -> Constraint032
FEATURE [Part::FeaturePython] _Element033  # link proxy (typed FeaturePython)
  Detach = false
  LinkTransform = true
  LinkedObject = -> Link009 [8.Edge9]
  _LinkVersion = 1
  _Parent = -> Elements
FEATURE [App::FeaturePython] ElementLink059  label="Element031"  # link proxy (typed FeaturePython)
  LinkTransform = true
  LinkedObject = -> Element031
  _LinkVersion = 1
  _Parent = -> Constraint032
FEATURE [App::FeaturePython] Constraint033  label="Attachment027"  # WARN: FeaturePython — macro-defined, semantics opaque (R4)
  Cascade = false
  Disabled = false
  Group = -> [ElementLink060,ElementLink061]
  Multiply = false
  _ConstraintType = 45
  _LinkVersion = 1
  _Parent = -> Constraints
FEATURE [App::FeaturePython] ElementLink060  label="_Element034"  # link proxy (typed FeaturePython)
  LinkTransform = true
  LinkedObject = -> _Element034
  _LinkVersion = 1
  _Parent = -> Constraint033
FEATURE [Part::FeaturePython] _Element034  # link proxy (typed FeaturePython)
  Detach = false
  LinkTransform = true
  LinkedObject = -> Link010 [0.Edge9]
  _LinkVersion = 1
  _Parent = -> Elements
FEATURE [App::FeaturePython] ElementLink061  label="_Element035"  # link proxy (typed FeaturePython)
  LinkTransform = true
  LinkedObject = -> _Element035
  _LinkVersion = 1
  _Parent = -> Constraint033
FEATURE [Part::FeaturePython] _Element035  # link proxy (typed FeaturePython)
  Detach = false
  LinkTransform = true
  LinkedObject = -> Link001 [Pocket011.Edge104]
  _LinkVersion = 1
  _Parent = -> Elements
FEATURE [App::FeaturePython] Constraint034  label="Attachment028"  # WARN: FeaturePython — macro-defined, semantics opaque (R4)
  Cascade = false
  Disabled = false
  Group = -> [ElementLink062,ElementLink063]
  Multiply = false
  _ConstraintType = 45
  _LinkVersion = 1
  _Parent = -> Constraints
FEATURE [App::FeaturePython] ElementLink062  label="_Element036"  # link proxy (typed FeaturePython)
  LinkTransform = true
  LinkedObject = -> _Element036
  _LinkVersion = 1
  _Parent = -> Constraint034
FEATURE [Part::FeaturePython] _Element036  # link proxy (typed FeaturePython)
  Detach = false
  LinkTransform = true
  LinkedObject = -> Link010 [1.Edge9]
  _LinkVersion = 1
  _Parent = -> Elements
FEATURE [App::FeaturePython] ElementLink063  label="_Element037"  # link proxy (typed FeaturePython)
  LinkTransform = true
  LinkedObject = -> _Element037
  _LinkVersion = 1
  _Parent = -> Constraint034
FEATURE [Part::FeaturePython] _Element037  # link proxy (typed FeaturePython)
  Detach = false
  LinkTransform = true
  LinkedObject = -> Link001 [Pocket011.Edge108]
  _LinkVersion = 1
  _Parent = -> Elements
FEATURE [App::FeaturePython] Constraint035  label="Attachment029"  # WARN: FeaturePython — macro-defined, semantics opaque (R4)
  Cascade = false
  Disabled = false
  Group = -> [ElementLink064,ElementLink065]
  Multiply = false
  _ConstraintType = 45
  _LinkVersion = 1
  _Parent = -> Constraints
FEATURE [App::FeaturePython] ElementLink064  label="_Element038"  # link proxy (typed FeaturePython)
  LinkTransform = true
  LinkedObject = -> _Element038
  _LinkVersion = 1
  _Parent = -> Constraint035
FEATURE [Part::FeaturePython] _Element038  # link proxy (typed FeaturePython)
  Detach = false
  LinkTransform = true
  LinkedObject = -> Link010 [2.Edge9]
  _LinkVersion = 1
  _Parent = -> Elements
FEATURE [App::FeaturePython] ElementLink065  label="_Element039"  # link proxy (typed FeaturePython)
  LinkTransform = true
  LinkedObject = -> _Element039
  _LinkVersion = 1
  _Parent = -> Constraint035
FEATURE [Part::FeaturePython] _Element039  # link proxy (typed FeaturePython)
  Detach = false
  LinkTransform = true
  LinkedObject = -> Link001 [Pocket011.Edge106]
  _LinkVersion = 1
  _Parent = -> Elements
FEATURE [App::FeaturePython] Constraint036  label="Attachment030"  # WARN: FeaturePython — macro-defined, semantics opaque (R4)
  Cascade = false
  Disabled = false
  Group = -> [ElementLink066,ElementLink067]
  Multiply = false
  _ConstraintType = 45
  _LinkVersion = 1
  _Parent = -> Constraints
FEATURE [App::FeaturePython] ElementLink066  label="_Element040"  # link proxy (typed FeaturePython)
  LinkTransform = true
  LinkedObject = -> _Element040
  _LinkVersion = 1
  _Parent = -> Constraint036
FEATURE [Part::FeaturePython] _Element040  # link proxy (typed FeaturePython)
  Detach = false
  LinkTransform = true
  LinkedObject = -> Link010 [3.Edge9]
  _LinkVersion = 1
  _Parent = -> Elements
FEATURE [App::FeaturePython] ElementLink067  label="_Element041"  # link proxy (typed FeaturePython)
  LinkTransform = true
  LinkedObject = -> _Element041
  _LinkVersion = 1
  _Parent = -> Constraint036
FEATURE [Part::FeaturePython] _Element041  # link proxy (typed FeaturePython)
  Detach = false
  LinkTransform = true
  LinkedObject = -> Link001 [Pocket011.Edge102]
  _LinkVersion = 1
  _Parent = -> Elements
FEATURE [App::FeaturePython] Constraint037  label="Attachment031"  # WARN: FeaturePython — macro-defined, semantics opaque (R4)
  Cascade = false
  Disabled = false
  Group = -> [ElementLink068,ElementLink069]
  Multiply = false
  _ConstraintType = 45
  _LinkVersion = 1
  _Parent = -> Constraints
FEATURE [App::FeaturePython] ElementLink068  label="_Element042"  # link proxy (typed FeaturePython)
  LinkTransform = true
  LinkedObject = -> _Element042
  _LinkVersion = 1
  _Parent = -> Constraint037
FEATURE [Part::FeaturePython] _Element042  # link proxy (typed FeaturePython)
  Detach = false
  LinkTransform = true
  LinkedObject = -> Link010 [7.Edge9]
  _LinkVersion = 1
  _Parent = -> Elements
FEATURE [App::FeaturePython] ElementLink069  label="_Element043"  # link proxy (typed FeaturePython)
  LinkTransform = true
  LinkedObject = -> _Element043
  _LinkVersion = 1
  _Parent = -> Constraint037
FEATURE [Part::FeaturePython] _Element043  # link proxy (typed FeaturePython)
  Detach = false
  LinkTransform = true
  LinkedObject = -> Link001 [Pocket011.Edge130]
  _LinkVersion = 1
  _Parent = -> Elements
FEATURE [App::FeaturePython] Constraint038  label="Attachment032"  # WARN: FeaturePython — macro-defined, semantics opaque (R4)
  Cascade = false
  Disabled = false
  Group = -> [ElementLink070,ElementLink071]
  Multiply = false
  _ConstraintType = 45
  _LinkVersion = 1
  _Parent = -> Constraints
FEATURE [App::FeaturePython] ElementLink070  label="_Element044"  # link proxy (typed FeaturePython)
  LinkTransform = true
  LinkedObject = -> _Element044
  _LinkVersion = 1
  _Parent = -> Constraint038
FEATURE [Part::FeaturePython] _Element044  # link proxy (typed FeaturePython)
  Detach = false
  LinkTransform = true
  LinkedObject = -> Link010 [6.Edge9]
  _LinkVersion = 1
  _Parent = -> Elements
FEATURE [App::FeaturePython] ElementLink071  label="_Element045"  # link proxy (typed FeaturePython)
  LinkTransform = true
  LinkedObject = -> _Element045
  _LinkVersion = 1
  _Parent = -> Constraint038
FEATURE [Part::FeaturePython] _Element045  # link proxy (typed FeaturePython)
  Detach = false
  LinkTransform = true
  LinkedObject = -> Link001 [Pocket011.Edge134]
  _LinkVersion = 1
  _Parent = -> Elements
FEATURE [App::FeaturePython] Constraint039  label="Attachment033"  # WARN: FeaturePython — macro-defined, semantics opaque (R4)
  Cascade = false
  Disabled = false
  Group = -> [ElementLink072,ElementLink073]
  Multiply = false
  _ConstraintType = 45
  _LinkVersion = 1
  _Parent = -> Constraints
FEATURE [App::FeaturePython] ElementLink072  label="_Element046"  # link proxy (typed FeaturePython)
  LinkTransform = true
  LinkedObject = -> _Element046
  _LinkVersion = 1
  _Parent = -> Constraint039
FEATURE [Part::FeaturePython] _Element046  # link proxy (typed FeaturePython)
  Detach = false
  LinkTransform = true
  LinkedObject = -> Link010 [5.Edge9]
  _LinkVersion = 1
  _Parent = -> Elements
FEATURE [App::FeaturePython] ElementLink073  label="_Element047"  # link proxy (typed FeaturePython)
  LinkTransform = true
  LinkedObject = -> _Element047
  _LinkVersion = 1
  _Parent = -> Constraint039
FEATURE [Part::FeaturePython] _Element047  # link proxy (typed FeaturePython)
  Detach = false
  LinkTransform = true
  LinkedObject = -> Link001 [Pocket011.Edge128]
  _LinkVersion = 1
  _Parent = -> Elements
FEATURE [App::FeaturePython] Constraint040  label="Attachment034"  # WARN: FeaturePython — macro-defined, semantics opaque (R4)
  Cascade = false
  Disabled = false
  Group = -> [ElementLink074,ElementLink075]
  Multiply = false
  _ConstraintType = 45
  _LinkVersion = 1
  _Parent = -> Constraints
FEATURE [App::FeaturePython] ElementLink074  label="_Element048"  # link proxy (typed FeaturePython)
  LinkTransform = true
  LinkedObject = -> _Element048
  _LinkVersion = 1
  _Parent = -> Constraint040
FEATURE [Part::FeaturePython] _Element048  # link proxy (typed FeaturePython)
  Detach = false
  LinkTransform = true
  LinkedObject = -> Link010 [4.Edge9]
  _LinkVersion = 1
  _Parent = -> Elements
FEATURE [App::FeaturePython] ElementLink075  label="_Element049"  # link proxy (typed FeaturePython)
  LinkTransform = true
  LinkedObject = -> _Element049
  _LinkVersion = 1
  _Parent = -> Constraint040
FEATURE [Part::FeaturePython] _Element049  # link proxy (typed FeaturePython)
  Detach = false
  LinkTransform = true
  LinkedObject = -> Link001 [Pocket011.Edge132]
  _LinkVersion = 1
  _Parent = -> Elements
FEATURE [App::FeaturePython] Constraint041  label="Attachment035"  # WARN: FeaturePython — macro-defined, semantics opaque (R4)
  Cascade = false
  Disabled = false
  Group = -> [ElementLink076,ElementLink077]
  Multiply = false
  _ConstraintType = 45
  _LinkVersion = 1
  _Parent = -> Constraints005
FEATURE [App::FeaturePython] ElementLink076  label="_Element050"  # link proxy (typed FeaturePython)
  LinkTransform = true
  LinkedObject = -> _Element050
  _LinkVersion = 1
  _Parent = -> Constraint041
FEATURE [Part::FeaturePython] _Element050  # link proxy (typed FeaturePython)
  Detach = false
  LinkTransform = true
  LinkedObject = -> Link006 [Chamfer001.Edge36]
  _LinkVersion = 1
  _Parent = -> Elements005
FEATURE [App::FeaturePython] ElementLink077  label="_Element051"  # link proxy (typed FeaturePython)
  LinkTransform = true
  LinkedObject = -> _Element051
  _LinkVersion = 1
  _Parent = -> Constraint041
FEATURE [Part::FeaturePython] _Element051  # link proxy (typed FeaturePython)
  Detach = false
  LinkTransform = true
  LinkedObject = -> Link012 [0.Edge4]
  _LinkVersion = 1
  _Parent = -> Elements005
FEATURE [App::FeaturePython] Constraint042  label="Attachment036"  # WARN: FeaturePython — macro-defined, semantics opaque (R4)
  Cascade = false
  Disabled = false
  Group = -> [ElementLink078,ElementLink079]
  Multiply = false
  _ConstraintType = 45
  _LinkVersion = 1
  _Parent = -> Constraints005
FEATURE [App::FeaturePython] ElementLink078  label="_Element052"  # link proxy (typed FeaturePython)
  LinkTransform = true
  LinkedObject = -> _Element052
  _LinkVersion = 1
  _Parent = -> Constraint042
FEATURE [Part::FeaturePython] _Element052  # link proxy (typed FeaturePython)
  Detach = false
  LinkTransform = true
  LinkedObject = -> Link012 [1.Edge4]
  _LinkVersion = 1
  _Parent = -> Elements005
FEATURE [App::FeaturePython] ElementLink079  label="_Element053"  # link proxy (typed FeaturePython)
  LinkTransform = true
  LinkedObject = -> _Element053
  _LinkVersion = 1
  _Parent = -> Constraint042
FEATURE [Part::FeaturePython] _Element053  # link proxy (typed FeaturePython)
  Detach = false
  LinkTransform = true
  LinkedObject = -> Link006 [Chamfer001.Edge35]
  _LinkVersion = 1
  _Parent = -> Elements005
FEATURE [App::FeaturePython] Constraint043  label="Attachment037"  # WARN: FeaturePython — macro-defined, semantics opaque (R4)
  Cascade = false
  Disabled = false
  Group = -> [ElementLink080,ElementLink081]
  Multiply = false
  _ConstraintType = 45
  _LinkVersion = 1
  _Parent = -> Constraints005
FEATURE [App::FeaturePython] ElementLink080  label="_Element054"  # link proxy (typed FeaturePython)
  LinkTransform = true
  LinkedObject = -> _Element054
  _LinkVersion = 1
  _Parent = -> Constraint043
FEATURE [Part::FeaturePython] _Element054  # link proxy (typed FeaturePython)
  Detach = false
  LinkTransform = true
  LinkedObject = -> Link012 [2.Edge4]
  _LinkVersion = 1
  _Parent = -> Elements005
FEATURE [App::FeaturePython] ElementLink081  label="_Element055"  # link proxy (typed FeaturePython)
  LinkTransform = true
  LinkedObject = -> _Element055
  _LinkVersion = 1
  _Parent = -> Constraint043
FEATURE [Part::FeaturePython] _Element055  # link proxy (typed FeaturePython)
  Detach = false
  LinkTransform = true
  LinkedObject = -> Link006 [Chamfer001.Edge33]
  _LinkVersion = 1
  _Parent = -> Elements005
FEATURE [App::FeaturePython] Constraint044  label="Attachment038"  # WARN: FeaturePython — macro-defined, semantics opaque (R4)
  Cascade = false
  Disabled = false
  Group = -> [ElementLink082,ElementLink083]
  Multiply = false
  _ConstraintType = 45
  _LinkVersion = 1
  _Parent = -> Constraints005
FEATURE [App::FeaturePython] ElementLink082  label="_Element056"  # link proxy (typed FeaturePython)
  LinkTransform = true
  LinkedObject = -> _Element056
  _LinkVersion = 1
  _Parent = -> Constraint044
FEATURE [Part::FeaturePython] _Element056  # link proxy (typed FeaturePython)
  Detach = false
  LinkTransform = true
  LinkedObject = -> Link012 [3.Edge4]
  _LinkVersion = 1
  _Parent = -> Elements005
FEATURE [App::FeaturePython] ElementLink083  label="_Element057"  # link proxy (typed FeaturePython)
  LinkTransform = true
  LinkedObject = -> _Element057
  _LinkVersion = 1
  _Parent = -> Constraint044
FEATURE [Part::FeaturePython] _Element057  # link proxy (typed FeaturePython)
  Detach = false
  LinkTransform = true
  LinkedObject = -> Link006 [Chamfer001.Edge34]
  _LinkVersion = 1
  _Parent = -> Elements005
FEATURE [App::FeaturePython] Constraint045  label="Attachment039"  # WARN: FeaturePython — macro-defined, semantics opaque (R4)
  Cascade = false
  Disabled = false
  Group = -> [ElementLink084,ElementLink085]
  Multiply = false
  _ConstraintType = 45
  _LinkVersion = 1
  _Parent = -> Constraints005
FEATURE [App::FeaturePython] ElementLink084  label="_Element058"  # link proxy (typed FeaturePython)
  LinkTransform = true
  LinkedObject = -> _Element058
  _LinkVersion = 1
  _Parent = -> Constraint045
FEATURE [Part::FeaturePython] _Element058  # link proxy (typed FeaturePython)
  Detach = false
  LinkTransform = true
  LinkedObject = -> Link006 [Chamfer001.Edge31]
  _LinkVersion = 1
  _Parent = -> Elements005
FEATURE [App::FeaturePython] ElementLink085  label="_Element059"  # link proxy (typed FeaturePython)
  LinkTransform = true
  LinkedObject = -> _Element059
  _LinkVersion = 1
  _Parent = -> Constraint045
FEATURE [Part::FeaturePython] _Element059  # link proxy (typed FeaturePython)
  Detach = false
  LinkTransform = true
  LinkedObject = -> Link011 [1.Edge4]
  _LinkVersion = 1
  _Parent = -> Elements005
FEATURE [App::FeaturePython] Constraint046  label="Attachment040"  # WARN: FeaturePython — macro-defined, semantics opaque (R4)
  Cascade = false
  Disabled = false
  Group = -> [ElementLink086,ElementLink087]
  Multiply = false
  _ConstraintType = 45
  _LinkVersion = 1
  _Parent = -> Constraints005
FEATURE [App::FeaturePython] ElementLink086  label="_Element060"  # link proxy (typed FeaturePython)
  LinkTransform = true
  LinkedObject = -> _Element060
  _LinkVersion = 1
  _Parent = -> Constraint046
FEATURE [Part::FeaturePython] _Element060  # link proxy (typed FeaturePython)
  Detach = false
  LinkTransform = true
  LinkedObject = -> Link011 [0.Edge4]
  _LinkVersion = 1
  _Parent = -> Elements005
FEATURE [App::FeaturePython] ElementLink087  label="_Element061"  # link proxy (typed FeaturePython)
  LinkTransform = true
  LinkedObject = -> _Element061
  _LinkVersion = 1
  _Parent = -> Constraint046
FEATURE [Part::FeaturePython] _Element061  # link proxy (typed FeaturePython)
  Detach = false
  LinkTransform = true
  LinkedObject = -> Link006 [Chamfer001.Edge32]
  _LinkVersion = 1
  _Parent = -> Elements005
FEATURE [App::FeaturePython] Constraint047  label="Attachment041"  # WARN: FeaturePython — macro-defined, semantics opaque (R4)
  Cascade = false
  Disabled = false
  Group = -> [ElementLink088,ElementLink089]
  Multiply = false
  _ConstraintType = 45
  _LinkVersion = 1
  _Parent = -> Constraints005
FEATURE [App::FeaturePython] ElementLink088  label="_Element062"  # link proxy (typed FeaturePython)
  LinkTransform = true
  LinkedObject = -> _Element062
  _LinkVersion = 1
  _Parent = -> Constraint047
FEATURE [Part::FeaturePython] _Element062  # link proxy (typed FeaturePython)
  Detach = false
  LinkTransform = true
  LinkedObject = -> Link006 [Chamfer001.Edge29]
  _LinkVersion = 1
  _Parent = -> Elements005
FEATURE [App::FeaturePython] ElementLink089  label="_Element063"  # link proxy (typed FeaturePython)
  LinkTransform = true
  LinkedObject = -> _Element063
  _LinkVersion = 1
  _Parent = -> Constraint047
FEATURE [Part::FeaturePython] _Element063  # link proxy (typed FeaturePython)
  Detach = false
  LinkTransform = true
  LinkedObject = -> Link011 [2.Edge4]
  _LinkVersion = 1
  _Parent = -> Elements005
FEATURE [App::FeaturePython] Constraint048  label="Attachment042"  # WARN: FeaturePython — macro-defined, semantics opaque (R4)
  Cascade = false
  Disabled = false
  Group = -> [ElementLink090,ElementLink091]
  Multiply = false
  _ConstraintType = 45
  _LinkVersion = 1
  _Parent = -> Constraints005
FEATURE [App::FeaturePython] ElementLink090  label="_Element064"  # link proxy (typed FeaturePython)
  LinkTransform = true
  LinkedObject = -> _Element064
  _LinkVersion = 1
  _Parent = -> Constraint048
FEATURE [Part::FeaturePython] _Element064  # link proxy (typed FeaturePython)
  Detach = false
  LinkTransform = true
  LinkedObject = -> Link011 [3.Edge4]
  _LinkVersion = 1
  _Parent = -> Elements005
FEATURE [App::FeaturePython] ElementLink091  label="_Element065"  # link proxy (typed FeaturePython)
  LinkTransform = true
  LinkedObject = -> _Element065
  _LinkVersion = 1
  _Parent = -> Constraint048
FEATURE [Part::FeaturePython] _Element065  # link proxy (typed FeaturePython)
  Detach = false
  LinkTransform = true
  LinkedObject = -> Link006 [Chamfer001.Edge30]
  _LinkVersion = 1
  _Parent = -> Elements005
FEATURE [Part::FeaturePython] Element041  label="limit-bolt-mate"  # link proxy (typed FeaturePython)
  Detach = false
  LinkTransform = true
  LinkedObject = -> Link001 [Pocket012.Edge63]
  _LinkVersion = 1
  _Parent = -> Elements
FEATURE [App::FeaturePython] Constraint049  label="Attachment043"  # WARN: FeaturePython — macro-defined, semantics opaque (R4)
  Cascade = false
  Disabled = false
  Group = -> [ElementLink092,ElementLink093]
  Multiply = false
  _ConstraintType = 45
  _LinkVersion = 1
  _Parent = -> Constraints
FEATURE [App::FeaturePython] ElementLink092  label="limit-bolt-mate"  # link proxy (typed FeaturePython)
  LinkTransform = true
  LinkedObject = -> Element041
  _LinkVersion = 1
  _Parent = -> Constraint049
FEATURE [App::FeaturePython] ElementLink093  label="_Element066"  # link proxy (typed FeaturePython)
  LinkTransform = true
  LinkedObject = -> _Element066
  _LinkVersion = 1
  _Parent = -> Constraint049
FEATURE [Part::FeaturePython] _Element066  # link proxy (typed FeaturePython)
  Detach = false
  LinkTransform = true
  LinkedObject = -> Link014 [Edge5]
  _LinkVersion = 1
  _Parent = -> Elements
FEATURE [App::FeaturePython] Constraint050  label="Attachment044"  # WARN: FeaturePython — macro-defined, semantics opaque (R4)
  Cascade = false
  Disabled = false
  Group = -> [ElementLink094,ElementLink095]
  Multiply = false
  _ConstraintType = 45
  _LinkVersion = 1
  _Parent = -> Constraints
FEATURE [App::FeaturePython] ElementLink094  label="_Element067"  # link proxy (typed FeaturePython)
  LinkTransform = true
  LinkedObject = -> _Element067
  _LinkVersion = 1
  _Parent = -> Constraint050
FEATURE [Part::FeaturePython] _Element067  # link proxy (typed FeaturePython)
  Detach = false
  LinkTransform = true
  LinkedObject = -> Link014 [Edge1]
  _LinkVersion = 1
  _Parent = -> Elements
FEATURE [App::FeaturePython] ElementLink095  label="_Element068"  # link proxy (typed FeaturePython)
  LinkTransform = true
  LinkedObject = -> _Element068
  _LinkVersion = 1
  _Parent = -> Constraint050
FEATURE [Part::FeaturePython] _Element068  # link proxy (typed FeaturePython)
  Detach = false
  LinkTransform = true
  LinkedObject = -> Link015 [Edge13]
  _LinkVersion = 1
  _Parent = -> Elements
FEATURE [App::FeaturePython] Constraint051  label="Attachment045"  # WARN: FeaturePython — macro-defined, semantics opaque (R4)
  Cascade = false
  Disabled = false
  Group = -> [ElementLink096,ElementLink097]
  Multiply = false
  _ConstraintType = 45
  _LinkVersion = 1
  _Parent = -> Constraints
FEATURE [App::FeaturePython] ElementLink096  label="_Element069"  # link proxy (typed FeaturePython)
  LinkTransform = true
  LinkedObject = -> _Element069
  Offset = pos=(0,0,10) rot=(0,0,1;0rad)
  Placement = pos=(-10,2.84e-14,0) rot=(0,0,1;0rad)
  _LinkVersion = 1
  _Parent = -> Constraint051
FEATURE [Part::FeaturePython] _Element069  # link proxy (typed FeaturePython)
  Detach = false
  LinkTransform = true
  LinkedObject = -> Link013 [Edge43]
  _LinkVersion = 1
  _Parent = -> Elements
FEATURE [App::FeaturePython] ElementLink097  label="limit-bolt-mate"  # link proxy (typed FeaturePython)
  LinkTransform = true
  LinkedObject = -> Element041
  _LinkVersion = 1
  _Parent = -> Constraint051
FEATURE [Part::FeaturePython] Element042  label="limit-bolt-mate"  # link proxy (typed FeaturePython)
  Detach = false
  LinkTransform = true
  LinkedObject = -> Link [Pocket013.Edge73]
  _LinkVersion = 1
  _Parent = -> Elements001
FEATURE [App::FeaturePython] Constraint052  label="Attachment046"  # WARN: FeaturePython — macro-defined, semantics opaque (R4)
  Cascade = false
  Disabled = false
  Group = -> [ElementLink098,ElementLink099]
  Multiply = false
  _ConstraintType = 45
  _LinkVersion = 1
  _Parent = -> Constraints001
FEATURE [App::FeaturePython] ElementLink098  label="_Element070"  # link proxy (typed FeaturePython)
  LinkTransform = true
  LinkedObject = -> _Element070
  _LinkVersion = 1
  _Parent = -> Constraint052
FEATURE [Part::FeaturePython] _Element070  # link proxy (typed FeaturePython)
  Detach = false
  LinkTransform = true
  LinkedObject = -> Link017 [Edge5]
  _LinkVersion = 1
  _Parent = -> Elements001
FEATURE [App::FeaturePython] ElementLink099  label="limit-bolt-mate"  # link proxy (typed FeaturePython)
  LinkTransform = true
  LinkedObject = -> Element042
  _LinkVersion = 1
  _Parent = -> Constraint052
FEATURE [App::FeaturePython] Constraint053  label="Attachment047"  # WARN: FeaturePython — macro-defined, semantics opaque (R4)
  Cascade = false
  Disabled = false
  Group = -> [ElementLink100,ElementLink101]
  Multiply = false
  _ConstraintType = 45
  _LinkVersion = 1
  _Parent = -> Constraints001
FEATURE [App::FeaturePython] ElementLink100  label="_Element071"  # link proxy (typed FeaturePython)
  LinkTransform = true
  LinkedObject = -> _Element071
  _LinkVersion = 1
  _Parent = -> Constraint053
FEATURE [Part::FeaturePython] _Element071  # link proxy (typed FeaturePython)
  Detach = false
  LinkTransform = true
  LinkedObject = -> Link017 [Edge1]
  _LinkVersion = 1
  _Parent = -> Elements001
FEATURE [App::FeaturePython] ElementLink101  label="_Element072"  # link proxy (typed FeaturePython)
  LinkTransform = true
  LinkedObject = -> _Element072
  _LinkVersion = 1
  _Parent = -> Constraint053
FEATURE [Part::FeaturePython] _Element072  # link proxy (typed FeaturePython)
  Detach = false
  LinkTransform = true
  LinkedObject = -> Link018 [Edge13]
  _LinkVersion = 1
  _Parent = -> Elements001
FEATURE [App::FeaturePython] Constraint054  label="Limit bolt Attachment"  # WARN: FeaturePython — macro-defined, semantics opaque (R4)
  Cascade = false
  Disabled = false
  Group = -> [ElementLink102,ElementLink103]
  Multiply = false
  _ConstraintType = 45
  _LinkVersion = 1
  _Parent = -> Constraints001
FEATURE [App::FeaturePython] ElementLink102  label="_Element073"  # link proxy (typed FeaturePython)
  LinkTransform = true
  LinkedObject = -> _Element073
  Offset = pos=(0,0,10) rot=(0,0,1;0rad)
  Placement = pos=(-10,0,2.2e-15) rot=(0,0,1;0rad)
  _LinkVersion = 1
  _Parent = -> Constraint054
FEATURE [Part::FeaturePython] _Element073  # link proxy (typed FeaturePython)
  Detach = false
  LinkTransform = true
  LinkedObject = -> Link016 [Edge43]
  _LinkVersion = 1
  _Parent = -> Elements001
FEATURE [App::FeaturePython] ElementLink103  label="limit-bolt-mate"  # link proxy (typed FeaturePython)
  LinkTransform = true
  LinkedObject = -> Element042
  _LinkVersion = 1
  _Parent = -> Constraint054
FEATURE [Part::FeaturePython] Element043  label="limit-mate"  # link proxy (typed FeaturePython)
  Detach = false
  LinkTransform = true
  LinkedObject = -> Link [Pocket014.Edge68]
  _LinkVersion = 1
  _Parent = -> Elements001
FEATURE [Part::FeaturePython] Element044  # link proxy (typed FeaturePython)
  Detach = false
  LinkTransform = true
  LinkedObject = -> Link001 [Pocket011.Edge50]
  _LinkVersion = 0
  _Parent = -> Elements
